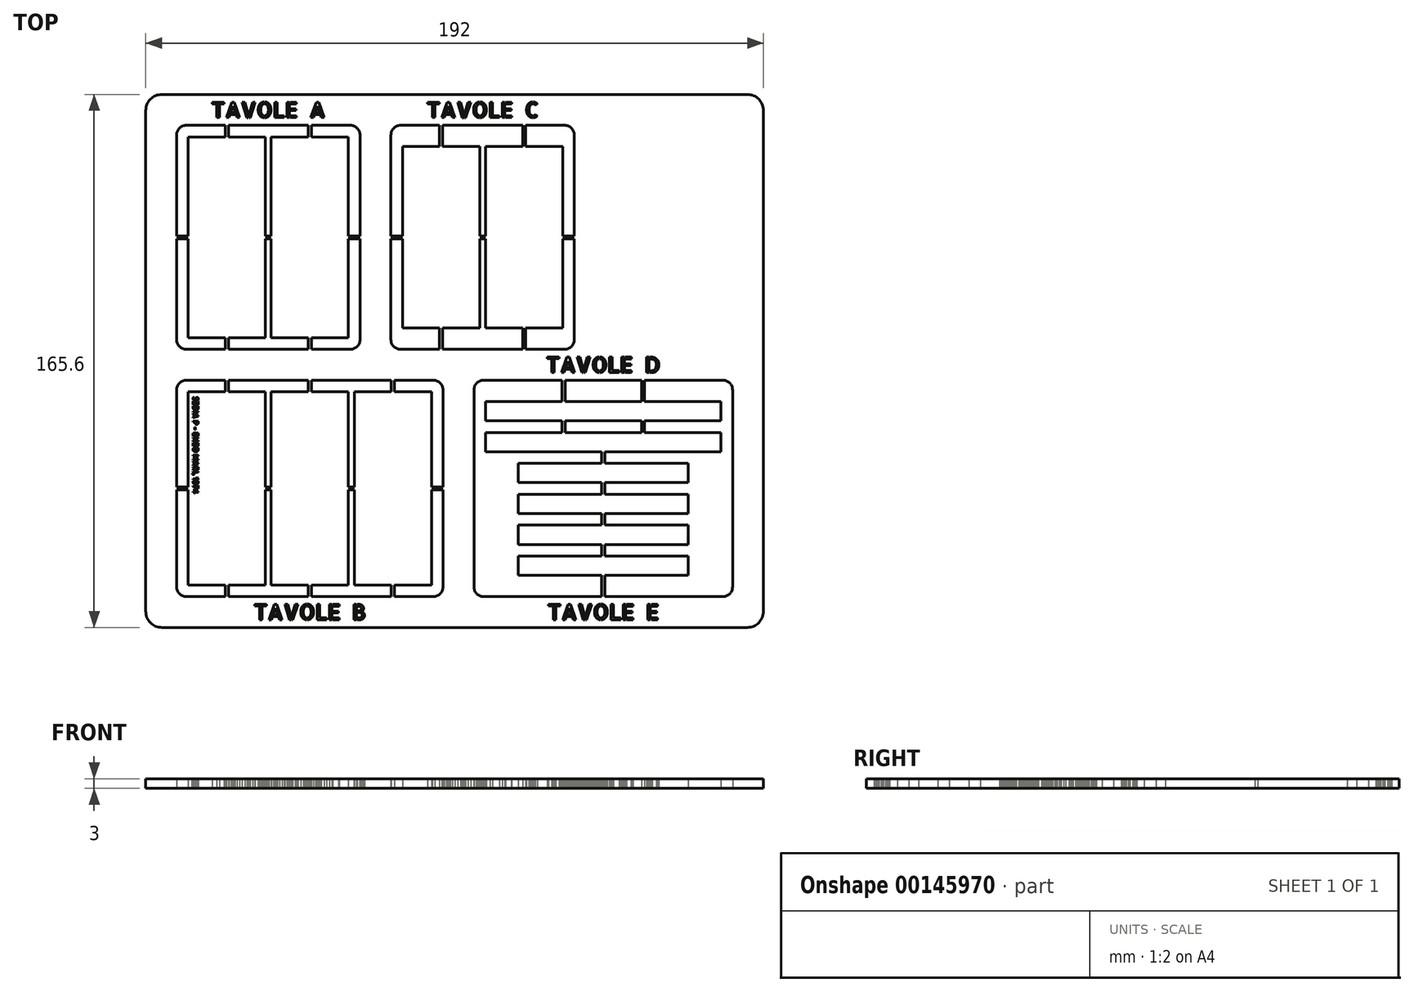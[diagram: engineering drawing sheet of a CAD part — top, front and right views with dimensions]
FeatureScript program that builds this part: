
annotation { "Feature Type Name" : "Feature", "Feature Type Description" : "" }
export const myFeature = defineFeature(function(context is Context, id is Id, definition is map)
    precondition{}
    {
        {
            assignVariable(context, id + "F0", {"name" : "scale", "anyValue" : 3 / 25});
        }
        {
            assignVariable(context, id + "F1", {"name" : "wood_thickness", "anyValue" : 25 * mm * getVariable(context, 'scale')});
        }
        {
            var Q0;
            Q0=qCreatedBy(makeId("Top.planeOp"),FACE);
            var sketch = newSketch(context, id + "F2", { "sketchPlane" : qUnion([Q0])});
            skLineSegment(sketch, "E0.bottom", {"start": v(9.6, 9.6) * mm, "end": v(24.72, 9.6) * mm});
            skLineSegment(sketch, "E0.top", {"start": v(9.6, 76.8) * mm, "end": v(24.72, 76.8) * mm});
            skLineSegment(sketch, "E0.left", {"start": v(9.6, 9.6) * mm, "end": v(9.6, 42.72) * mm});
            skLineSegment(sketch, "E0.right", {"start": v(92.4, 9.6) * mm, "end": v(92.4, 42.72) * mm});
            skLineSegment(sketch, "E1.bottom", {"start": v(13.2, 73.2) * mm, "end": v(24.72, 73.2) * mm});
            skLineSegment(sketch, "E1.top", {"start": v(13.2, 13.2) * mm, "end": v(24.72, 13.2) * mm});
            skLineSegment(sketch, "E1.left", {"start": v(13.2, 73.2) * mm, "end": v(13.2, 43.68) * mm});
            skLineSegment(sketch, "E1.right", {"start": v(37.2, 73.2) * mm, "end": v(37.2, 43.68) * mm});
            skLineSegment(sketch, "E2", {"start": v(9.6, 43.2) * mm, "end": v(13.2, 43.2) * mm, "construction": true});
            skLineSegment(sketch, "E3", {"start": v(25.2, 73.2) * mm, "end": v(25.2, 76.8) * mm, "construction": true});
            skLineSegment(sketch, "E4", {"start": v(25.2, 13.2) * mm, "end": v(25.2, 9.6) * mm, "construction": true});
            skLineSegment(sketch, "E5", {"start": v(9.6, 43.68) * mm, "end": v(13.2, 43.68) * mm});
            skLineSegment(sketch, "E6", {"start": v(9.6, 42.72) * mm, "end": v(13.2, 42.72) * mm});
            skLineSegment(sketch, "E7", {"start": v(24.72, 76.8) * mm, "end": v(24.72, 73.2) * mm});
            skLineSegment(sketch, "E8", {"start": v(25.68, 76.8) * mm, "end": v(25.68, 73.2) * mm});
            skLineSegment(sketch, "E9", {"start": v(24.72, 13.2) * mm, "end": v(24.72, 9.6) * mm});
            skLineSegment(sketch, "E10", {"start": v(25.68, 9.6) * mm, "end": v(25.68, 13.2) * mm});
            skLineSegment(sketch, "E11", {"start": v(24.72, 13.2) * mm, "end": v(25.2, 13.2) * mm, "construction": true});
            skLineSegment(sketch, "E12", {"start": v(25.68, 13.2) * mm, "end": v(37.2, 13.2) * mm});
            skLineSegment(sketch, "E13", {"start": v(25.2, 13.2) * mm, "end": v(25.68, 13.2) * mm, "construction": true});
            skLineSegment(sketch, "E14", {"start": v(13.2, 42.72) * mm, "end": v(13.2, 13.2) * mm});
            skLineSegment(sketch, "E15", {"start": v(13.2, 43.2) * mm, "end": v(13.2, 42.72) * mm, "construction": true});
            skLineSegment(sketch, "E16", {"start": v(13.2, 43.68) * mm, "end": v(13.2, 43.2) * mm, "construction": true});
            skLineSegment(sketch, "E17", {"start": v(24.72, 73.2) * mm, "end": v(25.2, 73.2) * mm, "construction": true});
            skLineSegment(sketch, "E18", {"start": v(25.2, 73.2) * mm, "end": v(25.68, 73.2) * mm, "construction": true});
            skLineSegment(sketch, "E19", {"start": v(25.68, 73.2) * mm, "end": v(37.2, 73.2) * mm});
            skLineSegment(sketch, "E20", {"start": v(13.2, 58.44) * mm, "end": v(37.2, 58.44) * mm, "construction": true});
            skLineSegment(sketch, "E21", {"start": v(13.2, 43.2) * mm, "end": v(37.2, 43.2) * mm, "construction": true});
            skLineSegment(sketch, "E22", {"start": v(37.2, 43.68) * mm, "end": v(37.2, 43.2) * mm, "construction": true});
            skLineSegment(sketch, "E23", {"start": v(37.2, 43.2) * mm, "end": v(37.2, 42.72) * mm, "construction": true});
            skLineSegment(sketch, "E24", {"start": v(37.2, 42.72) * mm, "end": v(37.2, 13.2) * mm});
            skLineSegment(sketch, "E25", {"start": v(39, 13.2) * mm, "end": v(50.52, 13.2) * mm});
            skLineSegment(sketch, "E26", {"start": v(50.52, 13.2) * mm, "end": v(51, 13.2) * mm, "construction": true});
            skLineSegment(sketch, "E27", {"start": v(51, 13.2) * mm, "end": v(51.48, 13.2) * mm, "construction": true});
            skLineSegment(sketch, "E28", {"start": v(51.48, 13.2) * mm, "end": v(63, 13.2) * mm});
            skLineSegment(sketch, "E29", {"start": v(64.8, 13.2) * mm, "end": v(76.32, 13.2) * mm});
            skLineSegment(sketch, "E30", {"start": v(76.32, 13.2) * mm, "end": v(76.8, 13.2) * mm, "construction": true});
            skLineSegment(sketch, "E31", {"start": v(76.8, 13.2) * mm, "end": v(77.28, 13.2) * mm, "construction": true});
            skLineSegment(sketch, "E32", {"start": v(77.28, 13.2) * mm, "end": v(88.8, 13.2) * mm});
            skLineSegment(sketch, "E33", {"start": v(39, 73.2) * mm, "end": v(50.52, 73.2) * mm});
            skLineSegment(sketch, "E34", {"start": v(50.52, 73.2) * mm, "end": v(51, 73.2) * mm, "construction": true});
            skLineSegment(sketch, "E35", {"start": v(51, 73.2) * mm, "end": v(51.48, 73.2) * mm, "construction": true});
            skLineSegment(sketch, "E36", {"start": v(51.48, 73.2) * mm, "end": v(63, 73.2) * mm});
            skLineSegment(sketch, "E37", {"start": v(64.8, 73.2) * mm, "end": v(76.32, 73.2) * mm});
            skLineSegment(sketch, "E38", {"start": v(76.32, 73.2) * mm, "end": v(76.8, 73.2) * mm, "construction": true});
            skLineSegment(sketch, "E39", {"start": v(76.8, 73.2) * mm, "end": v(77.28, 73.2) * mm, "construction": true});
            skLineSegment(sketch, "E40", {"start": v(77.28, 73.2) * mm, "end": v(88.8, 73.2) * mm});
            skLineSegment(sketch, "E41", {"start": v(39, 73.2) * mm, "end": v(39, 43.68) * mm});
            skLineSegment(sketch, "E42", {"start": v(39, 43.68) * mm, "end": v(39, 43.2) * mm, "construction": true});
            skLineSegment(sketch, "E43", {"start": v(39, 43.2) * mm, "end": v(39, 42.72) * mm, "construction": true});
            skLineSegment(sketch, "E44", {"start": v(39, 42.72) * mm, "end": v(39, 13.2) * mm});
            skLineSegment(sketch, "E45", {"start": v(63, 73.2) * mm, "end": v(63, 43.68) * mm});
            skLineSegment(sketch, "E46", {"start": v(63, 43.68) * mm, "end": v(63, 43.2) * mm, "construction": true});
            skLineSegment(sketch, "E47", {"start": v(63, 43.2) * mm, "end": v(63, 42.72) * mm, "construction": true});
            skLineSegment(sketch, "E48", {"start": v(63, 13.2) * mm, "end": v(63, 42.72) * mm});
            skLineSegment(sketch, "E49", {"start": v(64.8, 73.2) * mm, "end": v(64.8, 43.68) * mm});
            skLineSegment(sketch, "E50", {"start": v(64.8, 43.68) * mm, "end": v(64.8, 43.2) * mm, "construction": true});
            skLineSegment(sketch, "E51", {"start": v(64.8, 43.2) * mm, "end": v(64.8, 42.72) * mm, "construction": true});
            skLineSegment(sketch, "E52", {"start": v(64.8, 42.72) * mm, "end": v(64.8, 13.2) * mm});
            skLineSegment(sketch, "E53", {"start": v(88.8, 13.2) * mm, "end": v(88.8, 42.72) * mm});
            skLineSegment(sketch, "E54", {"start": v(88.8, 42.72) * mm, "end": v(88.8, 43.2) * mm, "construction": true});
            skLineSegment(sketch, "E55", {"start": v(88.8, 43.2) * mm, "end": v(88.8, 43.68) * mm, "construction": true});
            skLineSegment(sketch, "E56", {"start": v(88.8, 43.68) * mm, "end": v(88.8, 73.2) * mm});
            skLineSegment(sketch, "E57", {"start": v(37.2, 43.68) * mm, "end": v(39, 43.68) * mm});
            skLineSegment(sketch, "E58", {"start": v(39, 42.72) * mm, "end": v(37.2, 42.72) * mm});
            skLineSegment(sketch, "E59", {"start": v(63, 43.68) * mm, "end": v(64.8, 43.68) * mm});
            skLineSegment(sketch, "E60", {"start": v(64.8, 42.72) * mm, "end": v(63, 42.72) * mm});
            skLineSegment(sketch, "E61", {"start": v(88.8, 43.68) * mm, "end": v(92.4, 43.68) * mm});
            skLineSegment(sketch, "E62", {"start": v(88.8, 42.72) * mm, "end": v(92.4, 42.72) * mm});
            skLineSegment(sketch, "E63", {"start": v(24.72, 76.8) * mm, "end": v(25.68, 76.8) * mm});
            skLineSegment(sketch, "E64", {"start": v(25.68, 76.8) * mm, "end": v(50.52, 76.8) * mm});
            skLineSegment(sketch, "E65", {"start": v(24.72, 9.6) * mm, "end": v(25.68, 9.6) * mm});
            skLineSegment(sketch, "E66", {"start": v(25.68, 9.6) * mm, "end": v(50.52, 9.6) * mm});
            skLineSegment(sketch, "E67", {"start": v(50.52, 13.2) * mm, "end": v(50.52, 9.6) * mm});
            skLineSegment(sketch, "E68", {"start": v(51.48, 13.2) * mm, "end": v(51.48, 9.6) * mm});
            skLineSegment(sketch, "E69", {"start": v(76.32, 13.2) * mm, "end": v(76.32, 9.6) * mm});
            skLineSegment(sketch, "E70", {"start": v(77.28, 13.2) * mm, "end": v(77.28, 9.6) * mm});
            skLineSegment(sketch, "E71", {"start": v(76.32, 73.2) * mm, "end": v(76.32, 76.8) * mm});
            skLineSegment(sketch, "E72", {"start": v(77.28, 73.2) * mm, "end": v(77.28, 76.8) * mm});
            skLineSegment(sketch, "E73", {"start": v(50.52, 73.2) * mm, "end": v(50.52, 76.8) * mm});
            skLineSegment(sketch, "E74", {"start": v(51.48, 73.2) * mm, "end": v(51.48, 76.8) * mm});
            skLineSegment(sketch, "E75", {"start": v(50.52, 76.8) * mm, "end": v(51.48, 76.8) * mm});
            skLineSegment(sketch, "E76", {"start": v(51.48, 76.8) * mm, "end": v(76.32, 76.8) * mm});
            skLineSegment(sketch, "E77", {"start": v(76.32, 76.8) * mm, "end": v(77.28, 76.8) * mm});
            skLineSegment(sketch, "E78", {"start": v(77.28, 76.8) * mm, "end": v(92.4, 76.8) * mm});
            skLineSegment(sketch, "E79", {"start": v(92.4, 43.68) * mm, "end": v(92.4, 76.8) * mm});
            skLineSegment(sketch, "E80", {"start": v(92.4, 42.72) * mm, "end": v(92.4, 43.68) * mm});
            skLineSegment(sketch, "E81", {"start": v(77.28, 9.6) * mm, "end": v(92.4, 9.6) * mm});
            skLineSegment(sketch, "E82", {"start": v(76.32, 9.6) * mm, "end": v(77.28, 9.6) * mm});
            skLineSegment(sketch, "E83", {"start": v(51.48, 9.6) * mm, "end": v(76.32, 9.6) * mm});
            skLineSegment(sketch, "E84", {"start": v(50.52, 9.6) * mm, "end": v(51.48, 9.6) * mm});
            skLineSegment(sketch, "E85", {"start": v(9.6, 42.72) * mm, "end": v(9.6, 43.68) * mm});
            skLineSegment(sketch, "E86", {"start": v(9.6, 43.68) * mm, "end": v(9.6, 76.8) * mm});
            skSolve(sketch);
        }
        {
            var Q0;
            Q0=makeQuery(id+"F2.imprint","IMPRINT",FACE,{"disambiguationData":[TD([[makeQuery(id+"F2.imprint","IMPRINT",EDGE,{"derivedFrom":sQuery(id+"F2.wireOp",EDGE,"E1.bottom")}),-1.0]])]});
            extrude(context, id + "F3", {"entities" : qUnion([Q0]), "depth" : getVariable(context, 'wood_thickness')});
        }
        {
            var Q0;
            Q0=qCreatedBy(makeId("Top.planeOp"),FACE);
            var sketch = newSketch(context, id + "F4", { "sketchPlane" : qUnion([Q0])});
            skLineSegment(sketch, "E87.bottom", {"start": v(9.6, 86.4) * mm, "end": v(24.72, 86.4) * mm});
            skLineSegment(sketch, "E87.top", {"start": v(9.6, 156) * mm, "end": v(24.72, 156) * mm});
            skLineSegment(sketch, "E87.left", {"start": v(9.6, 86.4) * mm, "end": v(9.6, 120.72) * mm});
            skLineSegment(sketch, "E87.right", {"start": v(66.6, 86.4) * mm, "end": v(66.6, 120.72) * mm});
            skLineSegment(sketch, "E88.bottom", {"start": v(13.2, 152.4) * mm, "end": v(24.72, 152.4) * mm});
            skLineSegment(sketch, "E88.top", {"start": v(13.2, 90) * mm, "end": v(24.72, 90) * mm});
            skLineSegment(sketch, "E88.left", {"start": v(13.2, 152.4) * mm, "end": v(13.2, 121.68) * mm});
            skLineSegment(sketch, "E88.right", {"start": v(37.2, 152.4) * mm, "end": v(37.2, 121.68) * mm});
            skLineSegment(sketch, "E89", {"start": v(9.6, 121.2) * mm, "end": v(13.2, 121.2) * mm, "construction": true});
            skLineSegment(sketch, "E90", {"start": v(25.2, 152.4) * mm, "end": v(25.2, 156) * mm, "construction": true});
            skLineSegment(sketch, "E91", {"start": v(25.2, 90) * mm, "end": v(25.2, 86.4) * mm, "construction": true});
            skLineSegment(sketch, "E92", {"start": v(9.6, 121.68) * mm, "end": v(13.2, 121.68) * mm});
            skLineSegment(sketch, "E93", {"start": v(9.6, 120.72) * mm, "end": v(13.2, 120.72) * mm});
            skLineSegment(sketch, "E94", {"start": v(24.72, 156) * mm, "end": v(24.72, 152.4) * mm});
            skLineSegment(sketch, "E95", {"start": v(25.68, 156) * mm, "end": v(25.68, 152.4) * mm});
            skLineSegment(sketch, "E96", {"start": v(24.72, 90) * mm, "end": v(24.72, 86.4) * mm});
            skLineSegment(sketch, "E97", {"start": v(25.68, 86.4) * mm, "end": v(25.68, 90) * mm});
            skLineSegment(sketch, "E98", {"start": v(24.72, 90) * mm, "end": v(25.2, 90) * mm, "construction": true});
            skLineSegment(sketch, "E99", {"start": v(25.68, 90) * mm, "end": v(37.2, 90) * mm});
            skLineSegment(sketch, "E100", {"start": v(25.2, 90) * mm, "end": v(25.68, 90) * mm, "construction": true});
            skLineSegment(sketch, "E101", {"start": v(13.2, 120.72) * mm, "end": v(13.2, 90) * mm});
            skLineSegment(sketch, "E102", {"start": v(13.2, 121.2) * mm, "end": v(13.2, 120.72) * mm, "construction": true});
            skLineSegment(sketch, "E103", {"start": v(13.2, 121.68) * mm, "end": v(13.2, 121.2) * mm, "construction": true});
            skLineSegment(sketch, "E104", {"start": v(24.72, 152.4) * mm, "end": v(25.2, 152.4) * mm, "construction": true});
            skLineSegment(sketch, "E105", {"start": v(25.2, 152.4) * mm, "end": v(25.68, 152.4) * mm, "construction": true});
            skLineSegment(sketch, "E106", {"start": v(25.68, 152.4) * mm, "end": v(37.2, 152.4) * mm});
            skLineSegment(sketch, "E107", {"start": v(13.2, 137.04) * mm, "end": v(37.2, 137.04) * mm, "construction": true});
            skLineSegment(sketch, "E108", {"start": v(13.2, 121.2) * mm, "end": v(37.2, 121.2) * mm, "construction": true});
            skLineSegment(sketch, "E109", {"start": v(37.2, 121.68) * mm, "end": v(37.2, 121.2) * mm, "construction": true});
            skLineSegment(sketch, "E110", {"start": v(37.2, 121.2) * mm, "end": v(37.2, 120.72) * mm, "construction": true});
            skLineSegment(sketch, "E111", {"start": v(37.2, 120.72) * mm, "end": v(37.2, 90) * mm});
            skLineSegment(sketch, "E112", {"start": v(39, 90) * mm, "end": v(50.52, 90) * mm});
            skLineSegment(sketch, "E113", {"start": v(50.52, 90) * mm, "end": v(51, 90) * mm, "construction": true});
            skLineSegment(sketch, "E114", {"start": v(51, 90) * mm, "end": v(51.48, 90) * mm, "construction": true});
            skLineSegment(sketch, "E115", {"start": v(51.48, 90) * mm, "end": v(63, 90) * mm});
            skLineSegment(sketch, "E116", {"start": v(39, 152.4) * mm, "end": v(50.52, 152.4) * mm});
            skLineSegment(sketch, "E117", {"start": v(50.52, 152.4) * mm, "end": v(51, 152.4) * mm, "construction": true});
            skLineSegment(sketch, "E118", {"start": v(51, 152.4) * mm, "end": v(51.48, 152.4) * mm, "construction": true});
            skLineSegment(sketch, "E119", {"start": v(51.48, 152.4) * mm, "end": v(63, 152.4) * mm});
            skLineSegment(sketch, "E120", {"start": v(39, 152.4) * mm, "end": v(39, 121.68) * mm});
            skLineSegment(sketch, "E121", {"start": v(39, 121.68) * mm, "end": v(39, 121.2) * mm, "construction": true});
            skLineSegment(sketch, "E122", {"start": v(39, 121.2) * mm, "end": v(39, 120.72) * mm, "construction": true});
            skLineSegment(sketch, "E123", {"start": v(39, 120.72) * mm, "end": v(39, 90) * mm});
            skLineSegment(sketch, "E124", {"start": v(63, 152.4) * mm, "end": v(63, 121.68) * mm});
            skLineSegment(sketch, "E125", {"start": v(63, 121.68) * mm, "end": v(63, 121.2) * mm, "construction": true});
            skLineSegment(sketch, "E126", {"start": v(63, 121.2) * mm, "end": v(63, 120.72) * mm, "construction": true});
            skLineSegment(sketch, "E127", {"start": v(63, 90) * mm, "end": v(63, 120.72) * mm});
            skLineSegment(sketch, "E128", {"start": v(37.2, 121.68) * mm, "end": v(39, 121.68) * mm});
            skLineSegment(sketch, "E129", {"start": v(39, 120.72) * mm, "end": v(37.2, 120.72) * mm});
            skLineSegment(sketch, "E130", {"start": v(63, 121.68) * mm, "end": v(66.6, 121.68) * mm});
            skLineSegment(sketch, "E131", {"start": v(63, 120.72) * mm, "end": v(66.6, 120.72) * mm});
            skLineSegment(sketch, "E132", {"start": v(24.72, 156) * mm, "end": v(25.68, 156) * mm});
            skLineSegment(sketch, "E133", {"start": v(25.68, 156) * mm, "end": v(50.52, 156) * mm});
            skLineSegment(sketch, "E134", {"start": v(24.72, 86.4) * mm, "end": v(25.68, 86.4) * mm});
            skLineSegment(sketch, "E135", {"start": v(25.68, 86.4) * mm, "end": v(50.52, 86.4) * mm});
            skLineSegment(sketch, "E136", {"start": v(50.52, 90) * mm, "end": v(50.52, 86.4) * mm});
            skLineSegment(sketch, "E137", {"start": v(51.48, 90) * mm, "end": v(51.48, 86.4) * mm});
            skLineSegment(sketch, "E138", {"start": v(50.52, 152.4) * mm, "end": v(50.52, 156) * mm});
            skLineSegment(sketch, "E139", {"start": v(51.48, 152.4) * mm, "end": v(51.48, 156) * mm});
            skLineSegment(sketch, "E140", {"start": v(50.52, 156) * mm, "end": v(51.48, 156) * mm});
            skLineSegment(sketch, "E141", {"start": v(51.48, 156) * mm, "end": v(66.6, 156) * mm});
            skLineSegment(sketch, "E142", {"start": v(66.6, 121.68) * mm, "end": v(66.6, 156) * mm});
            skLineSegment(sketch, "E143", {"start": v(66.6, 120.72) * mm, "end": v(66.6, 121.68) * mm});
            skLineSegment(sketch, "E144", {"start": v(51.48, 86.4) * mm, "end": v(66.6, 86.4) * mm});
            skLineSegment(sketch, "E145", {"start": v(50.52, 86.4) * mm, "end": v(51.48, 86.4) * mm});
            skLineSegment(sketch, "E146", {"start": v(9.6, 120.72) * mm, "end": v(9.6, 121.68) * mm});
            skLineSegment(sketch, "E147", {"start": v(9.6, 121.68) * mm, "end": v(9.6, 156) * mm});
            skLineSegment(sketch, "E148.0", {"start": v(9.6, 76.8) * mm, "end": v(24.72, 76.8) * mm, "construction": true});
            skSolve(sketch);
        }
        {
            var Q0;
            Q0=makeQuery(id+"F4.imprint","IMPRINT",FACE,{"disambiguationData":[TD([[makeQuery(id+"F4.imprint","IMPRINT",EDGE,{"derivedFrom":sQuery(id+"F4.wireOp",EDGE,"E88.bottom")}),-1.0]])]});
            extrude(context, id + "F5", {"entities" : qUnion([Q0]), "depth" : getVariable(context, 'wood_thickness')});
        }
        {
            var Q0;
            Q0=qCreatedBy(makeId("Top.planeOp"),FACE);
            var sketch = newSketch(context, id + "F6", { "sketchPlane" : qUnion([Q0])});
            skLineSegment(sketch, "E149.bottom", {"start": v(76.2, 86.4) * mm, "end": v(91.32, 86.4) * mm});
            skLineSegment(sketch, "E149.top", {"start": v(76.2, 156) * mm, "end": v(91.32, 156) * mm});
            skLineSegment(sketch, "E149.left", {"start": v(76.2, 86.4) * mm, "end": v(76.2, 120.72) * mm});
            skLineSegment(sketch, "E149.right", {"start": v(133.2, 86.4) * mm, "end": v(133.2, 120.72) * mm});
            skLineSegment(sketch, "E150.bottom", {"start": v(79.8, 149.4) * mm, "end": v(91.32, 149.4) * mm});
            skLineSegment(sketch, "E150.top", {"start": v(79.8, 93) * mm, "end": v(91.32, 93) * mm});
            skLineSegment(sketch, "E150.left", {"start": v(79.8, 149.4) * mm, "end": v(79.8, 121.68) * mm});
            skLineSegment(sketch, "E150.right", {"start": v(103.8, 149.4) * mm, "end": v(103.8, 121.68) * mm});
            skLineSegment(sketch, "E151", {"start": v(76.2, 121.2) * mm, "end": v(79.8, 121.2) * mm, "construction": true});
            skLineSegment(sketch, "E152", {"start": v(91.8, 149.4) * mm, "end": v(91.8, 156) * mm, "construction": true});
            skLineSegment(sketch, "E153", {"start": v(91.8, 93) * mm, "end": v(91.8, 86.4) * mm, "construction": true});
            skLineSegment(sketch, "E154", {"start": v(76.2, 121.68) * mm, "end": v(79.8, 121.68) * mm});
            skLineSegment(sketch, "E155", {"start": v(76.2, 120.72) * mm, "end": v(79.8, 120.72) * mm});
            skLineSegment(sketch, "E156", {"start": v(91.32, 156) * mm, "end": v(91.32, 149.4) * mm});
            skLineSegment(sketch, "E157", {"start": v(92.28, 156) * mm, "end": v(92.28, 149.4) * mm});
            skLineSegment(sketch, "E158", {"start": v(91.32, 93) * mm, "end": v(91.32, 86.4) * mm});
            skLineSegment(sketch, "E159", {"start": v(92.28, 86.4) * mm, "end": v(92.28, 93) * mm});
            skLineSegment(sketch, "E160", {"start": v(91.32, 93) * mm, "end": v(91.8, 93) * mm, "construction": true});
            skLineSegment(sketch, "E161", {"start": v(92.28, 93) * mm, "end": v(103.8, 93) * mm});
            skLineSegment(sketch, "E162", {"start": v(91.8, 93) * mm, "end": v(92.28, 93) * mm, "construction": true});
            skLineSegment(sketch, "E163", {"start": v(79.8, 120.72) * mm, "end": v(79.8, 93) * mm});
            skLineSegment(sketch, "E164", {"start": v(79.8, 121.2) * mm, "end": v(79.8, 120.72) * mm, "construction": true});
            skLineSegment(sketch, "E165", {"start": v(79.8, 121.68) * mm, "end": v(79.8, 121.2) * mm, "construction": true});
            skLineSegment(sketch, "E166", {"start": v(91.32, 149.4) * mm, "end": v(91.8, 149.4) * mm, "construction": true});
            skLineSegment(sketch, "E167", {"start": v(91.8, 149.4) * mm, "end": v(92.28, 149.4) * mm, "construction": true});
            skLineSegment(sketch, "E168", {"start": v(92.28, 149.4) * mm, "end": v(103.8, 149.4) * mm});
            skLineSegment(sketch, "E169", {"start": v(79.8, 135.54) * mm, "end": v(103.8, 135.54) * mm, "construction": true});
            skLineSegment(sketch, "E170", {"start": v(79.8, 121.2) * mm, "end": v(103.8, 121.2) * mm, "construction": true});
            skLineSegment(sketch, "E171", {"start": v(103.8, 121.68) * mm, "end": v(103.8, 121.2) * mm, "construction": true});
            skLineSegment(sketch, "E172", {"start": v(103.8, 121.2) * mm, "end": v(103.8, 120.72) * mm, "construction": true});
            skLineSegment(sketch, "E173", {"start": v(103.8, 120.72) * mm, "end": v(103.8, 93) * mm});
            skLineSegment(sketch, "E174", {"start": v(105.6, 93) * mm, "end": v(117.12, 93) * mm});
            skLineSegment(sketch, "E175", {"start": v(117.12, 93) * mm, "end": v(117.6, 93) * mm, "construction": true});
            skLineSegment(sketch, "E176", {"start": v(117.6, 93) * mm, "end": v(118.08, 93) * mm, "construction": true});
            skLineSegment(sketch, "E177", {"start": v(118.08, 93) * mm, "end": v(129.6, 93) * mm});
            skLineSegment(sketch, "E178", {"start": v(105.6, 149.4) * mm, "end": v(117.12, 149.4) * mm});
            skLineSegment(sketch, "E179", {"start": v(117.12, 149.4) * mm, "end": v(117.6, 149.4) * mm, "construction": true});
            skLineSegment(sketch, "E180", {"start": v(117.6, 149.4) * mm, "end": v(118.08, 149.4) * mm, "construction": true});
            skLineSegment(sketch, "E181", {"start": v(118.08, 149.4) * mm, "end": v(129.6, 149.4) * mm});
            skLineSegment(sketch, "E182", {"start": v(105.6, 149.4) * mm, "end": v(105.6, 121.68) * mm});
            skLineSegment(sketch, "E183", {"start": v(105.6, 121.68) * mm, "end": v(105.6, 121.2) * mm, "construction": true});
            skLineSegment(sketch, "E184", {"start": v(105.6, 121.2) * mm, "end": v(105.6, 120.72) * mm, "construction": true});
            skLineSegment(sketch, "E185", {"start": v(105.6, 120.72) * mm, "end": v(105.6, 93) * mm});
            skLineSegment(sketch, "E186", {"start": v(129.6, 149.4) * mm, "end": v(129.6, 121.68) * mm});
            skLineSegment(sketch, "E187", {"start": v(129.6, 121.68) * mm, "end": v(129.6, 121.2) * mm, "construction": true});
            skLineSegment(sketch, "E188", {"start": v(129.6, 121.2) * mm, "end": v(129.6, 120.72) * mm, "construction": true});
            skLineSegment(sketch, "E189", {"start": v(129.6, 93) * mm, "end": v(129.6, 120.72) * mm});
            skLineSegment(sketch, "E190", {"start": v(103.8, 121.68) * mm, "end": v(105.6, 121.68) * mm});
            skLineSegment(sketch, "E191", {"start": v(105.6, 120.72) * mm, "end": v(103.8, 120.72) * mm});
            skLineSegment(sketch, "E192", {"start": v(129.6, 121.68) * mm, "end": v(133.2, 121.68) * mm});
            skLineSegment(sketch, "E193", {"start": v(129.6, 120.72) * mm, "end": v(133.2, 120.72) * mm});
            skLineSegment(sketch, "E194", {"start": v(91.32, 156) * mm, "end": v(92.28, 156) * mm});
            skLineSegment(sketch, "E195", {"start": v(92.28, 156) * mm, "end": v(117.12, 156) * mm});
            skLineSegment(sketch, "E196", {"start": v(91.32, 86.4) * mm, "end": v(92.28, 86.4) * mm});
            skLineSegment(sketch, "E197", {"start": v(92.28, 86.4) * mm, "end": v(117.12, 86.4) * mm});
            skLineSegment(sketch, "E198", {"start": v(117.12, 93) * mm, "end": v(117.12, 86.4) * mm});
            skLineSegment(sketch, "E199", {"start": v(118.08, 93) * mm, "end": v(118.08, 86.4) * mm});
            skLineSegment(sketch, "E200", {"start": v(117.12, 149.4) * mm, "end": v(117.12, 156) * mm});
            skLineSegment(sketch, "E201", {"start": v(118.08, 149.4) * mm, "end": v(118.08, 156) * mm});
            skLineSegment(sketch, "E202", {"start": v(117.12, 156) * mm, "end": v(118.08, 156) * mm});
            skLineSegment(sketch, "E203", {"start": v(118.08, 156) * mm, "end": v(133.2, 156) * mm});
            skLineSegment(sketch, "E204", {"start": v(133.2, 121.68) * mm, "end": v(133.2, 156) * mm});
            skLineSegment(sketch, "E205", {"start": v(133.2, 120.72) * mm, "end": v(133.2, 121.68) * mm});
            skLineSegment(sketch, "E206", {"start": v(118.08, 86.4) * mm, "end": v(133.2, 86.4) * mm});
            skLineSegment(sketch, "E207", {"start": v(117.12, 86.4) * mm, "end": v(118.08, 86.4) * mm});
            skLineSegment(sketch, "E208", {"start": v(76.2, 120.72) * mm, "end": v(76.2, 121.68) * mm});
            skLineSegment(sketch, "E209", {"start": v(76.2, 121.68) * mm, "end": v(76.2, 156) * mm});
            skSolve(sketch);
        }
        {
            var Q0;
            Q0=makeQuery(id+"F6.imprint","IMPRINT",FACE,{"disambiguationData":[TD([[makeQuery(id+"F6.imprint","IMPRINT",EDGE,{"derivedFrom":sQuery(id+"F6.wireOp",EDGE,"E150.bottom")}),-1.0]])]});
            extrude(context, id + "F7", {"entities" : qUnion([Q0]), "depth" : getVariable(context, 'wood_thickness')});
        }
        {
            var Q0;
            Q0=qCreatedBy(makeId("Top.planeOp"),FACE);
            var sketch = newSketch(context, id + "F8", { "sketchPlane" : qUnion([Q0])});
            skLineSegment(sketch, "E210.bottom", {"start": v(102, 9.6) * mm, "end": v(182.4, 9.6) * mm});
            skLineSegment(sketch, "E210.top", {"start": v(102, 76.8) * mm, "end": v(182.4, 76.8) * mm});
            skLineSegment(sketch, "E210.left", {"start": v(102, 9.6) * mm, "end": v(102, 76.8) * mm});
            skLineSegment(sketch, "E210.right", {"start": v(182.4, 9.6) * mm, "end": v(182.4, 76.8) * mm});
            skLineSegment(sketch, "E211", {"start": v(105.6, 70.2) * mm, "end": v(129.36, 70.2) * mm});
            skLineSegment(sketch, "E212", {"start": v(129.36, 70.2) * mm, "end": v(129.84, 70.2) * mm, "construction": true});
            skLineSegment(sketch, "E213", {"start": v(129.84, 70.2) * mm, "end": v(130.32, 70.2) * mm, "construction": true});
            skLineSegment(sketch, "E214", {"start": v(130.32, 70.2) * mm, "end": v(154.08, 70.2) * mm});
            skLineSegment(sketch, "E215", {"start": v(178.8, 70.2) * mm, "end": v(178.8, 64.2) * mm});
            skLineSegment(sketch, "E216", {"start": v(155.04, 64.2) * mm, "end": v(178.8, 64.2) * mm});
            skLineSegment(sketch, "E217", {"start": v(130.32, 64.2) * mm, "end": v(129.84, 64.2) * mm, "construction": true});
            skLineSegment(sketch, "E218", {"start": v(129.84, 64.2) * mm, "end": v(129.36, 64.2) * mm, "construction": true});
            skLineSegment(sketch, "E219", {"start": v(129.36, 64.2) * mm, "end": v(105.6, 64.2) * mm});
            skLineSegment(sketch, "E220", {"start": v(105.6, 64.2) * mm, "end": v(105.6, 70.2) * mm});
            skLineSegment(sketch, "E221", {"start": v(129.36, 60.6) * mm, "end": v(105.6, 60.6) * mm});
            skLineSegment(sketch, "E222", {"start": v(105.6, 60.6) * mm, "end": v(105.6, 54.6) * mm});
            skLineSegment(sketch, "E223", {"start": v(105.6, 54.6) * mm, "end": v(141.72, 54.6) * mm});
            skLineSegment(sketch, "E224", {"start": v(141.72, 54.6) * mm, "end": v(142.2, 54.6) * mm, "construction": true});
            skLineSegment(sketch, "E225", {"start": v(142.2, 54.6) * mm, "end": v(142.68, 54.6) * mm, "construction": true});
            skLineSegment(sketch, "E226", {"start": v(142.68, 54.6) * mm, "end": v(178.8, 54.6) * mm});
            skLineSegment(sketch, "E227", {"start": v(178.8, 54.6) * mm, "end": v(178.8, 60.6) * mm});
            skLineSegment(sketch, "E228", {"start": v(178.8, 60.6) * mm, "end": v(155.04, 60.6) * mm});
            skLineSegment(sketch, "E229", {"start": v(130.32, 60.6) * mm, "end": v(129.84, 60.6) * mm, "construction": true});
            skLineSegment(sketch, "E230", {"start": v(129.84, 60.6) * mm, "end": v(129.36, 60.6) * mm, "construction": true});
            skLineSegment(sketch, "E231", {"start": v(154.08, 70.2) * mm, "end": v(154.56, 70.2) * mm, "construction": true});
            skLineSegment(sketch, "E232", {"start": v(154.56, 70.2) * mm, "end": v(155.04, 70.2) * mm, "construction": true});
            skLineSegment(sketch, "E233", {"start": v(155.04, 70.2) * mm, "end": v(178.8, 70.2) * mm});
            skLineSegment(sketch, "E234", {"start": v(130.32, 64.2) * mm, "end": v(154.08, 64.2) * mm});
            skLineSegment(sketch, "E235", {"start": v(154.08, 64.2) * mm, "end": v(154.56, 64.2) * mm, "construction": true});
            skLineSegment(sketch, "E236", {"start": v(154.56, 64.2) * mm, "end": v(155.04, 64.2) * mm, "construction": true});
            skLineSegment(sketch, "E237", {"start": v(154.08, 60.6) * mm, "end": v(130.32, 60.6) * mm});
            skLineSegment(sketch, "E238", {"start": v(154.56, 60.6) * mm, "end": v(154.08, 60.6) * mm, "construction": true});
            skLineSegment(sketch, "E239", {"start": v(155.04, 60.6) * mm, "end": v(154.56, 60.6) * mm, "construction": true});
            skLineSegment(sketch, "E240", {"start": v(129.36, 70.2) * mm, "end": v(129.36, 76.8) * mm});
            skLineSegment(sketch, "E241", {"start": v(130.32, 70.2) * mm, "end": v(130.32, 76.8) * mm});
            skLineSegment(sketch, "E242", {"start": v(154.08, 70.2) * mm, "end": v(154.08, 76.8) * mm});
            skLineSegment(sketch, "E243", {"start": v(155.04, 70.2) * mm, "end": v(155.04, 76.8) * mm});
            skLineSegment(sketch, "E244", {"start": v(129.36, 60.6) * mm, "end": v(129.36, 64.2) * mm});
            skLineSegment(sketch, "E245", {"start": v(130.32, 60.6) * mm, "end": v(130.32, 64.2) * mm});
            skLineSegment(sketch, "E246", {"start": v(154.08, 60.6) * mm, "end": v(154.08, 64.2) * mm});
            skLineSegment(sketch, "E247", {"start": v(155.04, 60.6) * mm, "end": v(155.04, 64.2) * mm});
            skLineSegment(sketch, "E248.bottom", {"start": v(115.8, 51) * mm, "end": v(141.72, 51) * mm});
            skLineSegment(sketch, "E248.top", {"start": v(115.8, 45) * mm, "end": v(141.72, 45) * mm});
            skLineSegment(sketch, "E248.left", {"start": v(115.8, 51) * mm, "end": v(115.8, 45) * mm});
            skLineSegment(sketch, "E248.right", {"start": v(168.6, 51) * mm, "end": v(168.6, 45) * mm});
            skLineSegment(sketch, "E249.bottom", {"start": v(115.8, 41.4) * mm, "end": v(141.72, 41.4) * mm});
            skLineSegment(sketch, "E249.top", {"start": v(115.8, 35.4) * mm, "end": v(141.72, 35.4) * mm});
            skLineSegment(sketch, "E249.left", {"start": v(115.8, 41.4) * mm, "end": v(115.8, 35.4) * mm});
            skLineSegment(sketch, "E249.right", {"start": v(168.6, 41.4) * mm, "end": v(168.6, 35.4) * mm});
            skLineSegment(sketch, "E250.bottom", {"start": v(115.8, 31.8) * mm, "end": v(141.72, 31.8) * mm});
            skLineSegment(sketch, "E250.top", {"start": v(115.8, 25.8) * mm, "end": v(141.72, 25.8) * mm});
            skLineSegment(sketch, "E250.left", {"start": v(115.8, 31.8) * mm, "end": v(115.8, 25.8) * mm});
            skLineSegment(sketch, "E250.right", {"start": v(168.6, 31.8) * mm, "end": v(168.6, 25.8) * mm});
            skLineSegment(sketch, "E251.bottom", {"start": v(115.8, 22.2) * mm, "end": v(141.72, 22.2) * mm});
            skLineSegment(sketch, "E251.top", {"start": v(115.8, 16.2) * mm, "end": v(141.72, 16.2) * mm});
            skLineSegment(sketch, "E251.left", {"start": v(115.8, 22.2) * mm, "end": v(115.8, 16.2) * mm});
            skLineSegment(sketch, "E251.right", {"start": v(168.6, 22.2) * mm, "end": v(168.6, 16.2) * mm});
            skLineSegment(sketch, "E252", {"start": v(141.72, 51) * mm, "end": v(142.2, 51) * mm, "construction": true});
            skLineSegment(sketch, "E253", {"start": v(142.2, 51) * mm, "end": v(142.68, 51) * mm, "construction": true});
            skLineSegment(sketch, "E254", {"start": v(142.68, 51) * mm, "end": v(168.6, 51) * mm});
            skLineSegment(sketch, "E255", {"start": v(142.68, 45) * mm, "end": v(168.6, 45) * mm});
            skLineSegment(sketch, "E256", {"start": v(142.2, 45) * mm, "end": v(142.68, 45) * mm, "construction": true});
            skLineSegment(sketch, "E257", {"start": v(141.72, 45) * mm, "end": v(142.2, 45) * mm, "construction": true});
            skLineSegment(sketch, "E258", {"start": v(141.72, 41.4) * mm, "end": v(142.2, 41.4) * mm, "construction": true});
            skLineSegment(sketch, "E259", {"start": v(142.2, 41.4) * mm, "end": v(142.68, 41.4) * mm, "construction": true});
            skLineSegment(sketch, "E260", {"start": v(142.68, 41.4) * mm, "end": v(168.6, 41.4) * mm});
            skLineSegment(sketch, "E261", {"start": v(141.72, 35.4) * mm, "end": v(142.2, 35.4) * mm, "construction": true});
            skLineSegment(sketch, "E262", {"start": v(142.2, 35.4) * mm, "end": v(142.68, 35.4) * mm, "construction": true});
            skLineSegment(sketch, "E263", {"start": v(142.68, 35.4) * mm, "end": v(168.6, 35.4) * mm});
            skLineSegment(sketch, "E264", {"start": v(141.72, 31.8) * mm, "end": v(142.2, 31.8) * mm, "construction": true});
            skLineSegment(sketch, "E265", {"start": v(142.2, 31.8) * mm, "end": v(142.68, 31.8) * mm, "construction": true});
            skLineSegment(sketch, "E266", {"start": v(142.68, 31.8) * mm, "end": v(168.6, 31.8) * mm});
            skLineSegment(sketch, "E267", {"start": v(141.72, 25.8) * mm, "end": v(142.2, 25.8) * mm, "construction": true});
            skLineSegment(sketch, "E268", {"start": v(142.2, 25.8) * mm, "end": v(142.68, 25.8) * mm, "construction": true});
            skLineSegment(sketch, "E269", {"start": v(142.68, 25.8) * mm, "end": v(168.6, 25.8) * mm});
            skLineSegment(sketch, "E270", {"start": v(141.72, 22.2) * mm, "end": v(142.2, 22.2) * mm, "construction": true});
            skLineSegment(sketch, "E271", {"start": v(141.72, 16.2) * mm, "end": v(142.2, 16.2) * mm, "construction": true});
            skLineSegment(sketch, "E272", {"start": v(142.68, 22.2) * mm, "end": v(168.6, 22.2) * mm});
            skLineSegment(sketch, "E273", {"start": v(142.68, 16.2) * mm, "end": v(168.6, 16.2) * mm});
            skLineSegment(sketch, "E274", {"start": v(142.2, 22.2) * mm, "end": v(142.68, 22.2) * mm, "construction": true});
            skLineSegment(sketch, "E275", {"start": v(142.2, 16.2) * mm, "end": v(142.68, 16.2) * mm, "construction": true});
            skLineSegment(sketch, "E276", {"start": v(141.72, 54.6) * mm, "end": v(141.72, 51) * mm});
            skLineSegment(sketch, "E277", {"start": v(142.68, 54.6) * mm, "end": v(142.68, 51) * mm});
            skLineSegment(sketch, "E278", {"start": v(141.72, 45) * mm, "end": v(141.72, 41.4) * mm});
            skLineSegment(sketch, "E279", {"start": v(142.68, 45) * mm, "end": v(142.68, 41.4) * mm});
            skLineSegment(sketch, "E280", {"start": v(141.72, 35.4) * mm, "end": v(141.72, 31.8) * mm});
            skLineSegment(sketch, "E281", {"start": v(141.72, 25.8) * mm, "end": v(141.72, 22.2) * mm});
            skLineSegment(sketch, "E282", {"start": v(141.72, 16.2) * mm, "end": v(141.72, 9.6) * mm});
            skLineSegment(sketch, "E283", {"start": v(142.68, 35.4) * mm, "end": v(142.68, 31.8) * mm});
            skLineSegment(sketch, "E284", {"start": v(142.68, 25.8) * mm, "end": v(142.68, 22.2) * mm});
            skLineSegment(sketch, "E285", {"start": v(142.68, 16.2) * mm, "end": v(142.68, 9.6) * mm});
            skLineSegment(sketch, "E286", {"start": v(105.6, 60.6) * mm, "end": v(102, 60.6) * mm, "construction": true});
            skLineSegment(sketch, "E287", {"start": v(178.8, 60.6) * mm, "end": v(182.4, 60.6) * mm, "construction": true});
            skSolve(sketch);
        }
        {
            var Q0;
            Q0=makeQuery(id+"F8.imprint","IMPRINT",FACE,{"disambiguationData":[TD([[makeQuery(id+"F8.imprint","IMPRINT",EDGE,{"derivedFrom":sQuery(id+"F8.wireOp",EDGE,"E211")}),-1.0]])]});
            extrude(context, id + "F9", {"entities" : qUnion([Q0]), "depth" : getVariable(context, 'wood_thickness')});
        }
        {
            var Q0;
            Q0=qCreatedBy(makeId("Top.planeOp"),FACE);
            var sketch = newSketch(context, id + "F10", { "sketchPlane" : qUnion([Q0])});
            skLineSegment(sketch, "E288.bottom", {"start": v(5, 0) * mm, "end": v(187, 0) * mm});
            skLineSegment(sketch, "E288.top", {"start": v(5, 165.6) * mm, "end": v(187, 165.6) * mm});
            skLineSegment(sketch, "E288.left", {"start": v(0, 5) * mm, "end": v(0, 160.6) * mm});
            skLineSegment(sketch, "E288.right", {"start": v(192, 5) * mm, "end": v(192, 160.6) * mm});
            skPoint(sketch, "E289.0", {"position": v(9.6, 156) * mm});
            skPoint(sketch, "E289.1", {"position": v(9.6, 9.6) * mm});
            skPoint(sketch, "E289.2", {"position": v(182.4, 9.6) * mm});
            skPoint(sketch, "E290.visualSharp", {"position": v(0, 165.6) * mm});
            skArc(sketch, "E290.filletArc", {"start": v(5, 165.6) * mm, "mid": v(1.46, 164.14) * mm, "end": v(0, 160.6) * mm});
            skPoint(sketch, "E291.visualSharp", {"position": v(192, 165.6) * mm});
            skArc(sketch, "E291.filletArc", {"start": v(192, 160.6) * mm, "mid": v(190.54, 164.14) * mm, "end": v(187, 165.6) * mm});
            skPoint(sketch, "E292.visualSharp", {"position": v(192, 0) * mm});
            skArc(sketch, "E292.filletArc", {"start": v(187, 0) * mm, "mid": v(190.54, 1.46) * mm, "end": v(192, 5) * mm});
            skPoint(sketch, "E293.visualSharp", {"position": v(0, 0) * mm});
            skArc(sketch, "E293.filletArc", {"start": v(0, 5) * mm, "mid": v(1.46, 1.46) * mm, "end": v(5, 0) * mm});
            skLineSegment(sketch, "E294", {"start": v(187, 0) * mm, "end": v(192, 0) * mm, "construction": true});
            skLineSegment(sketch, "E295", {"start": v(192, 0) * mm, "end": v(192, 5) * mm, "construction": true});
            skLineSegment(sketch, "E296", {"start": v(192, 160.6) * mm, "end": v(192, 165.6) * mm, "construction": true});
            skLineSegment(sketch, "E297", {"start": v(192, 165.6) * mm, "end": v(187, 165.6) * mm, "construction": true});
            skLineSegment(sketch, "E298", {"start": v(5, 165.6) * mm, "end": v(0, 165.6) * mm, "construction": true});
            skLineSegment(sketch, "E299", {"start": v(0, 165.6) * mm, "end": v(0, 160.6) * mm, "construction": true});
            skLineSegment(sketch, "E300", {"start": v(0, 5) * mm, "end": v(0, 0) * mm, "construction": true});
            skLineSegment(sketch, "E301", {"start": v(0, 0) * mm, "end": v(5, 0) * mm, "construction": true});
            skPoint(sketch, "E302.0", {"position": v(92.4, 9.6) * mm});
            skPoint(sketch, "E302.1", {"position": v(92.4, 76.8) * mm});
            skPoint(sketch, "E302.2", {"position": v(9.6, 76.8) * mm});
            skPoint(sketch, "E302.3", {"position": v(9.6, 86.4) * mm});
            skPoint(sketch, "E302.4", {"position": v(66.6, 86.4) * mm});
            skPoint(sketch, "E302.5", {"position": v(66.6, 156) * mm});
            skPoint(sketch, "E302.6", {"position": v(76.2, 156) * mm});
            skPoint(sketch, "E302.7", {"position": v(76.2, 86.4) * mm});
            skPoint(sketch, "E302.8", {"position": v(133.2, 86.4) * mm});
            skPoint(sketch, "E302.9", {"position": v(133.2, 156) * mm});
            skPoint(sketch, "E302.10", {"position": v(182.4, 76.8) * mm});
            skPoint(sketch, "E302.11", {"position": v(102, 76.8) * mm});
            skPoint(sketch, "E302.12", {"position": v(102, 9.6) * mm});
            skLineSegment(sketch, "E303", {"start": v(182.4, 12.6) * mm, "end": v(182.4, 73.8) * mm});
            skLineSegment(sketch, "E304", {"start": v(179.4, 76.8) * mm, "end": v(105, 76.8) * mm});
            skLineSegment(sketch, "E305", {"start": v(102, 73.8) * mm, "end": v(102, 12.6) * mm});
            skLineSegment(sketch, "E306", {"start": v(179.4, 9.6) * mm, "end": v(105, 9.6) * mm});
            skLineSegment(sketch, "E307", {"start": v(92.4, 12.6) * mm, "end": v(92.4, 73.8) * mm});
            skLineSegment(sketch, "E308", {"start": v(89.4, 76.8) * mm, "end": v(12.6, 76.8) * mm});
            skLineSegment(sketch, "E309", {"start": v(9.6, 73.8) * mm, "end": v(9.6, 12.6) * mm});
            skLineSegment(sketch, "E310", {"start": v(12.6, 9.6) * mm, "end": v(89.4, 9.6) * mm});
            skLineSegment(sketch, "E311", {"start": v(12.6, 156) * mm, "end": v(63.6, 156) * mm});
            skLineSegment(sketch, "E312", {"start": v(79.2, 156) * mm, "end": v(130.2, 156) * mm});
            skLineSegment(sketch, "E313", {"start": v(133.2, 153) * mm, "end": v(133.2, 89.4) * mm});
            skLineSegment(sketch, "E314", {"start": v(130.2, 86.4) * mm, "end": v(79.2, 86.4) * mm});
            skLineSegment(sketch, "E315", {"start": v(63.6, 86.4) * mm, "end": v(12.6, 86.4) * mm});
            skLineSegment(sketch, "E316", {"start": v(9.6, 89.4) * mm, "end": v(9.6, 153) * mm});
            skLineSegment(sketch, "E317", {"start": v(66.6, 153) * mm, "end": v(66.6, 89.4) * mm});
            skLineSegment(sketch, "E318", {"start": v(76.2, 89.4) * mm, "end": v(76.2, 153) * mm});
            skArc(sketch, "E319.filletArc", {"start": v(12.6, 156) * mm, "mid": v(10.48, 155.12) * mm, "end": v(9.6, 153) * mm});
            skArc(sketch, "E320.filletArc", {"start": v(66.6, 153) * mm, "mid": v(65.72, 155.12) * mm, "end": v(63.6, 156) * mm});
            skArc(sketch, "E321.filletArc", {"start": v(63.6, 86.4) * mm, "mid": v(65.72, 87.28) * mm, "end": v(66.6, 89.4) * mm});
            skArc(sketch, "E322.filletArc", {"start": v(9.6, 89.4) * mm, "mid": v(10.48, 87.28) * mm, "end": v(12.6, 86.4) * mm});
            skArc(sketch, "E323.filletArc", {"start": v(79.2, 156) * mm, "mid": v(77.08, 155.12) * mm, "end": v(76.2, 153) * mm});
            skArc(sketch, "E324.filletArc", {"start": v(133.2, 153) * mm, "mid": v(132.32, 155.12) * mm, "end": v(130.2, 156) * mm});
            skArc(sketch, "E325.filletArc", {"start": v(130.2, 86.4) * mm, "mid": v(132.32, 87.28) * mm, "end": v(133.2, 89.4) * mm});
            skArc(sketch, "E326.filletArc", {"start": v(76.2, 89.4) * mm, "mid": v(77.08, 87.28) * mm, "end": v(79.2, 86.4) * mm});
            skArc(sketch, "E327.filletArc", {"start": v(92.4, 73.8) * mm, "mid": v(91.52, 75.92) * mm, "end": v(89.4, 76.8) * mm});
            skArc(sketch, "E328.filletArc", {"start": v(89.4, 9.6) * mm, "mid": v(91.52, 10.48) * mm, "end": v(92.4, 12.6) * mm});
            skArc(sketch, "E329.filletArc", {"start": v(102, 12.6) * mm, "mid": v(102.88, 10.48) * mm, "end": v(105, 9.6) * mm});
            skArc(sketch, "E330.filletArc", {"start": v(105, 76.8) * mm, "mid": v(102.88, 75.92) * mm, "end": v(102, 73.8) * mm});
            skArc(sketch, "E331.filletArc", {"start": v(12.6, 76.8) * mm, "mid": v(10.48, 75.92) * mm, "end": v(9.6, 73.8) * mm});
            skArc(sketch, "E332.filletArc", {"start": v(9.6, 12.6) * mm, "mid": v(10.48, 10.48) * mm, "end": v(12.6, 9.6) * mm});
            skArc(sketch, "E333.filletArc", {"start": v(182.4, 73.8) * mm, "mid": v(181.52, 75.92) * mm, "end": v(179.4, 76.8) * mm});
            skArc(sketch, "E334.filletArc", {"start": v(179.4, 9.6) * mm, "mid": v(181.52, 10.48) * mm, "end": v(182.4, 12.6) * mm});
            skText(sketch, "E335", { "text": "TAVOLE  A", "fontName": "AllertaStencil-Regular.ttf"});
            skText(sketch, "E336", { "text": "TAVOLE  C", "fontName": "AllertaStencil-Regular.ttf"});
            skText(sketch, "E337", { "text": "TAVOLE  B", "fontName": "AllertaStencil-Regular.ttf"});
            skText(sketch, "E338", { "text": "TAVOLE  E", "fontName": "AllertaStencil-Regular.ttf"});
            skText(sketch, "E339", { "text": "TAVOLE  D", "fontName": "AllertaStencil-Regular.ttf"});
            skLineSegment(sketch, "E340", {"start": v(38.1, 158.4) * mm, "end": v(38.1, 156) * mm, "construction": true});
            skLineSegment(sketch, "E341", {"start": v(38.1, 163.2) * mm, "end": v(38.1, 165.6) * mm, "construction": true});
            skLineSegment(sketch, "E342", {"start": v(104.7, 158.4) * mm, "end": v(104.7, 156) * mm, "construction": true});
            skLineSegment(sketch, "E343", {"start": v(104.7, 163.2) * mm, "end": v(104.7, 165.6) * mm, "construction": true});
            skLineSegment(sketch, "E344", {"start": v(142.2, 76.8) * mm, "end": v(142.2, 79.2) * mm, "construction": true});
            skLineSegment(sketch, "E345", {"start": v(124.45, 84) * mm, "end": v(124.45, 86.4) * mm, "construction": true});
            skLineSegment(sketch, "E346", {"start": v(142.2, 7.2) * mm, "end": v(142.2, 9.6) * mm, "construction": true});
            skLineSegment(sketch, "E347", {"start": v(142.2, 2.4) * mm, "end": v(142.2, 0) * mm, "construction": true});
            skLineSegment(sketch, "E348", {"start": v(51, 2.4) * mm, "end": v(51, 0) * mm, "construction": true});
            skLineSegment(sketch, "E349", {"start": v(51, 7.2) * mm, "end": v(51, 9.6) * mm, "construction": true});
            const initialGuessF10  = {"E335": [0.02033, 0.1584, 1, 0, 0.0048], "E336": [0.08728, 0.1584, 1, 0, 0.0048], "E337": [0.03357, 0.0024, 1, 0, 0.0048], "E338": [0.12489, 0.0024, 1, 0, 0.0048], "E339": [0.12445, 0.0792, 1, 0, 0.0048]};
            skSetInitialGuess(sketch, initialGuessF10);
            skSolve(sketch);
        }
        {
            var Q0;
            Q0=makeQuery(id+"F10.imprint","IMPRINT",FACE,{"disambiguationData":[TD([[makeQuery(id+"F10.imprint","IMPRINT",EDGE,{"derivedFrom":sQuery(id+"F10.wireOp",EDGE,"E288.bottom")}),1.0]])]});
            extrude(context, id + "F11", {"entities" : qUnion([Q0]), "depth" : getVariable(context, 'wood_thickness')});
        }
        {
            var Q0;
            Q0=makeQuery(id+"F11.opExtrude","SWEPT_BODY",BODY,{"disambiguationData":[OSD([sQuery(id+"F10.wireOp",EDGE,"E288.bottom"),sQuery(id+"F10.wireOp",EDGE,"E288.top"),sQuery(id+"F10.wireOp",EDGE,"E288.left"),sQuery(id+"F10.wireOp",EDGE,"E288.right"),sQuery(id+"F10.wireOp",EDGE,"E290.filletArc"),sQuery(id+"F10.wireOp",EDGE,"E291.filletArc"),sQuery(id+"F10.wireOp",EDGE,"E292.filletArc"),sQuery(id+"F10.wireOp",EDGE,"E293.filletArc"),sQuery(id+"F10.wireOp",EDGE,"E303"),sQuery(id+"F10.wireOp",EDGE,"E304"),sQuery(id+"F10.wireOp",EDGE,"E305"),sQuery(id+"F10.wireOp",EDGE,"E306"),sQuery(id+"F10.wireOp",EDGE,"E307"),sQuery(id+"F10.wireOp",EDGE,"E308"),sQuery(id+"F10.wireOp",EDGE,"E309"),sQuery(id+"F10.wireOp",EDGE,"E310"),sQuery(id+"F10.wireOp",EDGE,"E311"),sQuery(id+"F10.wireOp",EDGE,"E312"),sQuery(id+"F10.wireOp",EDGE,"E313"),sQuery(id+"F10.wireOp",EDGE,"E314"),sQuery(id+"F10.wireOp",EDGE,"E315"),sQuery(id+"F10.wireOp",EDGE,"E316"),sQuery(id+"F10.wireOp",EDGE,"E317"),sQuery(id+"F10.wireOp",EDGE,"E318"),sQuery(id+"F10.wireOp",EDGE,"E319.filletArc"),sQuery(id+"F10.wireOp",EDGE,"E320.filletArc"),sQuery(id+"F10.wireOp",EDGE,"E321.filletArc"),sQuery(id+"F10.wireOp",EDGE,"E322.filletArc"),sQuery(id+"F10.wireOp",EDGE,"E323.filletArc"),sQuery(id+"F10.wireOp",EDGE,"E324.filletArc"),sQuery(id+"F10.wireOp",EDGE,"E325.filletArc"),sQuery(id+"F10.wireOp",EDGE,"E326.filletArc"),sQuery(id+"F10.wireOp",EDGE,"E327.filletArc"),sQuery(id+"F10.wireOp",EDGE,"E328.filletArc"),sQuery(id+"F10.wireOp",EDGE,"E329.filletArc"),sQuery(id+"F10.wireOp",EDGE,"E330.filletArc"),sQuery(id+"F10.wireOp",EDGE,"E331.filletArc"),sQuery(id+"F10.wireOp",EDGE,"E332.filletArc"),sQuery(id+"F10.wireOp",EDGE,"E333.filletArc"),sQuery(id+"F10.wireOp",EDGE,"E334.filletArc")])]});
            var Q1;
            Q1=makeQuery(id+"F5.opExtrude","SWEPT_BODY",BODY,{"disambiguationData":[OSD([sQuery(id+"F4.wireOp",EDGE,"E88.bottom"),sQuery(id+"F4.wireOp",EDGE,"E88.top"),sQuery(id+"F4.wireOp",EDGE,"E88.left"),sQuery(id+"F4.wireOp",EDGE,"E88.right"),sQuery(id+"F4.wireOp",EDGE,"E92"),sQuery(id+"F4.wireOp",EDGE,"E93"),sQuery(id+"F4.wireOp",EDGE,"E94"),sQuery(id+"F4.wireOp",EDGE,"E95"),sQuery(id+"F4.wireOp",EDGE,"E96"),sQuery(id+"F4.wireOp",EDGE,"E97"),sQuery(id+"F4.wireOp",EDGE,"E99"),sQuery(id+"F4.wireOp",EDGE,"E101"),sQuery(id+"F4.wireOp",EDGE,"E106"),sQuery(id+"F4.wireOp",EDGE,"E111"),sQuery(id+"F4.wireOp",EDGE,"E112"),sQuery(id+"F4.wireOp",EDGE,"E115"),sQuery(id+"F4.wireOp",EDGE,"E116"),sQuery(id+"F4.wireOp",EDGE,"E119"),sQuery(id+"F4.wireOp",EDGE,"E120"),sQuery(id+"F4.wireOp",EDGE,"E123"),sQuery(id+"F4.wireOp",EDGE,"E124"),sQuery(id+"F4.wireOp",EDGE,"E127"),sQuery(id+"F4.wireOp",EDGE,"E128"),sQuery(id+"F4.wireOp",EDGE,"E129"),sQuery(id+"F4.wireOp",EDGE,"E130"),sQuery(id+"F4.wireOp",EDGE,"E131"),sQuery(id+"F4.wireOp",EDGE,"E132"),sQuery(id+"F4.wireOp",EDGE,"E134"),sQuery(id+"F4.wireOp",EDGE,"E136"),sQuery(id+"F4.wireOp",EDGE,"E137"),sQuery(id+"F4.wireOp",EDGE,"E138"),sQuery(id+"F4.wireOp",EDGE,"E139"),sQuery(id+"F4.wireOp",EDGE,"E140"),sQuery(id+"F4.wireOp",EDGE,"E143"),sQuery(id+"F4.wireOp",EDGE,"E145"),sQuery(id+"F4.wireOp",EDGE,"E146")])]});
            var Q2;
            Q2=makeQuery(id+"F7.opExtrude","SWEPT_BODY",BODY,{"disambiguationData":[OSD([sQuery(id+"F6.wireOp",EDGE,"E150.bottom"),sQuery(id+"F6.wireOp",EDGE,"E150.top"),sQuery(id+"F6.wireOp",EDGE,"E150.left"),sQuery(id+"F6.wireOp",EDGE,"E150.right"),sQuery(id+"F6.wireOp",EDGE,"E154"),sQuery(id+"F6.wireOp",EDGE,"E155"),sQuery(id+"F6.wireOp",EDGE,"E156"),sQuery(id+"F6.wireOp",EDGE,"E157"),sQuery(id+"F6.wireOp",EDGE,"E158"),sQuery(id+"F6.wireOp",EDGE,"E159"),sQuery(id+"F6.wireOp",EDGE,"E161"),sQuery(id+"F6.wireOp",EDGE,"E163"),sQuery(id+"F6.wireOp",EDGE,"E168"),sQuery(id+"F6.wireOp",EDGE,"E173"),sQuery(id+"F6.wireOp",EDGE,"E174"),sQuery(id+"F6.wireOp",EDGE,"E177"),sQuery(id+"F6.wireOp",EDGE,"E178"),sQuery(id+"F6.wireOp",EDGE,"E181"),sQuery(id+"F6.wireOp",EDGE,"E182"),sQuery(id+"F6.wireOp",EDGE,"E185"),sQuery(id+"F6.wireOp",EDGE,"E186"),sQuery(id+"F6.wireOp",EDGE,"E189"),sQuery(id+"F6.wireOp",EDGE,"E190"),sQuery(id+"F6.wireOp",EDGE,"E191"),sQuery(id+"F6.wireOp",EDGE,"E192"),sQuery(id+"F6.wireOp",EDGE,"E193"),sQuery(id+"F6.wireOp",EDGE,"E194"),sQuery(id+"F6.wireOp",EDGE,"E196"),sQuery(id+"F6.wireOp",EDGE,"E198"),sQuery(id+"F6.wireOp",EDGE,"E199"),sQuery(id+"F6.wireOp",EDGE,"E200"),sQuery(id+"F6.wireOp",EDGE,"E201"),sQuery(id+"F6.wireOp",EDGE,"E202"),sQuery(id+"F6.wireOp",EDGE,"E205"),sQuery(id+"F6.wireOp",EDGE,"E207"),sQuery(id+"F6.wireOp",EDGE,"E208")])]});
            var Q3;
            Q3=makeQuery(id+"F9.opExtrude","SWEPT_BODY",BODY,{"disambiguationData":[OSD([sQuery(id+"F8.wireOp",EDGE,"E210.bottom"),sQuery(id+"F8.wireOp",EDGE,"E210.top"),sQuery(id+"F8.wireOp",EDGE,"E211"),sQuery(id+"F8.wireOp",EDGE,"E214"),sQuery(id+"F8.wireOp",EDGE,"E215"),sQuery(id+"F8.wireOp",EDGE,"E216"),sQuery(id+"F8.wireOp",EDGE,"E219"),sQuery(id+"F8.wireOp",EDGE,"E220"),sQuery(id+"F8.wireOp",EDGE,"E221"),sQuery(id+"F8.wireOp",EDGE,"E222"),sQuery(id+"F8.wireOp",EDGE,"E223"),sQuery(id+"F8.wireOp",EDGE,"E226"),sQuery(id+"F8.wireOp",EDGE,"E227"),sQuery(id+"F8.wireOp",EDGE,"E228"),sQuery(id+"F8.wireOp",EDGE,"E233"),sQuery(id+"F8.wireOp",EDGE,"E234"),sQuery(id+"F8.wireOp",EDGE,"E237"),sQuery(id+"F8.wireOp",EDGE,"E240"),sQuery(id+"F8.wireOp",EDGE,"E241"),sQuery(id+"F8.wireOp",EDGE,"E242"),sQuery(id+"F8.wireOp",EDGE,"E243"),sQuery(id+"F8.wireOp",EDGE,"E244"),sQuery(id+"F8.wireOp",EDGE,"E245"),sQuery(id+"F8.wireOp",EDGE,"E246"),sQuery(id+"F8.wireOp",EDGE,"E247"),sQuery(id+"F8.wireOp",EDGE,"E248.bottom"),sQuery(id+"F8.wireOp",EDGE,"E248.top"),sQuery(id+"F8.wireOp",EDGE,"E248.left"),sQuery(id+"F8.wireOp",EDGE,"E248.right"),sQuery(id+"F8.wireOp",EDGE,"E249.bottom"),sQuery(id+"F8.wireOp",EDGE,"E249.top"),sQuery(id+"F8.wireOp",EDGE,"E249.left"),sQuery(id+"F8.wireOp",EDGE,"E249.right"),sQuery(id+"F8.wireOp",EDGE,"E250.bottom"),sQuery(id+"F8.wireOp",EDGE,"E250.top"),sQuery(id+"F8.wireOp",EDGE,"E250.left"),sQuery(id+"F8.wireOp",EDGE,"E250.right"),sQuery(id+"F8.wireOp",EDGE,"E251.bottom"),sQuery(id+"F8.wireOp",EDGE,"E251.top"),sQuery(id+"F8.wireOp",EDGE,"E251.left"),sQuery(id+"F8.wireOp",EDGE,"E251.right"),sQuery(id+"F8.wireOp",EDGE,"E254"),sQuery(id+"F8.wireOp",EDGE,"E255"),sQuery(id+"F8.wireOp",EDGE,"E260"),sQuery(id+"F8.wireOp",EDGE,"E263"),sQuery(id+"F8.wireOp",EDGE,"E266"),sQuery(id+"F8.wireOp",EDGE,"E269"),sQuery(id+"F8.wireOp",EDGE,"E272"),sQuery(id+"F8.wireOp",EDGE,"E273"),sQuery(id+"F8.wireOp",EDGE,"E276"),sQuery(id+"F8.wireOp",EDGE,"E277"),sQuery(id+"F8.wireOp",EDGE,"E278"),sQuery(id+"F8.wireOp",EDGE,"E279"),sQuery(id+"F8.wireOp",EDGE,"E280"),sQuery(id+"F8.wireOp",EDGE,"E281"),sQuery(id+"F8.wireOp",EDGE,"E282"),sQuery(id+"F8.wireOp",EDGE,"E283"),sQuery(id+"F8.wireOp",EDGE,"E284"),sQuery(id+"F8.wireOp",EDGE,"E285")])]});
            var Q4;
            Q4=makeQuery(id+"F3.opExtrude","SWEPT_BODY",BODY,{"disambiguationData":[OSD([sQuery(id+"F2.wireOp",EDGE,"E1.bottom"),sQuery(id+"F2.wireOp",EDGE,"E1.top"),sQuery(id+"F2.wireOp",EDGE,"E1.left"),sQuery(id+"F2.wireOp",EDGE,"E1.right"),sQuery(id+"F2.wireOp",EDGE,"E5"),sQuery(id+"F2.wireOp",EDGE,"E6"),sQuery(id+"F2.wireOp",EDGE,"E7"),sQuery(id+"F2.wireOp",EDGE,"E8"),sQuery(id+"F2.wireOp",EDGE,"E9"),sQuery(id+"F2.wireOp",EDGE,"E10"),sQuery(id+"F2.wireOp",EDGE,"E12"),sQuery(id+"F2.wireOp",EDGE,"E14"),sQuery(id+"F2.wireOp",EDGE,"E19"),sQuery(id+"F2.wireOp",EDGE,"E24"),sQuery(id+"F2.wireOp",EDGE,"E25"),sQuery(id+"F2.wireOp",EDGE,"E28"),sQuery(id+"F2.wireOp",EDGE,"E29"),sQuery(id+"F2.wireOp",EDGE,"E32"),sQuery(id+"F2.wireOp",EDGE,"E33"),sQuery(id+"F2.wireOp",EDGE,"E36"),sQuery(id+"F2.wireOp",EDGE,"E37"),sQuery(id+"F2.wireOp",EDGE,"E40"),sQuery(id+"F2.wireOp",EDGE,"E41"),sQuery(id+"F2.wireOp",EDGE,"E44"),sQuery(id+"F2.wireOp",EDGE,"E45"),sQuery(id+"F2.wireOp",EDGE,"E48"),sQuery(id+"F2.wireOp",EDGE,"E49"),sQuery(id+"F2.wireOp",EDGE,"E52"),sQuery(id+"F2.wireOp",EDGE,"E53"),sQuery(id+"F2.wireOp",EDGE,"E56"),sQuery(id+"F2.wireOp",EDGE,"E57"),sQuery(id+"F2.wireOp",EDGE,"E58"),sQuery(id+"F2.wireOp",EDGE,"E59"),sQuery(id+"F2.wireOp",EDGE,"E60"),sQuery(id+"F2.wireOp",EDGE,"E61"),sQuery(id+"F2.wireOp",EDGE,"E62"),sQuery(id+"F2.wireOp",EDGE,"E63"),sQuery(id+"F2.wireOp",EDGE,"E65"),sQuery(id+"F2.wireOp",EDGE,"E67"),sQuery(id+"F2.wireOp",EDGE,"E68"),sQuery(id+"F2.wireOp",EDGE,"E69"),sQuery(id+"F2.wireOp",EDGE,"E70"),sQuery(id+"F2.wireOp",EDGE,"E71"),sQuery(id+"F2.wireOp",EDGE,"E72"),sQuery(id+"F2.wireOp",EDGE,"E73"),sQuery(id+"F2.wireOp",EDGE,"E74"),sQuery(id+"F2.wireOp",EDGE,"E75"),sQuery(id+"F2.wireOp",EDGE,"E77"),sQuery(id+"F2.wireOp",EDGE,"E80"),sQuery(id+"F2.wireOp",EDGE,"E82"),sQuery(id+"F2.wireOp",EDGE,"E84"),sQuery(id+"F2.wireOp",EDGE,"E85")])]});
            booleanBodies(context, id + "F12", {"operationType" : BooleanOperationType.UNION, "tools" : qUnion([Q0, Q1, Q2, Q3, Q4])});
        }
        {
            var Q0;
            Q0=makeQuery(id+"F12.opBoolean","MERGE",FACE,{"derivedFrom":[makeQuery(id+"F3.opExtrude","CAP_FACE",FACE,{"disambiguationData":[OSD([sQuery(id+"F2.wireOp",EDGE,"E1.bottom"),sQuery(id+"F2.wireOp",EDGE,"E1.top"),sQuery(id+"F2.wireOp",EDGE,"E1.left"),sQuery(id+"F2.wireOp",EDGE,"E1.right"),sQuery(id+"F2.wireOp",EDGE,"E5"),sQuery(id+"F2.wireOp",EDGE,"E6"),sQuery(id+"F2.wireOp",EDGE,"E7"),sQuery(id+"F2.wireOp",EDGE,"E8"),sQuery(id+"F2.wireOp",EDGE,"E9"),sQuery(id+"F2.wireOp",EDGE,"E10"),sQuery(id+"F2.wireOp",EDGE,"E12"),sQuery(id+"F2.wireOp",EDGE,"E14"),sQuery(id+"F2.wireOp",EDGE,"E19"),sQuery(id+"F2.wireOp",EDGE,"E24"),sQuery(id+"F2.wireOp",EDGE,"E25"),sQuery(id+"F2.wireOp",EDGE,"E28"),sQuery(id+"F2.wireOp",EDGE,"E29"),sQuery(id+"F2.wireOp",EDGE,"E32"),sQuery(id+"F2.wireOp",EDGE,"E33"),sQuery(id+"F2.wireOp",EDGE,"E36"),sQuery(id+"F2.wireOp",EDGE,"E37"),sQuery(id+"F2.wireOp",EDGE,"E40"),sQuery(id+"F2.wireOp",EDGE,"E41"),sQuery(id+"F2.wireOp",EDGE,"E44"),sQuery(id+"F2.wireOp",EDGE,"E45"),sQuery(id+"F2.wireOp",EDGE,"E48"),sQuery(id+"F2.wireOp",EDGE,"E49"),sQuery(id+"F2.wireOp",EDGE,"E52"),sQuery(id+"F2.wireOp",EDGE,"E53"),sQuery(id+"F2.wireOp",EDGE,"E56"),sQuery(id+"F2.wireOp",EDGE,"E57"),sQuery(id+"F2.wireOp",EDGE,"E58"),sQuery(id+"F2.wireOp",EDGE,"E59"),sQuery(id+"F2.wireOp",EDGE,"E60"),sQuery(id+"F2.wireOp",EDGE,"E61"),sQuery(id+"F2.wireOp",EDGE,"E62"),sQuery(id+"F2.wireOp",EDGE,"E63"),sQuery(id+"F2.wireOp",EDGE,"E65"),sQuery(id+"F2.wireOp",EDGE,"E67"),sQuery(id+"F2.wireOp",EDGE,"E68"),sQuery(id+"F2.wireOp",EDGE,"E69"),sQuery(id+"F2.wireOp",EDGE,"E70"),sQuery(id+"F2.wireOp",EDGE,"E71"),sQuery(id+"F2.wireOp",EDGE,"E72"),sQuery(id+"F2.wireOp",EDGE,"E73"),sQuery(id+"F2.wireOp",EDGE,"E74"),sQuery(id+"F2.wireOp",EDGE,"E75"),sQuery(id+"F2.wireOp",EDGE,"E77"),sQuery(id+"F2.wireOp",EDGE,"E80"),sQuery(id+"F2.wireOp",EDGE,"E82"),sQuery(id+"F2.wireOp",EDGE,"E84"),sQuery(id+"F2.wireOp",EDGE,"E85")])],"isStart":false}),makeQuery(id+"F5.opExtrude","CAP_FACE",FACE,{"disambiguationData":[OSD([sQuery(id+"F4.wireOp",EDGE,"E88.bottom"),sQuery(id+"F4.wireOp",EDGE,"E88.top"),sQuery(id+"F4.wireOp",EDGE,"E88.left"),sQuery(id+"F4.wireOp",EDGE,"E88.right"),sQuery(id+"F4.wireOp",EDGE,"E92"),sQuery(id+"F4.wireOp",EDGE,"E93"),sQuery(id+"F4.wireOp",EDGE,"E94"),sQuery(id+"F4.wireOp",EDGE,"E95"),sQuery(id+"F4.wireOp",EDGE,"E96"),sQuery(id+"F4.wireOp",EDGE,"E97"),sQuery(id+"F4.wireOp",EDGE,"E99"),sQuery(id+"F4.wireOp",EDGE,"E101"),sQuery(id+"F4.wireOp",EDGE,"E106"),sQuery(id+"F4.wireOp",EDGE,"E111"),sQuery(id+"F4.wireOp",EDGE,"E112"),sQuery(id+"F4.wireOp",EDGE,"E115"),sQuery(id+"F4.wireOp",EDGE,"E116"),sQuery(id+"F4.wireOp",EDGE,"E119"),sQuery(id+"F4.wireOp",EDGE,"E120"),sQuery(id+"F4.wireOp",EDGE,"E123"),sQuery(id+"F4.wireOp",EDGE,"E124"),sQuery(id+"F4.wireOp",EDGE,"E127"),sQuery(id+"F4.wireOp",EDGE,"E128"),sQuery(id+"F4.wireOp",EDGE,"E129"),sQuery(id+"F4.wireOp",EDGE,"E130"),sQuery(id+"F4.wireOp",EDGE,"E131"),sQuery(id+"F4.wireOp",EDGE,"E132"),sQuery(id+"F4.wireOp",EDGE,"E134"),sQuery(id+"F4.wireOp",EDGE,"E136"),sQuery(id+"F4.wireOp",EDGE,"E137"),sQuery(id+"F4.wireOp",EDGE,"E138"),sQuery(id+"F4.wireOp",EDGE,"E139"),sQuery(id+"F4.wireOp",EDGE,"E140"),sQuery(id+"F4.wireOp",EDGE,"E143"),sQuery(id+"F4.wireOp",EDGE,"E145"),sQuery(id+"F4.wireOp",EDGE,"E146")])],"isStart":false}),makeQuery(id+"F7.opExtrude","CAP_FACE",FACE,{"disambiguationData":[OSD([sQuery(id+"F6.wireOp",EDGE,"E150.bottom"),sQuery(id+"F6.wireOp",EDGE,"E150.top"),sQuery(id+"F6.wireOp",EDGE,"E150.left"),sQuery(id+"F6.wireOp",EDGE,"E150.right"),sQuery(id+"F6.wireOp",EDGE,"E154"),sQuery(id+"F6.wireOp",EDGE,"E155"),sQuery(id+"F6.wireOp",EDGE,"E156"),sQuery(id+"F6.wireOp",EDGE,"E157"),sQuery(id+"F6.wireOp",EDGE,"E158"),sQuery(id+"F6.wireOp",EDGE,"E159"),sQuery(id+"F6.wireOp",EDGE,"E161"),sQuery(id+"F6.wireOp",EDGE,"E163"),sQuery(id+"F6.wireOp",EDGE,"E168"),sQuery(id+"F6.wireOp",EDGE,"E173"),sQuery(id+"F6.wireOp",EDGE,"E174"),sQuery(id+"F6.wireOp",EDGE,"E177"),sQuery(id+"F6.wireOp",EDGE,"E178"),sQuery(id+"F6.wireOp",EDGE,"E181"),sQuery(id+"F6.wireOp",EDGE,"E182"),sQuery(id+"F6.wireOp",EDGE,"E185"),sQuery(id+"F6.wireOp",EDGE,"E186"),sQuery(id+"F6.wireOp",EDGE,"E189"),sQuery(id+"F6.wireOp",EDGE,"E190"),sQuery(id+"F6.wireOp",EDGE,"E191"),sQuery(id+"F6.wireOp",EDGE,"E192"),sQuery(id+"F6.wireOp",EDGE,"E193"),sQuery(id+"F6.wireOp",EDGE,"E194"),sQuery(id+"F6.wireOp",EDGE,"E196"),sQuery(id+"F6.wireOp",EDGE,"E198"),sQuery(id+"F6.wireOp",EDGE,"E199"),sQuery(id+"F6.wireOp",EDGE,"E200"),sQuery(id+"F6.wireOp",EDGE,"E201"),sQuery(id+"F6.wireOp",EDGE,"E202"),sQuery(id+"F6.wireOp",EDGE,"E205"),sQuery(id+"F6.wireOp",EDGE,"E207"),sQuery(id+"F6.wireOp",EDGE,"E208")])],"isStart":false}),makeQuery(id+"F9.opExtrude","CAP_FACE",FACE,{"disambiguationData":[OSD([sQuery(id+"F8.wireOp",EDGE,"E210.bottom"),sQuery(id+"F8.wireOp",EDGE,"E210.top"),sQuery(id+"F8.wireOp",EDGE,"E211"),sQuery(id+"F8.wireOp",EDGE,"E214"),sQuery(id+"F8.wireOp",EDGE,"E215"),sQuery(id+"F8.wireOp",EDGE,"E216"),sQuery(id+"F8.wireOp",EDGE,"E219"),sQuery(id+"F8.wireOp",EDGE,"E220"),sQuery(id+"F8.wireOp",EDGE,"E221"),sQuery(id+"F8.wireOp",EDGE,"E222"),sQuery(id+"F8.wireOp",EDGE,"E223"),sQuery(id+"F8.wireOp",EDGE,"E226"),sQuery(id+"F8.wireOp",EDGE,"E227"),sQuery(id+"F8.wireOp",EDGE,"E228"),sQuery(id+"F8.wireOp",EDGE,"E233"),sQuery(id+"F8.wireOp",EDGE,"E234"),sQuery(id+"F8.wireOp",EDGE,"E237"),sQuery(id+"F8.wireOp",EDGE,"E240"),sQuery(id+"F8.wireOp",EDGE,"E241"),sQuery(id+"F8.wireOp",EDGE,"E242"),sQuery(id+"F8.wireOp",EDGE,"E243"),sQuery(id+"F8.wireOp",EDGE,"E244"),sQuery(id+"F8.wireOp",EDGE,"E245"),sQuery(id+"F8.wireOp",EDGE,"E246"),sQuery(id+"F8.wireOp",EDGE,"E247"),sQuery(id+"F8.wireOp",EDGE,"E248.bottom"),sQuery(id+"F8.wireOp",EDGE,"E248.top"),sQuery(id+"F8.wireOp",EDGE,"E248.left"),sQuery(id+"F8.wireOp",EDGE,"E248.right"),sQuery(id+"F8.wireOp",EDGE,"E249.bottom"),sQuery(id+"F8.wireOp",EDGE,"E249.top"),sQuery(id+"F8.wireOp",EDGE,"E249.left"),sQuery(id+"F8.wireOp",EDGE,"E249.right"),sQuery(id+"F8.wireOp",EDGE,"E250.bottom"),sQuery(id+"F8.wireOp",EDGE,"E250.top"),sQuery(id+"F8.wireOp",EDGE,"E250.left"),sQuery(id+"F8.wireOp",EDGE,"E250.right"),sQuery(id+"F8.wireOp",EDGE,"E251.bottom"),sQuery(id+"F8.wireOp",EDGE,"E251.top"),sQuery(id+"F8.wireOp",EDGE,"E251.left"),sQuery(id+"F8.wireOp",EDGE,"E251.right"),sQuery(id+"F8.wireOp",EDGE,"E254"),sQuery(id+"F8.wireOp",EDGE,"E255"),sQuery(id+"F8.wireOp",EDGE,"E260"),sQuery(id+"F8.wireOp",EDGE,"E263"),sQuery(id+"F8.wireOp",EDGE,"E266"),sQuery(id+"F8.wireOp",EDGE,"E269"),sQuery(id+"F8.wireOp",EDGE,"E272"),sQuery(id+"F8.wireOp",EDGE,"E273"),sQuery(id+"F8.wireOp",EDGE,"E276"),sQuery(id+"F8.wireOp",EDGE,"E277"),sQuery(id+"F8.wireOp",EDGE,"E278"),sQuery(id+"F8.wireOp",EDGE,"E279"),sQuery(id+"F8.wireOp",EDGE,"E280"),sQuery(id+"F8.wireOp",EDGE,"E281"),sQuery(id+"F8.wireOp",EDGE,"E282"),sQuery(id+"F8.wireOp",EDGE,"E283"),sQuery(id+"F8.wireOp",EDGE,"E284"),sQuery(id+"F8.wireOp",EDGE,"E285")])],"isStart":false}),makeQuery(id+"F11.opExtrude","CAP_FACE",FACE,{"disambiguationData":[OSD([sQuery(id+"F10.wireOp",EDGE,"E288.bottom"),sQuery(id+"F10.wireOp",EDGE,"E288.top"),sQuery(id+"F10.wireOp",EDGE,"E288.left"),sQuery(id+"F10.wireOp",EDGE,"E288.right"),sQuery(id+"F10.wireOp",EDGE,"E290.filletArc"),sQuery(id+"F10.wireOp",EDGE,"E291.filletArc"),sQuery(id+"F10.wireOp",EDGE,"E292.filletArc"),sQuery(id+"F10.wireOp",EDGE,"E293.filletArc"),sQuery(id+"F10.wireOp",EDGE,"E303"),sQuery(id+"F10.wireOp",EDGE,"E304"),sQuery(id+"F10.wireOp",EDGE,"E305"),sQuery(id+"F10.wireOp",EDGE,"E306"),sQuery(id+"F10.wireOp",EDGE,"E307"),sQuery(id+"F10.wireOp",EDGE,"E308"),sQuery(id+"F10.wireOp",EDGE,"E309"),sQuery(id+"F10.wireOp",EDGE,"E310"),sQuery(id+"F10.wireOp",EDGE,"E311"),sQuery(id+"F10.wireOp",EDGE,"E312"),sQuery(id+"F10.wireOp",EDGE,"E313"),sQuery(id+"F10.wireOp",EDGE,"E314"),sQuery(id+"F10.wireOp",EDGE,"E315"),sQuery(id+"F10.wireOp",EDGE,"E316"),sQuery(id+"F10.wireOp",EDGE,"E317"),sQuery(id+"F10.wireOp",EDGE,"E318"),sQuery(id+"F10.wireOp",EDGE,"E319.filletArc"),sQuery(id+"F10.wireOp",EDGE,"E320.filletArc"),sQuery(id+"F10.wireOp",EDGE,"E321.filletArc"),sQuery(id+"F10.wireOp",EDGE,"E322.filletArc"),sQuery(id+"F10.wireOp",EDGE,"E323.filletArc"),sQuery(id+"F10.wireOp",EDGE,"E324.filletArc"),sQuery(id+"F10.wireOp",EDGE,"E325.filletArc"),sQuery(id+"F10.wireOp",EDGE,"E326.filletArc"),sQuery(id+"F10.wireOp",EDGE,"E327.filletArc"),sQuery(id+"F10.wireOp",EDGE,"E328.filletArc"),sQuery(id+"F10.wireOp",EDGE,"E329.filletArc"),sQuery(id+"F10.wireOp",EDGE,"E330.filletArc"),sQuery(id+"F10.wireOp",EDGE,"E331.filletArc"),sQuery(id+"F10.wireOp",EDGE,"E332.filletArc"),sQuery(id+"F10.wireOp",EDGE,"E333.filletArc"),sQuery(id+"F10.wireOp",EDGE,"E334.filletArc"),sQuery(id+"F10.wireOp",EDGE,"E335.sketch_text.stroke-0"),sQuery(id+"F10.wireOp",EDGE,"E335.sketch_text.stroke-1"),sQuery(id+"F10.wireOp",EDGE,"E335.sketch_text.stroke-2"),sQuery(id+"F10.wireOp",EDGE,"E335.sketch_text.stroke-3"),sQuery(id+"F10.wireOp",EDGE,"E335.sketch_text.stroke-4"),sQuery(id+"F10.wireOp",EDGE,"E335.sketch_text.stroke-5"),sQuery(id+"F10.wireOp",EDGE,"E335.sketch_text.stroke-6"),sQuery(id+"F10.wireOp",EDGE,"E335.sketch_text.stroke-7"),sQuery(id+"F10.wireOp",EDGE,"E335.sketch_text.stroke-8"),sQuery(id+"F10.wireOp",EDGE,"E335.sketch_text.stroke-9"),sQuery(id+"F10.wireOp",EDGE,"E335.sketch_text.stroke-10"),sQuery(id+"F10.wireOp",EDGE,"E335.sketch_text.stroke-11"),sQuery(id+"F10.wireOp",EDGE,"E335.sketch_text.stroke-12"),sQuery(id+"F10.wireOp",EDGE,"E335.sketch_text.stroke-13"),sQuery(id+"F10.wireOp",EDGE,"E335.sketch_text.stroke-14"),sQuery(id+"F10.wireOp",EDGE,"E335.sketch_text.stroke-15"),sQuery(id+"F10.wireOp",EDGE,"E335.sketch_text.stroke-16"),sQuery(id+"F10.wireOp",EDGE,"E335.sketch_text.stroke-17"),sQuery(id+"F10.wireOp",EDGE,"E335.sketch_text.stroke-18"),sQuery(id+"F10.wireOp",EDGE,"E335.sketch_text.stroke-19"),sQuery(id+"F10.wireOp",EDGE,"E335.sketch_text.stroke-20"),sQuery(id+"F10.wireOp",EDGE,"E335.sketch_text.stroke-21"),sQuery(id+"F10.wireOp",EDGE,"E335.sketch_text.stroke-22"),sQuery(id+"F10.wireOp",EDGE,"E335.sketch_text.stroke-23"),sQuery(id+"F10.wireOp",EDGE,"E335.sketch_text.stroke-24"),sQuery(id+"F10.wireOp",EDGE,"E335.sketch_text.stroke-25"),sQuery(id+"F10.wireOp",EDGE,"E335.sketch_text.stroke-26"),sQuery(id+"F10.wireOp",EDGE,"E335.sketch_text.stroke-27"),sQuery(id+"F10.wireOp",EDGE,"E335.sketch_text.stroke-28"),sQuery(id+"F10.wireOp",EDGE,"E335.sketch_text.stroke-29"),sQuery(id+"F10.wireOp",EDGE,"E335.sketch_text.stroke-30"),sQuery(id+"F10.wireOp",EDGE,"E335.sketch_text.stroke-31"),sQuery(id+"F10.wireOp",EDGE,"E335.sketch_text.stroke-32"),sQuery(id+"F10.wireOp",EDGE,"E335.sketch_text.stroke-33"),sQuery(id+"F10.wireOp",EDGE,"E335.sketch_text.stroke-34"),sQuery(id+"F10.wireOp",EDGE,"E335.sketch_text.stroke-35"),sQuery(id+"F10.wireOp",EDGE,"E335.sketch_text.stroke-36"),sQuery(id+"F10.wireOp",EDGE,"E335.sketch_text.stroke-37"),sQuery(id+"F10.wireOp",EDGE,"E335.sketch_text.stroke-38"),sQuery(id+"F10.wireOp",EDGE,"E335.sketch_text.stroke-39"),sQuery(id+"F10.wireOp",EDGE,"E335.sketch_text.stroke-40"),sQuery(id+"F10.wireOp",EDGE,"E335.sketch_text.stroke-41"),sQuery(id+"F10.wireOp",EDGE,"E335.sketch_text.stroke-42"),sQuery(id+"F10.wireOp",EDGE,"E335.sketch_text.stroke-43"),sQuery(id+"F10.wireOp",EDGE,"E335.sketch_text.stroke-44"),sQuery(id+"F10.wireOp",EDGE,"E335.sketch_text.stroke-45"),sQuery(id+"F10.wireOp",EDGE,"E335.sketch_text.stroke-46"),sQuery(id+"F10.wireOp",EDGE,"E335.sketch_text.stroke-47"),sQuery(id+"F10.wireOp",EDGE,"E335.sketch_text.stroke-48"),sQuery(id+"F10.wireOp",EDGE,"E335.sketch_text.stroke-49"),sQuery(id+"F10.wireOp",EDGE,"E335.sketch_text.stroke-50"),sQuery(id+"F10.wireOp",EDGE,"E335.sketch_text.stroke-51"),sQuery(id+"F10.wireOp",EDGE,"E335.sketch_text.stroke-52"),sQuery(id+"F10.wireOp",EDGE,"E335.sketch_text.stroke-53"),sQuery(id+"F10.wireOp",EDGE,"E335.sketch_text.stroke-54"),sQuery(id+"F10.wireOp",EDGE,"E335.sketch_text.stroke-55"),sQuery(id+"F10.wireOp",EDGE,"E335.sketch_text.stroke-56"),sQuery(id+"F10.wireOp",EDGE,"E335.sketch_text.stroke-57"),sQuery(id+"F10.wireOp",EDGE,"E335.sketch_text.stroke-58"),sQuery(id+"F10.wireOp",EDGE,"E335.sketch_text.stroke-59"),sQuery(id+"F10.wireOp",EDGE,"E335.sketch_text.stroke-60"),sQuery(id+"F10.wireOp",EDGE,"E335.sketch_text.stroke-61"),sQuery(id+"F10.wireOp",EDGE,"E335.sketch_text.stroke-62"),sQuery(id+"F10.wireOp",EDGE,"E335.sketch_text.stroke-63"),sQuery(id+"F10.wireOp",EDGE,"E335.sketch_text.stroke-64"),sQuery(id+"F10.wireOp",EDGE,"E335.sketch_text.stroke-65"),sQuery(id+"F10.wireOp",EDGE,"E335.sketch_text.stroke-66"),sQuery(id+"F10.wireOp",EDGE,"E335.sketch_text.stroke-67"),sQuery(id+"F10.wireOp",EDGE,"E335.sketch_text.stroke-68"),sQuery(id+"F10.wireOp",EDGE,"E335.sketch_text.stroke-69"),sQuery(id+"F10.wireOp",EDGE,"E335.sketch_text.stroke-70"),sQuery(id+"F10.wireOp",EDGE,"E335.sketch_text.stroke-71"),sQuery(id+"F10.wireOp",EDGE,"E335.sketch_text.stroke-72"),sQuery(id+"F10.wireOp",EDGE,"E335.sketch_text.stroke-73"),sQuery(id+"F10.wireOp",EDGE,"E335.sketch_text.stroke-74"),sQuery(id+"F10.wireOp",EDGE,"E335.sketch_text.stroke-75"),sQuery(id+"F10.wireOp",EDGE,"E335.sketch_text.stroke-76"),sQuery(id+"F10.wireOp",EDGE,"E335.sketch_text.stroke-77"),sQuery(id+"F10.wireOp",EDGE,"E335.sketch_text.stroke-78"),sQuery(id+"F10.wireOp",EDGE,"E335.sketch_text.stroke-79"),sQuery(id+"F10.wireOp",EDGE,"E335.sketch_text.stroke-80"),sQuery(id+"F10.wireOp",EDGE,"E335.sketch_text.stroke-81"),sQuery(id+"F10.wireOp",EDGE,"E335.sketch_text.stroke-82"),sQuery(id+"F10.wireOp",EDGE,"E335.sketch_text.stroke-83"),sQuery(id+"F10.wireOp",EDGE,"E335.sketch_text.stroke-84"),sQuery(id+"F10.wireOp",EDGE,"E335.sketch_text.stroke-85"),sQuery(id+"F10.wireOp",EDGE,"E335.sketch_text.stroke-86"),sQuery(id+"F10.wireOp",EDGE,"E335.sketch_text.stroke-87"),sQuery(id+"F10.wireOp",EDGE,"E335.sketch_text.stroke-88"),sQuery(id+"F10.wireOp",EDGE,"E335.sketch_text.stroke-89"),sQuery(id+"F10.wireOp",EDGE,"E335.sketch_text.stroke-90"),sQuery(id+"F10.wireOp",EDGE,"E335.sketch_text.stroke-91"),sQuery(id+"F10.wireOp",EDGE,"E335.sketch_text.stroke-92"),sQuery(id+"F10.wireOp",EDGE,"E335.sketch_text.stroke-93"),sQuery(id+"F10.wireOp",EDGE,"E335.sketch_text.stroke-94"),sQuery(id+"F10.wireOp",EDGE,"E335.sketch_text.stroke-95"),sQuery(id+"F10.wireOp",EDGE,"E335.sketch_text.stroke-96"),sQuery(id+"F10.wireOp",EDGE,"E335.sketch_text.stroke-97"),sQuery(id+"F10.wireOp",EDGE,"E336.sketch_text.stroke-0"),sQuery(id+"F10.wireOp",EDGE,"E336.sketch_text.stroke-1"),sQuery(id+"F10.wireOp",EDGE,"E336.sketch_text.stroke-2"),sQuery(id+"F10.wireOp",EDGE,"E336.sketch_text.stroke-3"),sQuery(id+"F10.wireOp",EDGE,"E336.sketch_text.stroke-4"),sQuery(id+"F10.wireOp",EDGE,"E336.sketch_text.stroke-5"),sQuery(id+"F10.wireOp",EDGE,"E336.sketch_text.stroke-6"),sQuery(id+"F10.wireOp",EDGE,"E336.sketch_text.stroke-7"),sQuery(id+"F10.wireOp",EDGE,"E336.sketch_text.stroke-8"),sQuery(id+"F10.wireOp",EDGE,"E336.sketch_text.stroke-9"),sQuery(id+"F10.wireOp",EDGE,"E336.sketch_text.stroke-10"),sQuery(id+"F10.wireOp",EDGE,"E336.sketch_text.stroke-11"),sQuery(id+"F10.wireOp",EDGE,"E336.sketch_text.stroke-12"),sQuery(id+"F10.wireOp",EDGE,"E336.sketch_text.stroke-13"),sQuery(id+"F10.wireOp",EDGE,"E336.sketch_text.stroke-14"),sQuery(id+"F10.wireOp",EDGE,"E336.sketch_text.stroke-15"),sQuery(id+"F10.wireOp",EDGE,"E336.sketch_text.stroke-16"),sQuery(id+"F10.wireOp",EDGE,"E336.sketch_text.stroke-17"),sQuery(id+"F10.wireOp",EDGE,"E336.sketch_text.stroke-18"),sQuery(id+"F10.wireOp",EDGE,"E336.sketch_text.stroke-19"),sQuery(id+"F10.wireOp",EDGE,"E336.sketch_text.stroke-20"),sQuery(id+"F10.wireOp",EDGE,"E336.sketch_text.stroke-21"),sQuery(id+"F10.wireOp",EDGE,"E336.sketch_text.stroke-22"),sQuery(id+"F10.wireOp",EDGE,"E336.sketch_text.stroke-23"),sQuery(id+"F10.wireOp",EDGE,"E336.sketch_text.stroke-24"),sQuery(id+"F10.wireOp",EDGE,"E336.sketch_text.stroke-25"),sQuery(id+"F10.wireOp",EDGE,"E336.sketch_text.stroke-26"),sQuery(id+"F10.wireOp",EDGE,"E336.sketch_text.stroke-27"),sQuery(id+"F10.wireOp",EDGE,"E336.sketch_text.stroke-28"),sQuery(id+"F10.wireOp",EDGE,"E336.sketch_text.stroke-29"),sQuery(id+"F10.wireOp",EDGE,"E336.sketch_text.stroke-30"),sQuery(id+"F10.wireOp",EDGE,"E336.sketch_text.stroke-31"),sQuery(id+"F10.wireOp",EDGE,"E336.sketch_text.stroke-32"),sQuery(id+"F10.wireOp",EDGE,"E336.sketch_text.stroke-33"),sQuery(id+"F10.wireOp",EDGE,"E336.sketch_text.stroke-34"),sQuery(id+"F10.wireOp",EDGE,"E336.sketch_text.stroke-35"),sQuery(id+"F10.wireOp",EDGE,"E336.sketch_text.stroke-36"),sQuery(id+"F10.wireOp",EDGE,"E336.sketch_text.stroke-37"),sQuery(id+"F10.wireOp",EDGE,"E336.sketch_text.stroke-38"),sQuery(id+"F10.wireOp",EDGE,"E336.sketch_text.stroke-39"),sQuery(id+"F10.wireOp",EDGE,"E336.sketch_text.stroke-40"),sQuery(id+"F10.wireOp",EDGE,"E336.sketch_text.stroke-41"),sQuery(id+"F10.wireOp",EDGE,"E336.sketch_text.stroke-42"),sQuery(id+"F10.wireOp",EDGE,"E336.sketch_text.stroke-43"),sQuery(id+"F10.wireOp",EDGE,"E336.sketch_text.stroke-44"),sQuery(id+"F10.wireOp",EDGE,"E336.sketch_text.stroke-45"),sQuery(id+"F10.wireOp",EDGE,"E336.sketch_text.stroke-46"),sQuery(id+"F10.wireOp",EDGE,"E336.sketch_text.stroke-47"),sQuery(id+"F10.wireOp",EDGE,"E336.sketch_text.stroke-48"),sQuery(id+"F10.wireOp",EDGE,"E336.sketch_text.stroke-49"),sQuery(id+"F10.wireOp",EDGE,"E336.sketch_text.stroke-50"),sQuery(id+"F10.wireOp",EDGE,"E336.sketch_text.stroke-51"),sQuery(id+"F10.wireOp",EDGE,"E336.sketch_text.stroke-52"),sQuery(id+"F10.wireOp",EDGE,"E336.sketch_text.stroke-53"),sQuery(id+"F10.wireOp",EDGE,"E336.sketch_text.stroke-54"),sQuery(id+"F10.wireOp",EDGE,"E336.sketch_text.stroke-55"),sQuery(id+"F10.wireOp",EDGE,"E336.sketch_text.stroke-56"),sQuery(id+"F10.wireOp",EDGE,"E336.sketch_text.stroke-57"),sQuery(id+"F10.wireOp",EDGE,"E336.sketch_text.stroke-58"),sQuery(id+"F10.wireOp",EDGE,"E336.sketch_text.stroke-59"),sQuery(id+"F10.wireOp",EDGE,"E336.sketch_text.stroke-60"),sQuery(id+"F10.wireOp",EDGE,"E336.sketch_text.stroke-61"),sQuery(id+"F10.wireOp",EDGE,"E336.sketch_text.stroke-62"),sQuery(id+"F10.wireOp",EDGE,"E336.sketch_text.stroke-63"),sQuery(id+"F10.wireOp",EDGE,"E336.sketch_text.stroke-64"),sQuery(id+"F10.wireOp",EDGE,"E336.sketch_text.stroke-65"),sQuery(id+"F10.wireOp",EDGE,"E336.sketch_text.stroke-66"),sQuery(id+"F10.wireOp",EDGE,"E336.sketch_text.stroke-67"),sQuery(id+"F10.wireOp",EDGE,"E336.sketch_text.stroke-68"),sQuery(id+"F10.wireOp",EDGE,"E336.sketch_text.stroke-69"),sQuery(id+"F10.wireOp",EDGE,"E336.sketch_text.stroke-70"),sQuery(id+"F10.wireOp",EDGE,"E336.sketch_text.stroke-71"),sQuery(id+"F10.wireOp",EDGE,"E336.sketch_text.stroke-72"),sQuery(id+"F10.wireOp",EDGE,"E336.sketch_text.stroke-73"),sQuery(id+"F10.wireOp",EDGE,"E336.sketch_text.stroke-74"),sQuery(id+"F10.wireOp",EDGE,"E336.sketch_text.stroke-75"),sQuery(id+"F10.wireOp",EDGE,"E336.sketch_text.stroke-76"),sQuery(id+"F10.wireOp",EDGE,"E336.sketch_text.stroke-77"),sQuery(id+"F10.wireOp",EDGE,"E336.sketch_text.stroke-78"),sQuery(id+"F10.wireOp",EDGE,"E336.sketch_text.stroke-79"),sQuery(id+"F10.wireOp",EDGE,"E336.sketch_text.stroke-80"),sQuery(id+"F10.wireOp",EDGE,"E336.sketch_text.stroke-81"),sQuery(id+"F10.wireOp",EDGE,"E336.sketch_text.stroke-82"),sQuery(id+"F10.wireOp",EDGE,"E336.sketch_text.stroke-83"),sQuery(id+"F10.wireOp",EDGE,"E336.sketch_text.stroke-84"),sQuery(id+"F10.wireOp",EDGE,"E336.sketch_text.stroke-85"),sQuery(id+"F10.wireOp",EDGE,"E336.sketch_text.stroke-86"),sQuery(id+"F10.wireOp",EDGE,"E336.sketch_text.stroke-87"),sQuery(id+"F10.wireOp",EDGE,"E336.sketch_text.stroke-88"),sQuery(id+"F10.wireOp",EDGE,"E336.sketch_text.stroke-89"),sQuery(id+"F10.wireOp",EDGE,"E336.sketch_text.stroke-90"),sQuery(id+"F10.wireOp",EDGE,"E336.sketch_text.stroke-91"),sQuery(id+"F10.wireOp",EDGE,"E336.sketch_text.stroke-92"),sQuery(id+"F10.wireOp",EDGE,"E336.sketch_text.stroke-93"),sQuery(id+"F10.wireOp",EDGE,"E336.sketch_text.stroke-94"),sQuery(id+"F10.wireOp",EDGE,"E336.sketch_text.stroke-95"),sQuery(id+"F10.wireOp",EDGE,"E336.sketch_text.stroke-96"),sQuery(id+"F10.wireOp",EDGE,"E336.sketch_text.stroke-97"),sQuery(id+"F10.wireOp",EDGE,"E336.sketch_text.stroke-98"),sQuery(id+"F10.wireOp",EDGE,"E336.sketch_text.stroke-99"),sQuery(id+"F10.wireOp",EDGE,"E336.sketch_text.stroke-100"),sQuery(id+"F10.wireOp",EDGE,"E336.sketch_text.stroke-101"),sQuery(id+"F10.wireOp",EDGE,"E336.sketch_text.stroke-102"),sQuery(id+"F10.wireOp",EDGE,"E336.sketch_text.stroke-103"),sQuery(id+"F10.wireOp",EDGE,"E336.sketch_text.stroke-104"),sQuery(id+"F10.wireOp",EDGE,"E336.sketch_text.stroke-105"),sQuery(id+"F10.wireOp",EDGE,"E336.sketch_text.stroke-106"),sQuery(id+"F10.wireOp",EDGE,"E336.sketch_text.stroke-107"),sQuery(id+"F10.wireOp",EDGE,"E336.sketch_text.stroke-108"),sQuery(id+"F10.wireOp",EDGE,"E336.sketch_text.stroke-109"),sQuery(id+"F10.wireOp",EDGE,"E336.sketch_text.stroke-110"),sQuery(id+"F10.wireOp",EDGE,"E336.sketch_text.stroke-111"),sQuery(id+"F10.wireOp",EDGE,"E336.sketch_text.stroke-112"),sQuery(id+"F10.wireOp",EDGE,"E336.sketch_text.stroke-113"),sQuery(id+"F10.wireOp",EDGE,"E336.sketch_text.stroke-114"),sQuery(id+"F10.wireOp",EDGE,"E336.sketch_text.stroke-115"),sQuery(id+"F10.wireOp",EDGE,"E337.sketch_text.stroke-0"),sQuery(id+"F10.wireOp",EDGE,"E337.sketch_text.stroke-1"),sQuery(id+"F10.wireOp",EDGE,"E337.sketch_text.stroke-2"),sQuery(id+"F10.wireOp",EDGE,"E337.sketch_text.stroke-3"),sQuery(id+"F10.wireOp",EDGE,"E337.sketch_text.stroke-4"),sQuery(id+"F10.wireOp",EDGE,"E337.sketch_text.stroke-5"),sQuery(id+"F10.wireOp",EDGE,"E337.sketch_text.stroke-6"),sQuery(id+"F10.wireOp",EDGE,"E337.sketch_text.stroke-7"),sQuery(id+"F10.wireOp",EDGE,"E337.sketch_text.stroke-8"),sQuery(id+"F10.wireOp",EDGE,"E337.sketch_text.stroke-9"),sQuery(id+"F10.wireOp",EDGE,"E337.sketch_text.stroke-10"),sQuery(id+"F10.wireOp",EDGE,"E337.sketch_text.stroke-11"),sQuery(id+"F10.wireOp",EDGE,"E337.sketch_text.stroke-12"),sQuery(id+"F10.wireOp",EDGE,"E337.sketch_text.stroke-13"),sQuery(id+"F10.wireOp",EDGE,"E337.sketch_text.stroke-14"),sQuery(id+"F10.wireOp",EDGE,"E337.sketch_text.stroke-15"),sQuery(id+"F10.wireOp",EDGE,"E337.sketch_text.stroke-16"),sQuery(id+"F10.wireOp",EDGE,"E337.sketch_text.stroke-17"),sQuery(id+"F10.wireOp",EDGE,"E337.sketch_text.stroke-18"),sQuery(id+"F10.wireOp",EDGE,"E337.sketch_text.stroke-19"),sQuery(id+"F10.wireOp",EDGE,"E337.sketch_text.stroke-20"),sQuery(id+"F10.wireOp",EDGE,"E337.sketch_text.stroke-21"),sQuery(id+"F10.wireOp",EDGE,"E337.sketch_text.stroke-22"),sQuery(id+"F10.wireOp",EDGE,"E337.sketch_text.stroke-23"),sQuery(id+"F10.wireOp",EDGE,"E337.sketch_text.stroke-24"),sQuery(id+"F10.wireOp",EDGE,"E337.sketch_text.stroke-25"),sQuery(id+"F10.wireOp",EDGE,"E337.sketch_text.stroke-26"),sQuery(id+"F10.wireOp",EDGE,"E337.sketch_text.stroke-27"),sQuery(id+"F10.wireOp",EDGE,"E337.sketch_text.stroke-28"),sQuery(id+"F10.wireOp",EDGE,"E337.sketch_text.stroke-29"),sQuery(id+"F10.wireOp",EDGE,"E337.sketch_text.stroke-30"),sQuery(id+"F10.wireOp",EDGE,"E337.sketch_text.stroke-31"),sQuery(id+"F10.wireOp",EDGE,"E337.sketch_text.stroke-32"),sQuery(id+"F10.wireOp",EDGE,"E337.sketch_text.stroke-33"),sQuery(id+"F10.wireOp",EDGE,"E337.sketch_text.stroke-34"),sQuery(id+"F10.wireOp",EDGE,"E337.sketch_text.stroke-35"),sQuery(id+"F10.wireOp",EDGE,"E337.sketch_text.stroke-36"),sQuery(id+"F10.wireOp",EDGE,"E337.sketch_text.stroke-37"),sQuery(id+"F10.wireOp",EDGE,"E337.sketch_text.stroke-38"),sQuery(id+"F10.wireOp",EDGE,"E337.sketch_text.stroke-39"),sQuery(id+"F10.wireOp",EDGE,"E337.sketch_text.stroke-40"),sQuery(id+"F10.wireOp",EDGE,"E337.sketch_text.stroke-41"),sQuery(id+"F10.wireOp",EDGE,"E337.sketch_text.stroke-42"),sQuery(id+"F10.wireOp",EDGE,"E337.sketch_text.stroke-43"),sQuery(id+"F10.wireOp",EDGE,"E337.sketch_text.stroke-44"),sQuery(id+"F10.wireOp",EDGE,"E337.sketch_text.stroke-45"),sQuery(id+"F10.wireOp",EDGE,"E337.sketch_text.stroke-46"),sQuery(id+"F10.wireOp",EDGE,"E337.sketch_text.stroke-47"),sQuery(id+"F10.wireOp",EDGE,"E337.sketch_text.stroke-48"),sQuery(id+"F10.wireOp",EDGE,"E337.sketch_text.stroke-49"),sQuery(id+"F10.wireOp",EDGE,"E337.sketch_text.stroke-50"),sQuery(id+"F10.wireOp",EDGE,"E337.sketch_text.stroke-51"),sQuery(id+"F10.wireOp",EDGE,"E337.sketch_text.stroke-52"),sQuery(id+"F10.wireOp",EDGE,"E337.sketch_text.stroke-53"),sQuery(id+"F10.wireOp",EDGE,"E337.sketch_text.stroke-54"),sQuery(id+"F10.wireOp",EDGE,"E337.sketch_text.stroke-55"),sQuery(id+"F10.wireOp",EDGE,"E337.sketch_text.stroke-56"),sQuery(id+"F10.wireOp",EDGE,"E337.sketch_text.stroke-57"),sQuery(id+"F10.wireOp",EDGE,"E337.sketch_text.stroke-58"),sQuery(id+"F10.wireOp",EDGE,"E337.sketch_text.stroke-59"),sQuery(id+"F10.wireOp",EDGE,"E337.sketch_text.stroke-60"),sQuery(id+"F10.wireOp",EDGE,"E337.sketch_text.stroke-61"),sQuery(id+"F10.wireOp",EDGE,"E337.sketch_text.stroke-62"),sQuery(id+"F10.wireOp",EDGE,"E337.sketch_text.stroke-63"),sQuery(id+"F10.wireOp",EDGE,"E337.sketch_text.stroke-64"),sQuery(id+"F10.wireOp",EDGE,"E337.sketch_text.stroke-65"),sQuery(id+"F10.wireOp",EDGE,"E337.sketch_text.stroke-66"),sQuery(id+"F10.wireOp",EDGE,"E337.sketch_text.stroke-67"),sQuery(id+"F10.wireOp",EDGE,"E337.sketch_text.stroke-68"),sQuery(id+"F10.wireOp",EDGE,"E337.sketch_text.stroke-69"),sQuery(id+"F10.wireOp",EDGE,"E337.sketch_text.stroke-70"),sQuery(id+"F10.wireOp",EDGE,"E337.sketch_text.stroke-71"),sQuery(id+"F10.wireOp",EDGE,"E337.sketch_text.stroke-72"),sQuery(id+"F10.wireOp",EDGE,"E337.sketch_text.stroke-73"),sQuery(id+"F10.wireOp",EDGE,"E337.sketch_text.stroke-74"),sQuery(id+"F10.wireOp",EDGE,"E337.sketch_text.stroke-75"),sQuery(id+"F10.wireOp",EDGE,"E337.sketch_text.stroke-76"),sQuery(id+"F10.wireOp",EDGE,"E337.sketch_text.stroke-77"),sQuery(id+"F10.wireOp",EDGE,"E337.sketch_text.stroke-78"),sQuery(id+"F10.wireOp",EDGE,"E337.sketch_text.stroke-79"),sQuery(id+"F10.wireOp",EDGE,"E337.sketch_text.stroke-80"),sQuery(id+"F10.wireOp",EDGE,"E337.sketch_text.stroke-81"),sQuery(id+"F10.wireOp",EDGE,"E337.sketch_text.stroke-82"),sQuery(id+"F10.wireOp",EDGE,"E337.sketch_text.stroke-83"),sQuery(id+"F10.wireOp",EDGE,"E337.sketch_text.stroke-84"),sQuery(id+"F10.wireOp",EDGE,"E337.sketch_text.stroke-85"),sQuery(id+"F10.wireOp",EDGE,"E337.sketch_text.stroke-86"),sQuery(id+"F10.wireOp",EDGE,"E337.sketch_text.stroke-87"),sQuery(id+"F10.wireOp",EDGE,"E337.sketch_text.stroke-88"),sQuery(id+"F10.wireOp",EDGE,"E337.sketch_text.stroke-89"),sQuery(id+"F10.wireOp",EDGE,"E337.sketch_text.stroke-90"),sQuery(id+"F10.wireOp",EDGE,"E337.sketch_text.stroke-91"),sQuery(id+"F10.wireOp",EDGE,"E337.sketch_text.stroke-92"),sQuery(id+"F10.wireOp",EDGE,"E337.sketch_text.stroke-93"),sQuery(id+"F10.wireOp",EDGE,"E337.sketch_text.stroke-94"),sQuery(id+"F10.wireOp",EDGE,"E337.sketch_text.stroke-95"),sQuery(id+"F10.wireOp",EDGE,"E337.sketch_text.stroke-96"),sQuery(id+"F10.wireOp",EDGE,"E337.sketch_text.stroke-97"),sQuery(id+"F10.wireOp",EDGE,"E337.sketch_text.stroke-98"),sQuery(id+"F10.wireOp",EDGE,"E337.sketch_text.stroke-99"),sQuery(id+"F10.wireOp",EDGE,"E337.sketch_text.stroke-100"),sQuery(id+"F10.wireOp",EDGE,"E337.sketch_text.stroke-101"),sQuery(id+"F10.wireOp",EDGE,"E337.sketch_text.stroke-102"),sQuery(id+"F10.wireOp",EDGE,"E337.sketch_text.stroke-103"),sQuery(id+"F10.wireOp",EDGE,"E337.sketch_text.stroke-104"),sQuery(id+"F10.wireOp",EDGE,"E337.sketch_text.stroke-105"),sQuery(id+"F10.wireOp",EDGE,"E337.sketch_text.stroke-106"),sQuery(id+"F10.wireOp",EDGE,"E337.sketch_text.stroke-107"),sQuery(id+"F10.wireOp",EDGE,"E337.sketch_text.stroke-108"),sQuery(id+"F10.wireOp",EDGE,"E337.sketch_text.stroke-109"),sQuery(id+"F10.wireOp",EDGE,"E337.sketch_text.stroke-110"),sQuery(id+"F10.wireOp",EDGE,"E337.sketch_text.stroke-111"),sQuery(id+"F10.wireOp",EDGE,"E337.sketch_text.stroke-112"),sQuery(id+"F10.wireOp",EDGE,"E337.sketch_text.stroke-113"),sQuery(id+"F10.wireOp",EDGE,"E337.sketch_text.stroke-114"),sQuery(id+"F10.wireOp",EDGE,"E337.sketch_text.stroke-115"),sQuery(id+"F10.wireOp",EDGE,"E337.sketch_text.stroke-116"),sQuery(id+"F10.wireOp",EDGE,"E337.sketch_text.stroke-117"),sQuery(id+"F10.wireOp",EDGE,"E337.sketch_text.stroke-118"),sQuery(id+"F10.wireOp",EDGE,"E337.sketch_text.stroke-119"),sQuery(id+"F10.wireOp",EDGE,"E337.sketch_text.stroke-120"),sQuery(id+"F10.wireOp",EDGE,"E337.sketch_text.stroke-121"),sQuery(id+"F10.wireOp",EDGE,"E337.sketch_text.stroke-122"),sQuery(id+"F10.wireOp",EDGE,"E337.sketch_text.stroke-123"),sQuery(id+"F10.wireOp",EDGE,"E337.sketch_text.stroke-124"),sQuery(id+"F10.wireOp",EDGE,"E337.sketch_text.stroke-125"),sQuery(id+"F10.wireOp",EDGE,"E337.sketch_text.stroke-126"),sQuery(id+"F10.wireOp",EDGE,"E337.sketch_text.stroke-127"),sQuery(id+"F10.wireOp",EDGE,"E337.sketch_text.stroke-128"),sQuery(id+"F10.wireOp",EDGE,"E337.sketch_text.stroke-129"),sQuery(id+"F10.wireOp",EDGE,"E338.sketch_text.stroke-0"),sQuery(id+"F10.wireOp",EDGE,"E338.sketch_text.stroke-1"),sQuery(id+"F10.wireOp",EDGE,"E338.sketch_text.stroke-2"),sQuery(id+"F10.wireOp",EDGE,"E338.sketch_text.stroke-3"),sQuery(id+"F10.wireOp",EDGE,"E338.sketch_text.stroke-4"),sQuery(id+"F10.wireOp",EDGE,"E338.sketch_text.stroke-5"),sQuery(id+"F10.wireOp",EDGE,"E338.sketch_text.stroke-6"),sQuery(id+"F10.wireOp",EDGE,"E338.sketch_text.stroke-7"),sQuery(id+"F10.wireOp",EDGE,"E338.sketch_text.stroke-8"),sQuery(id+"F10.wireOp",EDGE,"E338.sketch_text.stroke-9"),sQuery(id+"F10.wireOp",EDGE,"E338.sketch_text.stroke-10"),sQuery(id+"F10.wireOp",EDGE,"E338.sketch_text.stroke-11"),sQuery(id+"F10.wireOp",EDGE,"E338.sketch_text.stroke-12"),sQuery(id+"F10.wireOp",EDGE,"E338.sketch_text.stroke-13"),sQuery(id+"F10.wireOp",EDGE,"E338.sketch_text.stroke-14"),sQuery(id+"F10.wireOp",EDGE,"E338.sketch_text.stroke-15"),sQuery(id+"F10.wireOp",EDGE,"E338.sketch_text.stroke-16"),sQuery(id+"F10.wireOp",EDGE,"E338.sketch_text.stroke-17"),sQuery(id+"F10.wireOp",EDGE,"E338.sketch_text.stroke-18"),sQuery(id+"F10.wireOp",EDGE,"E338.sketch_text.stroke-19"),sQuery(id+"F10.wireOp",EDGE,"E338.sketch_text.stroke-20"),sQuery(id+"F10.wireOp",EDGE,"E338.sketch_text.stroke-21"),sQuery(id+"F10.wireOp",EDGE,"E338.sketch_text.stroke-22"),sQuery(id+"F10.wireOp",EDGE,"E338.sketch_text.stroke-23"),sQuery(id+"F10.wireOp",EDGE,"E338.sketch_text.stroke-24"),sQuery(id+"F10.wireOp",EDGE,"E338.sketch_text.stroke-25"),sQuery(id+"F10.wireOp",EDGE,"E338.sketch_text.stroke-26"),sQuery(id+"F10.wireOp",EDGE,"E338.sketch_text.stroke-27"),sQuery(id+"F10.wireOp",EDGE,"E338.sketch_text.stroke-28"),sQuery(id+"F10.wireOp",EDGE,"E338.sketch_text.stroke-29"),sQuery(id+"F10.wireOp",EDGE,"E338.sketch_text.stroke-30"),sQuery(id+"F10.wireOp",EDGE,"E338.sketch_text.stroke-31"),sQuery(id+"F10.wireOp",EDGE,"E338.sketch_text.stroke-32"),sQuery(id+"F10.wireOp",EDGE,"E338.sketch_text.stroke-33"),sQuery(id+"F10.wireOp",EDGE,"E338.sketch_text.stroke-34"),sQuery(id+"F10.wireOp",EDGE,"E338.sketch_text.stroke-35"),sQuery(id+"F10.wireOp",EDGE,"E338.sketch_text.stroke-36"),sQuery(id+"F10.wireOp",EDGE,"E338.sketch_text.stroke-37"),sQuery(id+"F10.wireOp",EDGE,"E338.sketch_text.stroke-38"),sQuery(id+"F10.wireOp",EDGE,"E338.sketch_text.stroke-39"),sQuery(id+"F10.wireOp",EDGE,"E338.sketch_text.stroke-40"),sQuery(id+"F10.wireOp",EDGE,"E338.sketch_text.stroke-41"),sQuery(id+"F10.wireOp",EDGE,"E338.sketch_text.stroke-42"),sQuery(id+"F10.wireOp",EDGE,"E338.sketch_text.stroke-43"),sQuery(id+"F10.wireOp",EDGE,"E338.sketch_text.stroke-44"),sQuery(id+"F10.wireOp",EDGE,"E338.sketch_text.stroke-45"),sQuery(id+"F10.wireOp",EDGE,"E338.sketch_text.stroke-46"),sQuery(id+"F10.wireOp",EDGE,"E338.sketch_text.stroke-47"),sQuery(id+"F10.wireOp",EDGE,"E338.sketch_text.stroke-48"),sQuery(id+"F10.wireOp",EDGE,"E338.sketch_text.stroke-49"),sQuery(id+"F10.wireOp",EDGE,"E338.sketch_text.stroke-50"),sQuery(id+"F10.wireOp",EDGE,"E338.sketch_text.stroke-51"),sQuery(id+"F10.wireOp",EDGE,"E338.sketch_text.stroke-52"),sQuery(id+"F10.wireOp",EDGE,"E338.sketch_text.stroke-53"),sQuery(id+"F10.wireOp",EDGE,"E338.sketch_text.stroke-54"),sQuery(id+"F10.wireOp",EDGE,"E338.sketch_text.stroke-55"),sQuery(id+"F10.wireOp",EDGE,"E338.sketch_text.stroke-56"),sQuery(id+"F10.wireOp",EDGE,"E338.sketch_text.stroke-57"),sQuery(id+"F10.wireOp",EDGE,"E338.sketch_text.stroke-58"),sQuery(id+"F10.wireOp",EDGE,"E338.sketch_text.stroke-59"),sQuery(id+"F10.wireOp",EDGE,"E338.sketch_text.stroke-60"),sQuery(id+"F10.wireOp",EDGE,"E338.sketch_text.stroke-61"),sQuery(id+"F10.wireOp",EDGE,"E338.sketch_text.stroke-62"),sQuery(id+"F10.wireOp",EDGE,"E338.sketch_text.stroke-63"),sQuery(id+"F10.wireOp",EDGE,"E338.sketch_text.stroke-64"),sQuery(id+"F10.wireOp",EDGE,"E338.sketch_text.stroke-65"),sQuery(id+"F10.wireOp",EDGE,"E338.sketch_text.stroke-66"),sQuery(id+"F10.wireOp",EDGE,"E338.sketch_text.stroke-67"),sQuery(id+"F10.wireOp",EDGE,"E338.sketch_text.stroke-68"),sQuery(id+"F10.wireOp",EDGE,"E338.sketch_text.stroke-69"),sQuery(id+"F10.wireOp",EDGE,"E338.sketch_text.stroke-70"),sQuery(id+"F10.wireOp",EDGE,"E338.sketch_text.stroke-71"),sQuery(id+"F10.wireOp",EDGE,"E338.sketch_text.stroke-72"),sQuery(id+"F10.wireOp",EDGE,"E338.sketch_text.stroke-73"),sQuery(id+"F10.wireOp",EDGE,"E338.sketch_text.stroke-74"),sQuery(id+"F10.wireOp",EDGE,"E338.sketch_text.stroke-75"),sQuery(id+"F10.wireOp",EDGE,"E338.sketch_text.stroke-76"),sQuery(id+"F10.wireOp",EDGE,"E338.sketch_text.stroke-77"),sQuery(id+"F10.wireOp",EDGE,"E338.sketch_text.stroke-78"),sQuery(id+"F10.wireOp",EDGE,"E338.sketch_text.stroke-79"),sQuery(id+"F10.wireOp",EDGE,"E338.sketch_text.stroke-80"),sQuery(id+"F10.wireOp",EDGE,"E338.sketch_text.stroke-81"),sQuery(id+"F10.wireOp",EDGE,"E338.sketch_text.stroke-82"),sQuery(id+"F10.wireOp",EDGE,"E338.sketch_text.stroke-83"),sQuery(id+"F10.wireOp",EDGE,"E338.sketch_text.stroke-84"),sQuery(id+"F10.wireOp",EDGE,"E338.sketch_text.stroke-85"),sQuery(id+"F10.wireOp",EDGE,"E338.sketch_text.stroke-86"),sQuery(id+"F10.wireOp",EDGE,"E338.sketch_text.stroke-87"),sQuery(id+"F10.wireOp",EDGE,"E338.sketch_text.stroke-88"),sQuery(id+"F10.wireOp",EDGE,"E338.sketch_text.stroke-89"),sQuery(id+"F10.wireOp",EDGE,"E338.sketch_text.stroke-90"),sQuery(id+"F10.wireOp",EDGE,"E338.sketch_text.stroke-91"),sQuery(id+"F10.wireOp",EDGE,"E338.sketch_text.stroke-92"),sQuery(id+"F10.wireOp",EDGE,"E338.sketch_text.stroke-93"),sQuery(id+"F10.wireOp",EDGE,"E338.sketch_text.stroke-94"),sQuery(id+"F10.wireOp",EDGE,"E338.sketch_text.stroke-95"),sQuery(id+"F10.wireOp",EDGE,"E338.sketch_text.stroke-96"),sQuery(id+"F10.wireOp",EDGE,"E338.sketch_text.stroke-97"),sQuery(id+"F10.wireOp",EDGE,"E338.sketch_text.stroke-98"),sQuery(id+"F10.wireOp",EDGE,"E338.sketch_text.stroke-99"),sQuery(id+"F10.wireOp",EDGE,"E338.sketch_text.stroke-100"),sQuery(id+"F10.wireOp",EDGE,"E338.sketch_text.stroke-101"),sQuery(id+"F10.wireOp",EDGE,"E338.sketch_text.stroke-102"),sQuery(id+"F10.wireOp",EDGE,"E339.sketch_text.stroke-0"),sQuery(id+"F10.wireOp",EDGE,"E339.sketch_text.stroke-1"),sQuery(id+"F10.wireOp",EDGE,"E339.sketch_text.stroke-2"),sQuery(id+"F10.wireOp",EDGE,"E339.sketch_text.stroke-3"),sQuery(id+"F10.wireOp",EDGE,"E339.sketch_text.stroke-4"),sQuery(id+"F10.wireOp",EDGE,"E339.sketch_text.stroke-5"),sQuery(id+"F10.wireOp",EDGE,"E339.sketch_text.stroke-6"),sQuery(id+"F10.wireOp",EDGE,"E339.sketch_text.stroke-7"),sQuery(id+"F10.wireOp",EDGE,"E339.sketch_text.stroke-8"),sQuery(id+"F10.wireOp",EDGE,"E339.sketch_text.stroke-9"),sQuery(id+"F10.wireOp",EDGE,"E339.sketch_text.stroke-10"),sQuery(id+"F10.wireOp",EDGE,"E339.sketch_text.stroke-11"),sQuery(id+"F10.wireOp",EDGE,"E339.sketch_text.stroke-12"),sQuery(id+"F10.wireOp",EDGE,"E339.sketch_text.stroke-13"),sQuery(id+"F10.wireOp",EDGE,"E339.sketch_text.stroke-14"),sQuery(id+"F10.wireOp",EDGE,"E339.sketch_text.stroke-15"),sQuery(id+"F10.wireOp",EDGE,"E339.sketch_text.stroke-16"),sQuery(id+"F10.wireOp",EDGE,"E339.sketch_text.stroke-17"),sQuery(id+"F10.wireOp",EDGE,"E339.sketch_text.stroke-18"),sQuery(id+"F10.wireOp",EDGE,"E339.sketch_text.stroke-19"),sQuery(id+"F10.wireOp",EDGE,"E339.sketch_text.stroke-20"),sQuery(id+"F10.wireOp",EDGE,"E339.sketch_text.stroke-21"),sQuery(id+"F10.wireOp",EDGE,"E339.sketch_text.stroke-22"),sQuery(id+"F10.wireOp",EDGE,"E339.sketch_text.stroke-23"),sQuery(id+"F10.wireOp",EDGE,"E339.sketch_text.stroke-24"),sQuery(id+"F10.wireOp",EDGE,"E339.sketch_text.stroke-25"),sQuery(id+"F10.wireOp",EDGE,"E339.sketch_text.stroke-26"),sQuery(id+"F10.wireOp",EDGE,"E339.sketch_text.stroke-27"),sQuery(id+"F10.wireOp",EDGE,"E339.sketch_text.stroke-28"),sQuery(id+"F10.wireOp",EDGE,"E339.sketch_text.stroke-29"),sQuery(id+"F10.wireOp",EDGE,"E339.sketch_text.stroke-30"),sQuery(id+"F10.wireOp",EDGE,"E339.sketch_text.stroke-31"),sQuery(id+"F10.wireOp",EDGE,"E339.sketch_text.stroke-32"),sQuery(id+"F10.wireOp",EDGE,"E339.sketch_text.stroke-33"),sQuery(id+"F10.wireOp",EDGE,"E339.sketch_text.stroke-34"),sQuery(id+"F10.wireOp",EDGE,"E339.sketch_text.stroke-35"),sQuery(id+"F10.wireOp",EDGE,"E339.sketch_text.stroke-36"),sQuery(id+"F10.wireOp",EDGE,"E339.sketch_text.stroke-37"),sQuery(id+"F10.wireOp",EDGE,"E339.sketch_text.stroke-38"),sQuery(id+"F10.wireOp",EDGE,"E339.sketch_text.stroke-39"),sQuery(id+"F10.wireOp",EDGE,"E339.sketch_text.stroke-40"),sQuery(id+"F10.wireOp",EDGE,"E339.sketch_text.stroke-41"),sQuery(id+"F10.wireOp",EDGE,"E339.sketch_text.stroke-42"),sQuery(id+"F10.wireOp",EDGE,"E339.sketch_text.stroke-43"),sQuery(id+"F10.wireOp",EDGE,"E339.sketch_text.stroke-44"),sQuery(id+"F10.wireOp",EDGE,"E339.sketch_text.stroke-45"),sQuery(id+"F10.wireOp",EDGE,"E339.sketch_text.stroke-46"),sQuery(id+"F10.wireOp",EDGE,"E339.sketch_text.stroke-47"),sQuery(id+"F10.wireOp",EDGE,"E339.sketch_text.stroke-48"),sQuery(id+"F10.wireOp",EDGE,"E339.sketch_text.stroke-49"),sQuery(id+"F10.wireOp",EDGE,"E339.sketch_text.stroke-50"),sQuery(id+"F10.wireOp",EDGE,"E339.sketch_text.stroke-51"),sQuery(id+"F10.wireOp",EDGE,"E339.sketch_text.stroke-52"),sQuery(id+"F10.wireOp",EDGE,"E339.sketch_text.stroke-53"),sQuery(id+"F10.wireOp",EDGE,"E339.sketch_text.stroke-54"),sQuery(id+"F10.wireOp",EDGE,"E339.sketch_text.stroke-55"),sQuery(id+"F10.wireOp",EDGE,"E339.sketch_text.stroke-56"),sQuery(id+"F10.wireOp",EDGE,"E339.sketch_text.stroke-57"),sQuery(id+"F10.wireOp",EDGE,"E339.sketch_text.stroke-58"),sQuery(id+"F10.wireOp",EDGE,"E339.sketch_text.stroke-59"),sQuery(id+"F10.wireOp",EDGE,"E339.sketch_text.stroke-60"),sQuery(id+"F10.wireOp",EDGE,"E339.sketch_text.stroke-61"),sQuery(id+"F10.wireOp",EDGE,"E339.sketch_text.stroke-62"),sQuery(id+"F10.wireOp",EDGE,"E339.sketch_text.stroke-63"),sQuery(id+"F10.wireOp",EDGE,"E339.sketch_text.stroke-64"),sQuery(id+"F10.wireOp",EDGE,"E339.sketch_text.stroke-65"),sQuery(id+"F10.wireOp",EDGE,"E339.sketch_text.stroke-66"),sQuery(id+"F10.wireOp",EDGE,"E339.sketch_text.stroke-67"),sQuery(id+"F10.wireOp",EDGE,"E339.sketch_text.stroke-68"),sQuery(id+"F10.wireOp",EDGE,"E339.sketch_text.stroke-69"),sQuery(id+"F10.wireOp",EDGE,"E339.sketch_text.stroke-70"),sQuery(id+"F10.wireOp",EDGE,"E339.sketch_text.stroke-71"),sQuery(id+"F10.wireOp",EDGE,"E339.sketch_text.stroke-72"),sQuery(id+"F10.wireOp",EDGE,"E339.sketch_text.stroke-73"),sQuery(id+"F10.wireOp",EDGE,"E339.sketch_text.stroke-74"),sQuery(id+"F10.wireOp",EDGE,"E339.sketch_text.stroke-75"),sQuery(id+"F10.wireOp",EDGE,"E339.sketch_text.stroke-76"),sQuery(id+"F10.wireOp",EDGE,"E339.sketch_text.stroke-77"),sQuery(id+"F10.wireOp",EDGE,"E339.sketch_text.stroke-78"),sQuery(id+"F10.wireOp",EDGE,"E339.sketch_text.stroke-79"),sQuery(id+"F10.wireOp",EDGE,"E339.sketch_text.stroke-80"),sQuery(id+"F10.wireOp",EDGE,"E339.sketch_text.stroke-81"),sQuery(id+"F10.wireOp",EDGE,"E339.sketch_text.stroke-82"),sQuery(id+"F10.wireOp",EDGE,"E339.sketch_text.stroke-83"),sQuery(id+"F10.wireOp",EDGE,"E339.sketch_text.stroke-84"),sQuery(id+"F10.wireOp",EDGE,"E339.sketch_text.stroke-85"),sQuery(id+"F10.wireOp",EDGE,"E339.sketch_text.stroke-86"),sQuery(id+"F10.wireOp",EDGE,"E339.sketch_text.stroke-87"),sQuery(id+"F10.wireOp",EDGE,"E339.sketch_text.stroke-88"),sQuery(id+"F10.wireOp",EDGE,"E339.sketch_text.stroke-89"),sQuery(id+"F10.wireOp",EDGE,"E339.sketch_text.stroke-90"),sQuery(id+"F10.wireOp",EDGE,"E339.sketch_text.stroke-91"),sQuery(id+"F10.wireOp",EDGE,"E339.sketch_text.stroke-92"),sQuery(id+"F10.wireOp",EDGE,"E339.sketch_text.stroke-93"),sQuery(id+"F10.wireOp",EDGE,"E339.sketch_text.stroke-94"),sQuery(id+"F10.wireOp",EDGE,"E339.sketch_text.stroke-95"),sQuery(id+"F10.wireOp",EDGE,"E339.sketch_text.stroke-96"),sQuery(id+"F10.wireOp",EDGE,"E339.sketch_text.stroke-97"),sQuery(id+"F10.wireOp",EDGE,"E339.sketch_text.stroke-98"),sQuery(id+"F10.wireOp",EDGE,"E339.sketch_text.stroke-99"),sQuery(id+"F10.wireOp",EDGE,"E339.sketch_text.stroke-100"),sQuery(id+"F10.wireOp",EDGE,"E339.sketch_text.stroke-101"),sQuery(id+"F10.wireOp",EDGE,"E339.sketch_text.stroke-102"),sQuery(id+"F10.wireOp",EDGE,"E339.sketch_text.stroke-103"),sQuery(id+"F10.wireOp",EDGE,"E339.sketch_text.stroke-104"),sQuery(id+"F10.wireOp",EDGE,"E339.sketch_text.stroke-105"),sQuery(id+"F10.wireOp",EDGE,"E339.sketch_text.stroke-106"),sQuery(id+"F10.wireOp",EDGE,"E339.sketch_text.stroke-107"),sQuery(id+"F10.wireOp",EDGE,"E339.sketch_text.stroke-108"),sQuery(id+"F10.wireOp",EDGE,"E339.sketch_text.stroke-109"),sQuery(id+"F10.wireOp",EDGE,"E339.sketch_text.stroke-110"),sQuery(id+"F10.wireOp",EDGE,"E339.sketch_text.stroke-111"),sQuery(id+"F10.wireOp",EDGE,"E339.sketch_text.stroke-112")])],"isStart":false})]});
            var sketch = newSketch(context, id + "F13", { "sketchPlane" : qUnion([Q0])});
            skText(sketch, "E350", { "text": "SEDIA P - ENZO MARI, 1974", "fontName": "AllertaStencil-Regular.ttf"});
            skLineSegment(sketch, "E351", {"start": v(14.7, 71.7) * mm, "end": v(14.7, 73.2) * mm, "construction": true});
            skLineSegment(sketch, "E352", {"start": v(14.7, 71.7) * mm, "end": v(13.2, 71.7) * mm, "construction": true});
            const initialGuessF13  = {"E350": [0.0147, 0.0717, 0, -1, 0.00166]};
            skSetInitialGuess(sketch, initialGuessF13);
            skSolve(sketch);
        }
        {
            var Q0;
            Q0 = qSketchRegion(id + "F13", true);
            var Q1;
            Q1=makeQuery(id+"F12.opBoolean","MERGE",FACE,{"derivedFrom":[makeQuery(id+"F3.opExtrude","CAP_FACE",FACE,{"disambiguationData":[OSD([sQuery(id+"F2.wireOp",EDGE,"E1.bottom"),sQuery(id+"F2.wireOp",EDGE,"E1.top"),sQuery(id+"F2.wireOp",EDGE,"E1.left"),sQuery(id+"F2.wireOp",EDGE,"E1.right"),sQuery(id+"F2.wireOp",EDGE,"E5"),sQuery(id+"F2.wireOp",EDGE,"E6"),sQuery(id+"F2.wireOp",EDGE,"E7"),sQuery(id+"F2.wireOp",EDGE,"E8"),sQuery(id+"F2.wireOp",EDGE,"E9"),sQuery(id+"F2.wireOp",EDGE,"E10"),sQuery(id+"F2.wireOp",EDGE,"E12"),sQuery(id+"F2.wireOp",EDGE,"E14"),sQuery(id+"F2.wireOp",EDGE,"E19"),sQuery(id+"F2.wireOp",EDGE,"E24"),sQuery(id+"F2.wireOp",EDGE,"E25"),sQuery(id+"F2.wireOp",EDGE,"E28"),sQuery(id+"F2.wireOp",EDGE,"E29"),sQuery(id+"F2.wireOp",EDGE,"E32"),sQuery(id+"F2.wireOp",EDGE,"E33"),sQuery(id+"F2.wireOp",EDGE,"E36"),sQuery(id+"F2.wireOp",EDGE,"E37"),sQuery(id+"F2.wireOp",EDGE,"E40"),sQuery(id+"F2.wireOp",EDGE,"E41"),sQuery(id+"F2.wireOp",EDGE,"E44"),sQuery(id+"F2.wireOp",EDGE,"E45"),sQuery(id+"F2.wireOp",EDGE,"E48"),sQuery(id+"F2.wireOp",EDGE,"E49"),sQuery(id+"F2.wireOp",EDGE,"E52"),sQuery(id+"F2.wireOp",EDGE,"E53"),sQuery(id+"F2.wireOp",EDGE,"E56"),sQuery(id+"F2.wireOp",EDGE,"E57"),sQuery(id+"F2.wireOp",EDGE,"E58"),sQuery(id+"F2.wireOp",EDGE,"E59"),sQuery(id+"F2.wireOp",EDGE,"E60"),sQuery(id+"F2.wireOp",EDGE,"E61"),sQuery(id+"F2.wireOp",EDGE,"E62"),sQuery(id+"F2.wireOp",EDGE,"E63"),sQuery(id+"F2.wireOp",EDGE,"E65"),sQuery(id+"F2.wireOp",EDGE,"E67"),sQuery(id+"F2.wireOp",EDGE,"E68"),sQuery(id+"F2.wireOp",EDGE,"E69"),sQuery(id+"F2.wireOp",EDGE,"E70"),sQuery(id+"F2.wireOp",EDGE,"E71"),sQuery(id+"F2.wireOp",EDGE,"E72"),sQuery(id+"F2.wireOp",EDGE,"E73"),sQuery(id+"F2.wireOp",EDGE,"E74"),sQuery(id+"F2.wireOp",EDGE,"E75"),sQuery(id+"F2.wireOp",EDGE,"E77"),sQuery(id+"F2.wireOp",EDGE,"E80"),sQuery(id+"F2.wireOp",EDGE,"E82"),sQuery(id+"F2.wireOp",EDGE,"E84"),sQuery(id+"F2.wireOp",EDGE,"E85")])],"isStart":true}),makeQuery(id+"F5.opExtrude","CAP_FACE",FACE,{"disambiguationData":[OSD([sQuery(id+"F4.wireOp",EDGE,"E88.bottom"),sQuery(id+"F4.wireOp",EDGE,"E88.top"),sQuery(id+"F4.wireOp",EDGE,"E88.left"),sQuery(id+"F4.wireOp",EDGE,"E88.right"),sQuery(id+"F4.wireOp",EDGE,"E92"),sQuery(id+"F4.wireOp",EDGE,"E93"),sQuery(id+"F4.wireOp",EDGE,"E94"),sQuery(id+"F4.wireOp",EDGE,"E95"),sQuery(id+"F4.wireOp",EDGE,"E96"),sQuery(id+"F4.wireOp",EDGE,"E97"),sQuery(id+"F4.wireOp",EDGE,"E99"),sQuery(id+"F4.wireOp",EDGE,"E101"),sQuery(id+"F4.wireOp",EDGE,"E106"),sQuery(id+"F4.wireOp",EDGE,"E111"),sQuery(id+"F4.wireOp",EDGE,"E112"),sQuery(id+"F4.wireOp",EDGE,"E115"),sQuery(id+"F4.wireOp",EDGE,"E116"),sQuery(id+"F4.wireOp",EDGE,"E119"),sQuery(id+"F4.wireOp",EDGE,"E120"),sQuery(id+"F4.wireOp",EDGE,"E123"),sQuery(id+"F4.wireOp",EDGE,"E124"),sQuery(id+"F4.wireOp",EDGE,"E127"),sQuery(id+"F4.wireOp",EDGE,"E128"),sQuery(id+"F4.wireOp",EDGE,"E129"),sQuery(id+"F4.wireOp",EDGE,"E130"),sQuery(id+"F4.wireOp",EDGE,"E131"),sQuery(id+"F4.wireOp",EDGE,"E132"),sQuery(id+"F4.wireOp",EDGE,"E134"),sQuery(id+"F4.wireOp",EDGE,"E136"),sQuery(id+"F4.wireOp",EDGE,"E137"),sQuery(id+"F4.wireOp",EDGE,"E138"),sQuery(id+"F4.wireOp",EDGE,"E139"),sQuery(id+"F4.wireOp",EDGE,"E140"),sQuery(id+"F4.wireOp",EDGE,"E143"),sQuery(id+"F4.wireOp",EDGE,"E145"),sQuery(id+"F4.wireOp",EDGE,"E146")])],"isStart":true}),makeQuery(id+"F7.opExtrude","CAP_FACE",FACE,{"disambiguationData":[OSD([sQuery(id+"F6.wireOp",EDGE,"E150.bottom"),sQuery(id+"F6.wireOp",EDGE,"E150.top"),sQuery(id+"F6.wireOp",EDGE,"E150.left"),sQuery(id+"F6.wireOp",EDGE,"E150.right"),sQuery(id+"F6.wireOp",EDGE,"E154"),sQuery(id+"F6.wireOp",EDGE,"E155"),sQuery(id+"F6.wireOp",EDGE,"E156"),sQuery(id+"F6.wireOp",EDGE,"E157"),sQuery(id+"F6.wireOp",EDGE,"E158"),sQuery(id+"F6.wireOp",EDGE,"E159"),sQuery(id+"F6.wireOp",EDGE,"E161"),sQuery(id+"F6.wireOp",EDGE,"E163"),sQuery(id+"F6.wireOp",EDGE,"E168"),sQuery(id+"F6.wireOp",EDGE,"E173"),sQuery(id+"F6.wireOp",EDGE,"E174"),sQuery(id+"F6.wireOp",EDGE,"E177"),sQuery(id+"F6.wireOp",EDGE,"E178"),sQuery(id+"F6.wireOp",EDGE,"E181"),sQuery(id+"F6.wireOp",EDGE,"E182"),sQuery(id+"F6.wireOp",EDGE,"E185"),sQuery(id+"F6.wireOp",EDGE,"E186"),sQuery(id+"F6.wireOp",EDGE,"E189"),sQuery(id+"F6.wireOp",EDGE,"E190"),sQuery(id+"F6.wireOp",EDGE,"E191"),sQuery(id+"F6.wireOp",EDGE,"E192"),sQuery(id+"F6.wireOp",EDGE,"E193"),sQuery(id+"F6.wireOp",EDGE,"E194"),sQuery(id+"F6.wireOp",EDGE,"E196"),sQuery(id+"F6.wireOp",EDGE,"E198"),sQuery(id+"F6.wireOp",EDGE,"E199"),sQuery(id+"F6.wireOp",EDGE,"E200"),sQuery(id+"F6.wireOp",EDGE,"E201"),sQuery(id+"F6.wireOp",EDGE,"E202"),sQuery(id+"F6.wireOp",EDGE,"E205"),sQuery(id+"F6.wireOp",EDGE,"E207"),sQuery(id+"F6.wireOp",EDGE,"E208")])],"isStart":true}),makeQuery(id+"F9.opExtrude","CAP_FACE",FACE,{"disambiguationData":[OSD([sQuery(id+"F8.wireOp",EDGE,"E210.bottom"),sQuery(id+"F8.wireOp",EDGE,"E210.top"),sQuery(id+"F8.wireOp",EDGE,"E211"),sQuery(id+"F8.wireOp",EDGE,"E214"),sQuery(id+"F8.wireOp",EDGE,"E215"),sQuery(id+"F8.wireOp",EDGE,"E216"),sQuery(id+"F8.wireOp",EDGE,"E219"),sQuery(id+"F8.wireOp",EDGE,"E220"),sQuery(id+"F8.wireOp",EDGE,"E221"),sQuery(id+"F8.wireOp",EDGE,"E222"),sQuery(id+"F8.wireOp",EDGE,"E223"),sQuery(id+"F8.wireOp",EDGE,"E226"),sQuery(id+"F8.wireOp",EDGE,"E227"),sQuery(id+"F8.wireOp",EDGE,"E228"),sQuery(id+"F8.wireOp",EDGE,"E233"),sQuery(id+"F8.wireOp",EDGE,"E234"),sQuery(id+"F8.wireOp",EDGE,"E237"),sQuery(id+"F8.wireOp",EDGE,"E240"),sQuery(id+"F8.wireOp",EDGE,"E241"),sQuery(id+"F8.wireOp",EDGE,"E242"),sQuery(id+"F8.wireOp",EDGE,"E243"),sQuery(id+"F8.wireOp",EDGE,"E244"),sQuery(id+"F8.wireOp",EDGE,"E245"),sQuery(id+"F8.wireOp",EDGE,"E246"),sQuery(id+"F8.wireOp",EDGE,"E247"),sQuery(id+"F8.wireOp",EDGE,"E248.bottom"),sQuery(id+"F8.wireOp",EDGE,"E248.top"),sQuery(id+"F8.wireOp",EDGE,"E248.left"),sQuery(id+"F8.wireOp",EDGE,"E248.right"),sQuery(id+"F8.wireOp",EDGE,"E249.bottom"),sQuery(id+"F8.wireOp",EDGE,"E249.top"),sQuery(id+"F8.wireOp",EDGE,"E249.left"),sQuery(id+"F8.wireOp",EDGE,"E249.right"),sQuery(id+"F8.wireOp",EDGE,"E250.bottom"),sQuery(id+"F8.wireOp",EDGE,"E250.top"),sQuery(id+"F8.wireOp",EDGE,"E250.left"),sQuery(id+"F8.wireOp",EDGE,"E250.right"),sQuery(id+"F8.wireOp",EDGE,"E251.bottom"),sQuery(id+"F8.wireOp",EDGE,"E251.top"),sQuery(id+"F8.wireOp",EDGE,"E251.left"),sQuery(id+"F8.wireOp",EDGE,"E251.right"),sQuery(id+"F8.wireOp",EDGE,"E254"),sQuery(id+"F8.wireOp",EDGE,"E255"),sQuery(id+"F8.wireOp",EDGE,"E260"),sQuery(id+"F8.wireOp",EDGE,"E263"),sQuery(id+"F8.wireOp",EDGE,"E266"),sQuery(id+"F8.wireOp",EDGE,"E269"),sQuery(id+"F8.wireOp",EDGE,"E272"),sQuery(id+"F8.wireOp",EDGE,"E273"),sQuery(id+"F8.wireOp",EDGE,"E276"),sQuery(id+"F8.wireOp",EDGE,"E277"),sQuery(id+"F8.wireOp",EDGE,"E278"),sQuery(id+"F8.wireOp",EDGE,"E279"),sQuery(id+"F8.wireOp",EDGE,"E280"),sQuery(id+"F8.wireOp",EDGE,"E281"),sQuery(id+"F8.wireOp",EDGE,"E282"),sQuery(id+"F8.wireOp",EDGE,"E283"),sQuery(id+"F8.wireOp",EDGE,"E284"),sQuery(id+"F8.wireOp",EDGE,"E285")])],"isStart":true}),makeQuery(id+"F11.opExtrude","CAP_FACE",FACE,{"disambiguationData":[OSD([sQuery(id+"F10.wireOp",EDGE,"E288.bottom"),sQuery(id+"F10.wireOp",EDGE,"E288.top"),sQuery(id+"F10.wireOp",EDGE,"E288.left"),sQuery(id+"F10.wireOp",EDGE,"E288.right"),sQuery(id+"F10.wireOp",EDGE,"E290.filletArc"),sQuery(id+"F10.wireOp",EDGE,"E291.filletArc"),sQuery(id+"F10.wireOp",EDGE,"E292.filletArc"),sQuery(id+"F10.wireOp",EDGE,"E293.filletArc"),sQuery(id+"F10.wireOp",EDGE,"E303"),sQuery(id+"F10.wireOp",EDGE,"E304"),sQuery(id+"F10.wireOp",EDGE,"E305"),sQuery(id+"F10.wireOp",EDGE,"E306"),sQuery(id+"F10.wireOp",EDGE,"E307"),sQuery(id+"F10.wireOp",EDGE,"E308"),sQuery(id+"F10.wireOp",EDGE,"E309"),sQuery(id+"F10.wireOp",EDGE,"E310"),sQuery(id+"F10.wireOp",EDGE,"E311"),sQuery(id+"F10.wireOp",EDGE,"E312"),sQuery(id+"F10.wireOp",EDGE,"E313"),sQuery(id+"F10.wireOp",EDGE,"E314"),sQuery(id+"F10.wireOp",EDGE,"E315"),sQuery(id+"F10.wireOp",EDGE,"E316"),sQuery(id+"F10.wireOp",EDGE,"E317"),sQuery(id+"F10.wireOp",EDGE,"E318"),sQuery(id+"F10.wireOp",EDGE,"E319.filletArc"),sQuery(id+"F10.wireOp",EDGE,"E320.filletArc"),sQuery(id+"F10.wireOp",EDGE,"E321.filletArc"),sQuery(id+"F10.wireOp",EDGE,"E322.filletArc"),sQuery(id+"F10.wireOp",EDGE,"E323.filletArc"),sQuery(id+"F10.wireOp",EDGE,"E324.filletArc"),sQuery(id+"F10.wireOp",EDGE,"E325.filletArc"),sQuery(id+"F10.wireOp",EDGE,"E326.filletArc"),sQuery(id+"F10.wireOp",EDGE,"E327.filletArc"),sQuery(id+"F10.wireOp",EDGE,"E328.filletArc"),sQuery(id+"F10.wireOp",EDGE,"E329.filletArc"),sQuery(id+"F10.wireOp",EDGE,"E330.filletArc"),sQuery(id+"F10.wireOp",EDGE,"E331.filletArc"),sQuery(id+"F10.wireOp",EDGE,"E332.filletArc"),sQuery(id+"F10.wireOp",EDGE,"E333.filletArc"),sQuery(id+"F10.wireOp",EDGE,"E334.filletArc"),sQuery(id+"F10.wireOp",EDGE,"E335.sketch_text.stroke-0"),sQuery(id+"F10.wireOp",EDGE,"E335.sketch_text.stroke-1"),sQuery(id+"F10.wireOp",EDGE,"E335.sketch_text.stroke-2"),sQuery(id+"F10.wireOp",EDGE,"E335.sketch_text.stroke-3"),sQuery(id+"F10.wireOp",EDGE,"E335.sketch_text.stroke-4"),sQuery(id+"F10.wireOp",EDGE,"E335.sketch_text.stroke-5"),sQuery(id+"F10.wireOp",EDGE,"E335.sketch_text.stroke-6"),sQuery(id+"F10.wireOp",EDGE,"E335.sketch_text.stroke-7"),sQuery(id+"F10.wireOp",EDGE,"E335.sketch_text.stroke-8"),sQuery(id+"F10.wireOp",EDGE,"E335.sketch_text.stroke-9"),sQuery(id+"F10.wireOp",EDGE,"E335.sketch_text.stroke-10"),sQuery(id+"F10.wireOp",EDGE,"E335.sketch_text.stroke-11"),sQuery(id+"F10.wireOp",EDGE,"E335.sketch_text.stroke-12"),sQuery(id+"F10.wireOp",EDGE,"E335.sketch_text.stroke-13"),sQuery(id+"F10.wireOp",EDGE,"E335.sketch_text.stroke-14"),sQuery(id+"F10.wireOp",EDGE,"E335.sketch_text.stroke-15"),sQuery(id+"F10.wireOp",EDGE,"E335.sketch_text.stroke-16"),sQuery(id+"F10.wireOp",EDGE,"E335.sketch_text.stroke-17"),sQuery(id+"F10.wireOp",EDGE,"E335.sketch_text.stroke-18"),sQuery(id+"F10.wireOp",EDGE,"E335.sketch_text.stroke-19"),sQuery(id+"F10.wireOp",EDGE,"E335.sketch_text.stroke-20"),sQuery(id+"F10.wireOp",EDGE,"E335.sketch_text.stroke-21"),sQuery(id+"F10.wireOp",EDGE,"E335.sketch_text.stroke-22"),sQuery(id+"F10.wireOp",EDGE,"E335.sketch_text.stroke-23"),sQuery(id+"F10.wireOp",EDGE,"E335.sketch_text.stroke-24"),sQuery(id+"F10.wireOp",EDGE,"E335.sketch_text.stroke-25"),sQuery(id+"F10.wireOp",EDGE,"E335.sketch_text.stroke-26"),sQuery(id+"F10.wireOp",EDGE,"E335.sketch_text.stroke-27"),sQuery(id+"F10.wireOp",EDGE,"E335.sketch_text.stroke-28"),sQuery(id+"F10.wireOp",EDGE,"E335.sketch_text.stroke-29"),sQuery(id+"F10.wireOp",EDGE,"E335.sketch_text.stroke-30"),sQuery(id+"F10.wireOp",EDGE,"E335.sketch_text.stroke-31"),sQuery(id+"F10.wireOp",EDGE,"E335.sketch_text.stroke-32"),sQuery(id+"F10.wireOp",EDGE,"E335.sketch_text.stroke-33"),sQuery(id+"F10.wireOp",EDGE,"E335.sketch_text.stroke-34"),sQuery(id+"F10.wireOp",EDGE,"E335.sketch_text.stroke-35"),sQuery(id+"F10.wireOp",EDGE,"E335.sketch_text.stroke-36"),sQuery(id+"F10.wireOp",EDGE,"E335.sketch_text.stroke-37"),sQuery(id+"F10.wireOp",EDGE,"E335.sketch_text.stroke-38"),sQuery(id+"F10.wireOp",EDGE,"E335.sketch_text.stroke-39"),sQuery(id+"F10.wireOp",EDGE,"E335.sketch_text.stroke-40"),sQuery(id+"F10.wireOp",EDGE,"E335.sketch_text.stroke-41"),sQuery(id+"F10.wireOp",EDGE,"E335.sketch_text.stroke-42"),sQuery(id+"F10.wireOp",EDGE,"E335.sketch_text.stroke-43"),sQuery(id+"F10.wireOp",EDGE,"E335.sketch_text.stroke-44"),sQuery(id+"F10.wireOp",EDGE,"E335.sketch_text.stroke-45"),sQuery(id+"F10.wireOp",EDGE,"E335.sketch_text.stroke-46"),sQuery(id+"F10.wireOp",EDGE,"E335.sketch_text.stroke-47"),sQuery(id+"F10.wireOp",EDGE,"E335.sketch_text.stroke-48"),sQuery(id+"F10.wireOp",EDGE,"E335.sketch_text.stroke-49"),sQuery(id+"F10.wireOp",EDGE,"E335.sketch_text.stroke-50"),sQuery(id+"F10.wireOp",EDGE,"E335.sketch_text.stroke-51"),sQuery(id+"F10.wireOp",EDGE,"E335.sketch_text.stroke-52"),sQuery(id+"F10.wireOp",EDGE,"E335.sketch_text.stroke-53"),sQuery(id+"F10.wireOp",EDGE,"E335.sketch_text.stroke-54"),sQuery(id+"F10.wireOp",EDGE,"E335.sketch_text.stroke-55"),sQuery(id+"F10.wireOp",EDGE,"E335.sketch_text.stroke-56"),sQuery(id+"F10.wireOp",EDGE,"E335.sketch_text.stroke-57"),sQuery(id+"F10.wireOp",EDGE,"E335.sketch_text.stroke-58"),sQuery(id+"F10.wireOp",EDGE,"E335.sketch_text.stroke-59"),sQuery(id+"F10.wireOp",EDGE,"E335.sketch_text.stroke-60"),sQuery(id+"F10.wireOp",EDGE,"E335.sketch_text.stroke-61"),sQuery(id+"F10.wireOp",EDGE,"E335.sketch_text.stroke-62"),sQuery(id+"F10.wireOp",EDGE,"E335.sketch_text.stroke-63"),sQuery(id+"F10.wireOp",EDGE,"E335.sketch_text.stroke-64"),sQuery(id+"F10.wireOp",EDGE,"E335.sketch_text.stroke-65"),sQuery(id+"F10.wireOp",EDGE,"E335.sketch_text.stroke-66"),sQuery(id+"F10.wireOp",EDGE,"E335.sketch_text.stroke-67"),sQuery(id+"F10.wireOp",EDGE,"E335.sketch_text.stroke-68"),sQuery(id+"F10.wireOp",EDGE,"E335.sketch_text.stroke-69"),sQuery(id+"F10.wireOp",EDGE,"E335.sketch_text.stroke-70"),sQuery(id+"F10.wireOp",EDGE,"E335.sketch_text.stroke-71"),sQuery(id+"F10.wireOp",EDGE,"E335.sketch_text.stroke-72"),sQuery(id+"F10.wireOp",EDGE,"E335.sketch_text.stroke-73"),sQuery(id+"F10.wireOp",EDGE,"E335.sketch_text.stroke-74"),sQuery(id+"F10.wireOp",EDGE,"E335.sketch_text.stroke-75"),sQuery(id+"F10.wireOp",EDGE,"E335.sketch_text.stroke-76"),sQuery(id+"F10.wireOp",EDGE,"E335.sketch_text.stroke-77"),sQuery(id+"F10.wireOp",EDGE,"E335.sketch_text.stroke-78"),sQuery(id+"F10.wireOp",EDGE,"E335.sketch_text.stroke-79"),sQuery(id+"F10.wireOp",EDGE,"E335.sketch_text.stroke-80"),sQuery(id+"F10.wireOp",EDGE,"E335.sketch_text.stroke-81"),sQuery(id+"F10.wireOp",EDGE,"E335.sketch_text.stroke-82"),sQuery(id+"F10.wireOp",EDGE,"E335.sketch_text.stroke-83"),sQuery(id+"F10.wireOp",EDGE,"E335.sketch_text.stroke-84"),sQuery(id+"F10.wireOp",EDGE,"E335.sketch_text.stroke-85"),sQuery(id+"F10.wireOp",EDGE,"E335.sketch_text.stroke-86"),sQuery(id+"F10.wireOp",EDGE,"E335.sketch_text.stroke-87"),sQuery(id+"F10.wireOp",EDGE,"E335.sketch_text.stroke-88"),sQuery(id+"F10.wireOp",EDGE,"E335.sketch_text.stroke-89"),sQuery(id+"F10.wireOp",EDGE,"E335.sketch_text.stroke-90"),sQuery(id+"F10.wireOp",EDGE,"E335.sketch_text.stroke-91"),sQuery(id+"F10.wireOp",EDGE,"E335.sketch_text.stroke-92"),sQuery(id+"F10.wireOp",EDGE,"E335.sketch_text.stroke-93"),sQuery(id+"F10.wireOp",EDGE,"E335.sketch_text.stroke-94"),sQuery(id+"F10.wireOp",EDGE,"E335.sketch_text.stroke-95"),sQuery(id+"F10.wireOp",EDGE,"E335.sketch_text.stroke-96"),sQuery(id+"F10.wireOp",EDGE,"E335.sketch_text.stroke-97"),sQuery(id+"F10.wireOp",EDGE,"E336.sketch_text.stroke-0"),sQuery(id+"F10.wireOp",EDGE,"E336.sketch_text.stroke-1"),sQuery(id+"F10.wireOp",EDGE,"E336.sketch_text.stroke-2"),sQuery(id+"F10.wireOp",EDGE,"E336.sketch_text.stroke-3"),sQuery(id+"F10.wireOp",EDGE,"E336.sketch_text.stroke-4"),sQuery(id+"F10.wireOp",EDGE,"E336.sketch_text.stroke-5"),sQuery(id+"F10.wireOp",EDGE,"E336.sketch_text.stroke-6"),sQuery(id+"F10.wireOp",EDGE,"E336.sketch_text.stroke-7"),sQuery(id+"F10.wireOp",EDGE,"E336.sketch_text.stroke-8"),sQuery(id+"F10.wireOp",EDGE,"E336.sketch_text.stroke-9"),sQuery(id+"F10.wireOp",EDGE,"E336.sketch_text.stroke-10"),sQuery(id+"F10.wireOp",EDGE,"E336.sketch_text.stroke-11"),sQuery(id+"F10.wireOp",EDGE,"E336.sketch_text.stroke-12"),sQuery(id+"F10.wireOp",EDGE,"E336.sketch_text.stroke-13"),sQuery(id+"F10.wireOp",EDGE,"E336.sketch_text.stroke-14"),sQuery(id+"F10.wireOp",EDGE,"E336.sketch_text.stroke-15"),sQuery(id+"F10.wireOp",EDGE,"E336.sketch_text.stroke-16"),sQuery(id+"F10.wireOp",EDGE,"E336.sketch_text.stroke-17"),sQuery(id+"F10.wireOp",EDGE,"E336.sketch_text.stroke-18"),sQuery(id+"F10.wireOp",EDGE,"E336.sketch_text.stroke-19"),sQuery(id+"F10.wireOp",EDGE,"E336.sketch_text.stroke-20"),sQuery(id+"F10.wireOp",EDGE,"E336.sketch_text.stroke-21"),sQuery(id+"F10.wireOp",EDGE,"E336.sketch_text.stroke-22"),sQuery(id+"F10.wireOp",EDGE,"E336.sketch_text.stroke-23"),sQuery(id+"F10.wireOp",EDGE,"E336.sketch_text.stroke-24"),sQuery(id+"F10.wireOp",EDGE,"E336.sketch_text.stroke-25"),sQuery(id+"F10.wireOp",EDGE,"E336.sketch_text.stroke-26"),sQuery(id+"F10.wireOp",EDGE,"E336.sketch_text.stroke-27"),sQuery(id+"F10.wireOp",EDGE,"E336.sketch_text.stroke-28"),sQuery(id+"F10.wireOp",EDGE,"E336.sketch_text.stroke-29"),sQuery(id+"F10.wireOp",EDGE,"E336.sketch_text.stroke-30"),sQuery(id+"F10.wireOp",EDGE,"E336.sketch_text.stroke-31"),sQuery(id+"F10.wireOp",EDGE,"E336.sketch_text.stroke-32"),sQuery(id+"F10.wireOp",EDGE,"E336.sketch_text.stroke-33"),sQuery(id+"F10.wireOp",EDGE,"E336.sketch_text.stroke-34"),sQuery(id+"F10.wireOp",EDGE,"E336.sketch_text.stroke-35"),sQuery(id+"F10.wireOp",EDGE,"E336.sketch_text.stroke-36"),sQuery(id+"F10.wireOp",EDGE,"E336.sketch_text.stroke-37"),sQuery(id+"F10.wireOp",EDGE,"E336.sketch_text.stroke-38"),sQuery(id+"F10.wireOp",EDGE,"E336.sketch_text.stroke-39"),sQuery(id+"F10.wireOp",EDGE,"E336.sketch_text.stroke-40"),sQuery(id+"F10.wireOp",EDGE,"E336.sketch_text.stroke-41"),sQuery(id+"F10.wireOp",EDGE,"E336.sketch_text.stroke-42"),sQuery(id+"F10.wireOp",EDGE,"E336.sketch_text.stroke-43"),sQuery(id+"F10.wireOp",EDGE,"E336.sketch_text.stroke-44"),sQuery(id+"F10.wireOp",EDGE,"E336.sketch_text.stroke-45"),sQuery(id+"F10.wireOp",EDGE,"E336.sketch_text.stroke-46"),sQuery(id+"F10.wireOp",EDGE,"E336.sketch_text.stroke-47"),sQuery(id+"F10.wireOp",EDGE,"E336.sketch_text.stroke-48"),sQuery(id+"F10.wireOp",EDGE,"E336.sketch_text.stroke-49"),sQuery(id+"F10.wireOp",EDGE,"E336.sketch_text.stroke-50"),sQuery(id+"F10.wireOp",EDGE,"E336.sketch_text.stroke-51"),sQuery(id+"F10.wireOp",EDGE,"E336.sketch_text.stroke-52"),sQuery(id+"F10.wireOp",EDGE,"E336.sketch_text.stroke-53"),sQuery(id+"F10.wireOp",EDGE,"E336.sketch_text.stroke-54"),sQuery(id+"F10.wireOp",EDGE,"E336.sketch_text.stroke-55"),sQuery(id+"F10.wireOp",EDGE,"E336.sketch_text.stroke-56"),sQuery(id+"F10.wireOp",EDGE,"E336.sketch_text.stroke-57"),sQuery(id+"F10.wireOp",EDGE,"E336.sketch_text.stroke-58"),sQuery(id+"F10.wireOp",EDGE,"E336.sketch_text.stroke-59"),sQuery(id+"F10.wireOp",EDGE,"E336.sketch_text.stroke-60"),sQuery(id+"F10.wireOp",EDGE,"E336.sketch_text.stroke-61"),sQuery(id+"F10.wireOp",EDGE,"E336.sketch_text.stroke-62"),sQuery(id+"F10.wireOp",EDGE,"E336.sketch_text.stroke-63"),sQuery(id+"F10.wireOp",EDGE,"E336.sketch_text.stroke-64"),sQuery(id+"F10.wireOp",EDGE,"E336.sketch_text.stroke-65"),sQuery(id+"F10.wireOp",EDGE,"E336.sketch_text.stroke-66"),sQuery(id+"F10.wireOp",EDGE,"E336.sketch_text.stroke-67"),sQuery(id+"F10.wireOp",EDGE,"E336.sketch_text.stroke-68"),sQuery(id+"F10.wireOp",EDGE,"E336.sketch_text.stroke-69"),sQuery(id+"F10.wireOp",EDGE,"E336.sketch_text.stroke-70"),sQuery(id+"F10.wireOp",EDGE,"E336.sketch_text.stroke-71"),sQuery(id+"F10.wireOp",EDGE,"E336.sketch_text.stroke-72"),sQuery(id+"F10.wireOp",EDGE,"E336.sketch_text.stroke-73"),sQuery(id+"F10.wireOp",EDGE,"E336.sketch_text.stroke-74"),sQuery(id+"F10.wireOp",EDGE,"E336.sketch_text.stroke-75"),sQuery(id+"F10.wireOp",EDGE,"E336.sketch_text.stroke-76"),sQuery(id+"F10.wireOp",EDGE,"E336.sketch_text.stroke-77"),sQuery(id+"F10.wireOp",EDGE,"E336.sketch_text.stroke-78"),sQuery(id+"F10.wireOp",EDGE,"E336.sketch_text.stroke-79"),sQuery(id+"F10.wireOp",EDGE,"E336.sketch_text.stroke-80"),sQuery(id+"F10.wireOp",EDGE,"E336.sketch_text.stroke-81"),sQuery(id+"F10.wireOp",EDGE,"E336.sketch_text.stroke-82"),sQuery(id+"F10.wireOp",EDGE,"E336.sketch_text.stroke-83"),sQuery(id+"F10.wireOp",EDGE,"E336.sketch_text.stroke-84"),sQuery(id+"F10.wireOp",EDGE,"E336.sketch_text.stroke-85"),sQuery(id+"F10.wireOp",EDGE,"E336.sketch_text.stroke-86"),sQuery(id+"F10.wireOp",EDGE,"E336.sketch_text.stroke-87"),sQuery(id+"F10.wireOp",EDGE,"E336.sketch_text.stroke-88"),sQuery(id+"F10.wireOp",EDGE,"E336.sketch_text.stroke-89"),sQuery(id+"F10.wireOp",EDGE,"E336.sketch_text.stroke-90"),sQuery(id+"F10.wireOp",EDGE,"E336.sketch_text.stroke-91"),sQuery(id+"F10.wireOp",EDGE,"E336.sketch_text.stroke-92"),sQuery(id+"F10.wireOp",EDGE,"E336.sketch_text.stroke-93"),sQuery(id+"F10.wireOp",EDGE,"E336.sketch_text.stroke-94"),sQuery(id+"F10.wireOp",EDGE,"E336.sketch_text.stroke-95"),sQuery(id+"F10.wireOp",EDGE,"E336.sketch_text.stroke-96"),sQuery(id+"F10.wireOp",EDGE,"E336.sketch_text.stroke-97"),sQuery(id+"F10.wireOp",EDGE,"E336.sketch_text.stroke-98"),sQuery(id+"F10.wireOp",EDGE,"E336.sketch_text.stroke-99"),sQuery(id+"F10.wireOp",EDGE,"E336.sketch_text.stroke-100"),sQuery(id+"F10.wireOp",EDGE,"E336.sketch_text.stroke-101"),sQuery(id+"F10.wireOp",EDGE,"E336.sketch_text.stroke-102"),sQuery(id+"F10.wireOp",EDGE,"E336.sketch_text.stroke-103"),sQuery(id+"F10.wireOp",EDGE,"E336.sketch_text.stroke-104"),sQuery(id+"F10.wireOp",EDGE,"E336.sketch_text.stroke-105"),sQuery(id+"F10.wireOp",EDGE,"E336.sketch_text.stroke-106"),sQuery(id+"F10.wireOp",EDGE,"E336.sketch_text.stroke-107"),sQuery(id+"F10.wireOp",EDGE,"E336.sketch_text.stroke-108"),sQuery(id+"F10.wireOp",EDGE,"E336.sketch_text.stroke-109"),sQuery(id+"F10.wireOp",EDGE,"E336.sketch_text.stroke-110"),sQuery(id+"F10.wireOp",EDGE,"E336.sketch_text.stroke-111"),sQuery(id+"F10.wireOp",EDGE,"E336.sketch_text.stroke-112"),sQuery(id+"F10.wireOp",EDGE,"E336.sketch_text.stroke-113"),sQuery(id+"F10.wireOp",EDGE,"E336.sketch_text.stroke-114"),sQuery(id+"F10.wireOp",EDGE,"E336.sketch_text.stroke-115"),sQuery(id+"F10.wireOp",EDGE,"E337.sketch_text.stroke-0"),sQuery(id+"F10.wireOp",EDGE,"E337.sketch_text.stroke-1"),sQuery(id+"F10.wireOp",EDGE,"E337.sketch_text.stroke-2"),sQuery(id+"F10.wireOp",EDGE,"E337.sketch_text.stroke-3"),sQuery(id+"F10.wireOp",EDGE,"E337.sketch_text.stroke-4"),sQuery(id+"F10.wireOp",EDGE,"E337.sketch_text.stroke-5"),sQuery(id+"F10.wireOp",EDGE,"E337.sketch_text.stroke-6"),sQuery(id+"F10.wireOp",EDGE,"E337.sketch_text.stroke-7"),sQuery(id+"F10.wireOp",EDGE,"E337.sketch_text.stroke-8"),sQuery(id+"F10.wireOp",EDGE,"E337.sketch_text.stroke-9"),sQuery(id+"F10.wireOp",EDGE,"E337.sketch_text.stroke-10"),sQuery(id+"F10.wireOp",EDGE,"E337.sketch_text.stroke-11"),sQuery(id+"F10.wireOp",EDGE,"E337.sketch_text.stroke-12"),sQuery(id+"F10.wireOp",EDGE,"E337.sketch_text.stroke-13"),sQuery(id+"F10.wireOp",EDGE,"E337.sketch_text.stroke-14"),sQuery(id+"F10.wireOp",EDGE,"E337.sketch_text.stroke-15"),sQuery(id+"F10.wireOp",EDGE,"E337.sketch_text.stroke-16"),sQuery(id+"F10.wireOp",EDGE,"E337.sketch_text.stroke-17"),sQuery(id+"F10.wireOp",EDGE,"E337.sketch_text.stroke-18"),sQuery(id+"F10.wireOp",EDGE,"E337.sketch_text.stroke-19"),sQuery(id+"F10.wireOp",EDGE,"E337.sketch_text.stroke-20"),sQuery(id+"F10.wireOp",EDGE,"E337.sketch_text.stroke-21"),sQuery(id+"F10.wireOp",EDGE,"E337.sketch_text.stroke-22"),sQuery(id+"F10.wireOp",EDGE,"E337.sketch_text.stroke-23"),sQuery(id+"F10.wireOp",EDGE,"E337.sketch_text.stroke-24"),sQuery(id+"F10.wireOp",EDGE,"E337.sketch_text.stroke-25"),sQuery(id+"F10.wireOp",EDGE,"E337.sketch_text.stroke-26"),sQuery(id+"F10.wireOp",EDGE,"E337.sketch_text.stroke-27"),sQuery(id+"F10.wireOp",EDGE,"E337.sketch_text.stroke-28"),sQuery(id+"F10.wireOp",EDGE,"E337.sketch_text.stroke-29"),sQuery(id+"F10.wireOp",EDGE,"E337.sketch_text.stroke-30"),sQuery(id+"F10.wireOp",EDGE,"E337.sketch_text.stroke-31"),sQuery(id+"F10.wireOp",EDGE,"E337.sketch_text.stroke-32"),sQuery(id+"F10.wireOp",EDGE,"E337.sketch_text.stroke-33"),sQuery(id+"F10.wireOp",EDGE,"E337.sketch_text.stroke-34"),sQuery(id+"F10.wireOp",EDGE,"E337.sketch_text.stroke-35"),sQuery(id+"F10.wireOp",EDGE,"E337.sketch_text.stroke-36"),sQuery(id+"F10.wireOp",EDGE,"E337.sketch_text.stroke-37"),sQuery(id+"F10.wireOp",EDGE,"E337.sketch_text.stroke-38"),sQuery(id+"F10.wireOp",EDGE,"E337.sketch_text.stroke-39"),sQuery(id+"F10.wireOp",EDGE,"E337.sketch_text.stroke-40"),sQuery(id+"F10.wireOp",EDGE,"E337.sketch_text.stroke-41"),sQuery(id+"F10.wireOp",EDGE,"E337.sketch_text.stroke-42"),sQuery(id+"F10.wireOp",EDGE,"E337.sketch_text.stroke-43"),sQuery(id+"F10.wireOp",EDGE,"E337.sketch_text.stroke-44"),sQuery(id+"F10.wireOp",EDGE,"E337.sketch_text.stroke-45"),sQuery(id+"F10.wireOp",EDGE,"E337.sketch_text.stroke-46"),sQuery(id+"F10.wireOp",EDGE,"E337.sketch_text.stroke-47"),sQuery(id+"F10.wireOp",EDGE,"E337.sketch_text.stroke-48"),sQuery(id+"F10.wireOp",EDGE,"E337.sketch_text.stroke-49"),sQuery(id+"F10.wireOp",EDGE,"E337.sketch_text.stroke-50"),sQuery(id+"F10.wireOp",EDGE,"E337.sketch_text.stroke-51"),sQuery(id+"F10.wireOp",EDGE,"E337.sketch_text.stroke-52"),sQuery(id+"F10.wireOp",EDGE,"E337.sketch_text.stroke-53"),sQuery(id+"F10.wireOp",EDGE,"E337.sketch_text.stroke-54"),sQuery(id+"F10.wireOp",EDGE,"E337.sketch_text.stroke-55"),sQuery(id+"F10.wireOp",EDGE,"E337.sketch_text.stroke-56"),sQuery(id+"F10.wireOp",EDGE,"E337.sketch_text.stroke-57"),sQuery(id+"F10.wireOp",EDGE,"E337.sketch_text.stroke-58"),sQuery(id+"F10.wireOp",EDGE,"E337.sketch_text.stroke-59"),sQuery(id+"F10.wireOp",EDGE,"E337.sketch_text.stroke-60"),sQuery(id+"F10.wireOp",EDGE,"E337.sketch_text.stroke-61"),sQuery(id+"F10.wireOp",EDGE,"E337.sketch_text.stroke-62"),sQuery(id+"F10.wireOp",EDGE,"E337.sketch_text.stroke-63"),sQuery(id+"F10.wireOp",EDGE,"E337.sketch_text.stroke-64"),sQuery(id+"F10.wireOp",EDGE,"E337.sketch_text.stroke-65"),sQuery(id+"F10.wireOp",EDGE,"E337.sketch_text.stroke-66"),sQuery(id+"F10.wireOp",EDGE,"E337.sketch_text.stroke-67"),sQuery(id+"F10.wireOp",EDGE,"E337.sketch_text.stroke-68"),sQuery(id+"F10.wireOp",EDGE,"E337.sketch_text.stroke-69"),sQuery(id+"F10.wireOp",EDGE,"E337.sketch_text.stroke-70"),sQuery(id+"F10.wireOp",EDGE,"E337.sketch_text.stroke-71"),sQuery(id+"F10.wireOp",EDGE,"E337.sketch_text.stroke-72"),sQuery(id+"F10.wireOp",EDGE,"E337.sketch_text.stroke-73"),sQuery(id+"F10.wireOp",EDGE,"E337.sketch_text.stroke-74"),sQuery(id+"F10.wireOp",EDGE,"E337.sketch_text.stroke-75"),sQuery(id+"F10.wireOp",EDGE,"E337.sketch_text.stroke-76"),sQuery(id+"F10.wireOp",EDGE,"E337.sketch_text.stroke-77"),sQuery(id+"F10.wireOp",EDGE,"E337.sketch_text.stroke-78"),sQuery(id+"F10.wireOp",EDGE,"E337.sketch_text.stroke-79"),sQuery(id+"F10.wireOp",EDGE,"E337.sketch_text.stroke-80"),sQuery(id+"F10.wireOp",EDGE,"E337.sketch_text.stroke-81"),sQuery(id+"F10.wireOp",EDGE,"E337.sketch_text.stroke-82"),sQuery(id+"F10.wireOp",EDGE,"E337.sketch_text.stroke-83"),sQuery(id+"F10.wireOp",EDGE,"E337.sketch_text.stroke-84"),sQuery(id+"F10.wireOp",EDGE,"E337.sketch_text.stroke-85"),sQuery(id+"F10.wireOp",EDGE,"E337.sketch_text.stroke-86"),sQuery(id+"F10.wireOp",EDGE,"E337.sketch_text.stroke-87"),sQuery(id+"F10.wireOp",EDGE,"E337.sketch_text.stroke-88"),sQuery(id+"F10.wireOp",EDGE,"E337.sketch_text.stroke-89"),sQuery(id+"F10.wireOp",EDGE,"E337.sketch_text.stroke-90"),sQuery(id+"F10.wireOp",EDGE,"E337.sketch_text.stroke-91"),sQuery(id+"F10.wireOp",EDGE,"E337.sketch_text.stroke-92"),sQuery(id+"F10.wireOp",EDGE,"E337.sketch_text.stroke-93"),sQuery(id+"F10.wireOp",EDGE,"E337.sketch_text.stroke-94"),sQuery(id+"F10.wireOp",EDGE,"E337.sketch_text.stroke-95"),sQuery(id+"F10.wireOp",EDGE,"E337.sketch_text.stroke-96"),sQuery(id+"F10.wireOp",EDGE,"E337.sketch_text.stroke-97"),sQuery(id+"F10.wireOp",EDGE,"E337.sketch_text.stroke-98"),sQuery(id+"F10.wireOp",EDGE,"E337.sketch_text.stroke-99"),sQuery(id+"F10.wireOp",EDGE,"E337.sketch_text.stroke-100"),sQuery(id+"F10.wireOp",EDGE,"E337.sketch_text.stroke-101"),sQuery(id+"F10.wireOp",EDGE,"E337.sketch_text.stroke-102"),sQuery(id+"F10.wireOp",EDGE,"E337.sketch_text.stroke-103"),sQuery(id+"F10.wireOp",EDGE,"E337.sketch_text.stroke-104"),sQuery(id+"F10.wireOp",EDGE,"E337.sketch_text.stroke-105"),sQuery(id+"F10.wireOp",EDGE,"E337.sketch_text.stroke-106"),sQuery(id+"F10.wireOp",EDGE,"E337.sketch_text.stroke-107"),sQuery(id+"F10.wireOp",EDGE,"E337.sketch_text.stroke-108"),sQuery(id+"F10.wireOp",EDGE,"E337.sketch_text.stroke-109"),sQuery(id+"F10.wireOp",EDGE,"E337.sketch_text.stroke-110"),sQuery(id+"F10.wireOp",EDGE,"E337.sketch_text.stroke-111"),sQuery(id+"F10.wireOp",EDGE,"E337.sketch_text.stroke-112"),sQuery(id+"F10.wireOp",EDGE,"E337.sketch_text.stroke-113"),sQuery(id+"F10.wireOp",EDGE,"E337.sketch_text.stroke-114"),sQuery(id+"F10.wireOp",EDGE,"E337.sketch_text.stroke-115"),sQuery(id+"F10.wireOp",EDGE,"E337.sketch_text.stroke-116"),sQuery(id+"F10.wireOp",EDGE,"E337.sketch_text.stroke-117"),sQuery(id+"F10.wireOp",EDGE,"E337.sketch_text.stroke-118"),sQuery(id+"F10.wireOp",EDGE,"E337.sketch_text.stroke-119"),sQuery(id+"F10.wireOp",EDGE,"E337.sketch_text.stroke-120"),sQuery(id+"F10.wireOp",EDGE,"E337.sketch_text.stroke-121"),sQuery(id+"F10.wireOp",EDGE,"E337.sketch_text.stroke-122"),sQuery(id+"F10.wireOp",EDGE,"E337.sketch_text.stroke-123"),sQuery(id+"F10.wireOp",EDGE,"E337.sketch_text.stroke-124"),sQuery(id+"F10.wireOp",EDGE,"E337.sketch_text.stroke-125"),sQuery(id+"F10.wireOp",EDGE,"E337.sketch_text.stroke-126"),sQuery(id+"F10.wireOp",EDGE,"E337.sketch_text.stroke-127"),sQuery(id+"F10.wireOp",EDGE,"E337.sketch_text.stroke-128"),sQuery(id+"F10.wireOp",EDGE,"E337.sketch_text.stroke-129"),sQuery(id+"F10.wireOp",EDGE,"E338.sketch_text.stroke-0"),sQuery(id+"F10.wireOp",EDGE,"E338.sketch_text.stroke-1"),sQuery(id+"F10.wireOp",EDGE,"E338.sketch_text.stroke-2"),sQuery(id+"F10.wireOp",EDGE,"E338.sketch_text.stroke-3"),sQuery(id+"F10.wireOp",EDGE,"E338.sketch_text.stroke-4"),sQuery(id+"F10.wireOp",EDGE,"E338.sketch_text.stroke-5"),sQuery(id+"F10.wireOp",EDGE,"E338.sketch_text.stroke-6"),sQuery(id+"F10.wireOp",EDGE,"E338.sketch_text.stroke-7"),sQuery(id+"F10.wireOp",EDGE,"E338.sketch_text.stroke-8"),sQuery(id+"F10.wireOp",EDGE,"E338.sketch_text.stroke-9"),sQuery(id+"F10.wireOp",EDGE,"E338.sketch_text.stroke-10"),sQuery(id+"F10.wireOp",EDGE,"E338.sketch_text.stroke-11"),sQuery(id+"F10.wireOp",EDGE,"E338.sketch_text.stroke-12"),sQuery(id+"F10.wireOp",EDGE,"E338.sketch_text.stroke-13"),sQuery(id+"F10.wireOp",EDGE,"E338.sketch_text.stroke-14"),sQuery(id+"F10.wireOp",EDGE,"E338.sketch_text.stroke-15"),sQuery(id+"F10.wireOp",EDGE,"E338.sketch_text.stroke-16"),sQuery(id+"F10.wireOp",EDGE,"E338.sketch_text.stroke-17"),sQuery(id+"F10.wireOp",EDGE,"E338.sketch_text.stroke-18"),sQuery(id+"F10.wireOp",EDGE,"E338.sketch_text.stroke-19"),sQuery(id+"F10.wireOp",EDGE,"E338.sketch_text.stroke-20"),sQuery(id+"F10.wireOp",EDGE,"E338.sketch_text.stroke-21"),sQuery(id+"F10.wireOp",EDGE,"E338.sketch_text.stroke-22"),sQuery(id+"F10.wireOp",EDGE,"E338.sketch_text.stroke-23"),sQuery(id+"F10.wireOp",EDGE,"E338.sketch_text.stroke-24"),sQuery(id+"F10.wireOp",EDGE,"E338.sketch_text.stroke-25"),sQuery(id+"F10.wireOp",EDGE,"E338.sketch_text.stroke-26"),sQuery(id+"F10.wireOp",EDGE,"E338.sketch_text.stroke-27"),sQuery(id+"F10.wireOp",EDGE,"E338.sketch_text.stroke-28"),sQuery(id+"F10.wireOp",EDGE,"E338.sketch_text.stroke-29"),sQuery(id+"F10.wireOp",EDGE,"E338.sketch_text.stroke-30"),sQuery(id+"F10.wireOp",EDGE,"E338.sketch_text.stroke-31"),sQuery(id+"F10.wireOp",EDGE,"E338.sketch_text.stroke-32"),sQuery(id+"F10.wireOp",EDGE,"E338.sketch_text.stroke-33"),sQuery(id+"F10.wireOp",EDGE,"E338.sketch_text.stroke-34"),sQuery(id+"F10.wireOp",EDGE,"E338.sketch_text.stroke-35"),sQuery(id+"F10.wireOp",EDGE,"E338.sketch_text.stroke-36"),sQuery(id+"F10.wireOp",EDGE,"E338.sketch_text.stroke-37"),sQuery(id+"F10.wireOp",EDGE,"E338.sketch_text.stroke-38"),sQuery(id+"F10.wireOp",EDGE,"E338.sketch_text.stroke-39"),sQuery(id+"F10.wireOp",EDGE,"E338.sketch_text.stroke-40"),sQuery(id+"F10.wireOp",EDGE,"E338.sketch_text.stroke-41"),sQuery(id+"F10.wireOp",EDGE,"E338.sketch_text.stroke-42"),sQuery(id+"F10.wireOp",EDGE,"E338.sketch_text.stroke-43"),sQuery(id+"F10.wireOp",EDGE,"E338.sketch_text.stroke-44"),sQuery(id+"F10.wireOp",EDGE,"E338.sketch_text.stroke-45"),sQuery(id+"F10.wireOp",EDGE,"E338.sketch_text.stroke-46"),sQuery(id+"F10.wireOp",EDGE,"E338.sketch_text.stroke-47"),sQuery(id+"F10.wireOp",EDGE,"E338.sketch_text.stroke-48"),sQuery(id+"F10.wireOp",EDGE,"E338.sketch_text.stroke-49"),sQuery(id+"F10.wireOp",EDGE,"E338.sketch_text.stroke-50"),sQuery(id+"F10.wireOp",EDGE,"E338.sketch_text.stroke-51"),sQuery(id+"F10.wireOp",EDGE,"E338.sketch_text.stroke-52"),sQuery(id+"F10.wireOp",EDGE,"E338.sketch_text.stroke-53"),sQuery(id+"F10.wireOp",EDGE,"E338.sketch_text.stroke-54"),sQuery(id+"F10.wireOp",EDGE,"E338.sketch_text.stroke-55"),sQuery(id+"F10.wireOp",EDGE,"E338.sketch_text.stroke-56"),sQuery(id+"F10.wireOp",EDGE,"E338.sketch_text.stroke-57"),sQuery(id+"F10.wireOp",EDGE,"E338.sketch_text.stroke-58"),sQuery(id+"F10.wireOp",EDGE,"E338.sketch_text.stroke-59"),sQuery(id+"F10.wireOp",EDGE,"E338.sketch_text.stroke-60"),sQuery(id+"F10.wireOp",EDGE,"E338.sketch_text.stroke-61"),sQuery(id+"F10.wireOp",EDGE,"E338.sketch_text.stroke-62"),sQuery(id+"F10.wireOp",EDGE,"E338.sketch_text.stroke-63"),sQuery(id+"F10.wireOp",EDGE,"E338.sketch_text.stroke-64"),sQuery(id+"F10.wireOp",EDGE,"E338.sketch_text.stroke-65"),sQuery(id+"F10.wireOp",EDGE,"E338.sketch_text.stroke-66"),sQuery(id+"F10.wireOp",EDGE,"E338.sketch_text.stroke-67"),sQuery(id+"F10.wireOp",EDGE,"E338.sketch_text.stroke-68"),sQuery(id+"F10.wireOp",EDGE,"E338.sketch_text.stroke-69"),sQuery(id+"F10.wireOp",EDGE,"E338.sketch_text.stroke-70"),sQuery(id+"F10.wireOp",EDGE,"E338.sketch_text.stroke-71"),sQuery(id+"F10.wireOp",EDGE,"E338.sketch_text.stroke-72"),sQuery(id+"F10.wireOp",EDGE,"E338.sketch_text.stroke-73"),sQuery(id+"F10.wireOp",EDGE,"E338.sketch_text.stroke-74"),sQuery(id+"F10.wireOp",EDGE,"E338.sketch_text.stroke-75"),sQuery(id+"F10.wireOp",EDGE,"E338.sketch_text.stroke-76"),sQuery(id+"F10.wireOp",EDGE,"E338.sketch_text.stroke-77"),sQuery(id+"F10.wireOp",EDGE,"E338.sketch_text.stroke-78"),sQuery(id+"F10.wireOp",EDGE,"E338.sketch_text.stroke-79"),sQuery(id+"F10.wireOp",EDGE,"E338.sketch_text.stroke-80"),sQuery(id+"F10.wireOp",EDGE,"E338.sketch_text.stroke-81"),sQuery(id+"F10.wireOp",EDGE,"E338.sketch_text.stroke-82"),sQuery(id+"F10.wireOp",EDGE,"E338.sketch_text.stroke-83"),sQuery(id+"F10.wireOp",EDGE,"E338.sketch_text.stroke-84"),sQuery(id+"F10.wireOp",EDGE,"E338.sketch_text.stroke-85"),sQuery(id+"F10.wireOp",EDGE,"E338.sketch_text.stroke-86"),sQuery(id+"F10.wireOp",EDGE,"E338.sketch_text.stroke-87"),sQuery(id+"F10.wireOp",EDGE,"E338.sketch_text.stroke-88"),sQuery(id+"F10.wireOp",EDGE,"E338.sketch_text.stroke-89"),sQuery(id+"F10.wireOp",EDGE,"E338.sketch_text.stroke-90"),sQuery(id+"F10.wireOp",EDGE,"E338.sketch_text.stroke-91"),sQuery(id+"F10.wireOp",EDGE,"E338.sketch_text.stroke-92"),sQuery(id+"F10.wireOp",EDGE,"E338.sketch_text.stroke-93"),sQuery(id+"F10.wireOp",EDGE,"E338.sketch_text.stroke-94"),sQuery(id+"F10.wireOp",EDGE,"E338.sketch_text.stroke-95"),sQuery(id+"F10.wireOp",EDGE,"E338.sketch_text.stroke-96"),sQuery(id+"F10.wireOp",EDGE,"E338.sketch_text.stroke-97"),sQuery(id+"F10.wireOp",EDGE,"E338.sketch_text.stroke-98"),sQuery(id+"F10.wireOp",EDGE,"E338.sketch_text.stroke-99"),sQuery(id+"F10.wireOp",EDGE,"E338.sketch_text.stroke-100"),sQuery(id+"F10.wireOp",EDGE,"E338.sketch_text.stroke-101"),sQuery(id+"F10.wireOp",EDGE,"E338.sketch_text.stroke-102"),sQuery(id+"F10.wireOp",EDGE,"E339.sketch_text.stroke-0"),sQuery(id+"F10.wireOp",EDGE,"E339.sketch_text.stroke-1"),sQuery(id+"F10.wireOp",EDGE,"E339.sketch_text.stroke-2"),sQuery(id+"F10.wireOp",EDGE,"E339.sketch_text.stroke-3"),sQuery(id+"F10.wireOp",EDGE,"E339.sketch_text.stroke-4"),sQuery(id+"F10.wireOp",EDGE,"E339.sketch_text.stroke-5"),sQuery(id+"F10.wireOp",EDGE,"E339.sketch_text.stroke-6"),sQuery(id+"F10.wireOp",EDGE,"E339.sketch_text.stroke-7"),sQuery(id+"F10.wireOp",EDGE,"E339.sketch_text.stroke-8"),sQuery(id+"F10.wireOp",EDGE,"E339.sketch_text.stroke-9"),sQuery(id+"F10.wireOp",EDGE,"E339.sketch_text.stroke-10"),sQuery(id+"F10.wireOp",EDGE,"E339.sketch_text.stroke-11"),sQuery(id+"F10.wireOp",EDGE,"E339.sketch_text.stroke-12"),sQuery(id+"F10.wireOp",EDGE,"E339.sketch_text.stroke-13"),sQuery(id+"F10.wireOp",EDGE,"E339.sketch_text.stroke-14"),sQuery(id+"F10.wireOp",EDGE,"E339.sketch_text.stroke-15"),sQuery(id+"F10.wireOp",EDGE,"E339.sketch_text.stroke-16"),sQuery(id+"F10.wireOp",EDGE,"E339.sketch_text.stroke-17"),sQuery(id+"F10.wireOp",EDGE,"E339.sketch_text.stroke-18"),sQuery(id+"F10.wireOp",EDGE,"E339.sketch_text.stroke-19"),sQuery(id+"F10.wireOp",EDGE,"E339.sketch_text.stroke-20"),sQuery(id+"F10.wireOp",EDGE,"E339.sketch_text.stroke-21"),sQuery(id+"F10.wireOp",EDGE,"E339.sketch_text.stroke-22"),sQuery(id+"F10.wireOp",EDGE,"E339.sketch_text.stroke-23"),sQuery(id+"F10.wireOp",EDGE,"E339.sketch_text.stroke-24"),sQuery(id+"F10.wireOp",EDGE,"E339.sketch_text.stroke-25"),sQuery(id+"F10.wireOp",EDGE,"E339.sketch_text.stroke-26"),sQuery(id+"F10.wireOp",EDGE,"E339.sketch_text.stroke-27"),sQuery(id+"F10.wireOp",EDGE,"E339.sketch_text.stroke-28"),sQuery(id+"F10.wireOp",EDGE,"E339.sketch_text.stroke-29"),sQuery(id+"F10.wireOp",EDGE,"E339.sketch_text.stroke-30"),sQuery(id+"F10.wireOp",EDGE,"E339.sketch_text.stroke-31"),sQuery(id+"F10.wireOp",EDGE,"E339.sketch_text.stroke-32"),sQuery(id+"F10.wireOp",EDGE,"E339.sketch_text.stroke-33"),sQuery(id+"F10.wireOp",EDGE,"E339.sketch_text.stroke-34"),sQuery(id+"F10.wireOp",EDGE,"E339.sketch_text.stroke-35"),sQuery(id+"F10.wireOp",EDGE,"E339.sketch_text.stroke-36"),sQuery(id+"F10.wireOp",EDGE,"E339.sketch_text.stroke-37"),sQuery(id+"F10.wireOp",EDGE,"E339.sketch_text.stroke-38"),sQuery(id+"F10.wireOp",EDGE,"E339.sketch_text.stroke-39"),sQuery(id+"F10.wireOp",EDGE,"E339.sketch_text.stroke-40"),sQuery(id+"F10.wireOp",EDGE,"E339.sketch_text.stroke-41"),sQuery(id+"F10.wireOp",EDGE,"E339.sketch_text.stroke-42"),sQuery(id+"F10.wireOp",EDGE,"E339.sketch_text.stroke-43"),sQuery(id+"F10.wireOp",EDGE,"E339.sketch_text.stroke-44"),sQuery(id+"F10.wireOp",EDGE,"E339.sketch_text.stroke-45"),sQuery(id+"F10.wireOp",EDGE,"E339.sketch_text.stroke-46"),sQuery(id+"F10.wireOp",EDGE,"E339.sketch_text.stroke-47"),sQuery(id+"F10.wireOp",EDGE,"E339.sketch_text.stroke-48"),sQuery(id+"F10.wireOp",EDGE,"E339.sketch_text.stroke-49"),sQuery(id+"F10.wireOp",EDGE,"E339.sketch_text.stroke-50"),sQuery(id+"F10.wireOp",EDGE,"E339.sketch_text.stroke-51"),sQuery(id+"F10.wireOp",EDGE,"E339.sketch_text.stroke-52"),sQuery(id+"F10.wireOp",EDGE,"E339.sketch_text.stroke-53"),sQuery(id+"F10.wireOp",EDGE,"E339.sketch_text.stroke-54"),sQuery(id+"F10.wireOp",EDGE,"E339.sketch_text.stroke-55"),sQuery(id+"F10.wireOp",EDGE,"E339.sketch_text.stroke-56"),sQuery(id+"F10.wireOp",EDGE,"E339.sketch_text.stroke-57"),sQuery(id+"F10.wireOp",EDGE,"E339.sketch_text.stroke-58"),sQuery(id+"F10.wireOp",EDGE,"E339.sketch_text.stroke-59"),sQuery(id+"F10.wireOp",EDGE,"E339.sketch_text.stroke-60"),sQuery(id+"F10.wireOp",EDGE,"E339.sketch_text.stroke-61"),sQuery(id+"F10.wireOp",EDGE,"E339.sketch_text.stroke-62"),sQuery(id+"F10.wireOp",EDGE,"E339.sketch_text.stroke-63"),sQuery(id+"F10.wireOp",EDGE,"E339.sketch_text.stroke-64"),sQuery(id+"F10.wireOp",EDGE,"E339.sketch_text.stroke-65"),sQuery(id+"F10.wireOp",EDGE,"E339.sketch_text.stroke-66"),sQuery(id+"F10.wireOp",EDGE,"E339.sketch_text.stroke-67"),sQuery(id+"F10.wireOp",EDGE,"E339.sketch_text.stroke-68"),sQuery(id+"F10.wireOp",EDGE,"E339.sketch_text.stroke-69"),sQuery(id+"F10.wireOp",EDGE,"E339.sketch_text.stroke-70"),sQuery(id+"F10.wireOp",EDGE,"E339.sketch_text.stroke-71"),sQuery(id+"F10.wireOp",EDGE,"E339.sketch_text.stroke-72"),sQuery(id+"F10.wireOp",EDGE,"E339.sketch_text.stroke-73"),sQuery(id+"F10.wireOp",EDGE,"E339.sketch_text.stroke-74"),sQuery(id+"F10.wireOp",EDGE,"E339.sketch_text.stroke-75"),sQuery(id+"F10.wireOp",EDGE,"E339.sketch_text.stroke-76"),sQuery(id+"F10.wireOp",EDGE,"E339.sketch_text.stroke-77"),sQuery(id+"F10.wireOp",EDGE,"E339.sketch_text.stroke-78"),sQuery(id+"F10.wireOp",EDGE,"E339.sketch_text.stroke-79"),sQuery(id+"F10.wireOp",EDGE,"E339.sketch_text.stroke-80"),sQuery(id+"F10.wireOp",EDGE,"E339.sketch_text.stroke-81"),sQuery(id+"F10.wireOp",EDGE,"E339.sketch_text.stroke-82"),sQuery(id+"F10.wireOp",EDGE,"E339.sketch_text.stroke-83"),sQuery(id+"F10.wireOp",EDGE,"E339.sketch_text.stroke-84"),sQuery(id+"F10.wireOp",EDGE,"E339.sketch_text.stroke-85"),sQuery(id+"F10.wireOp",EDGE,"E339.sketch_text.stroke-86"),sQuery(id+"F10.wireOp",EDGE,"E339.sketch_text.stroke-87"),sQuery(id+"F10.wireOp",EDGE,"E339.sketch_text.stroke-88"),sQuery(id+"F10.wireOp",EDGE,"E339.sketch_text.stroke-89"),sQuery(id+"F10.wireOp",EDGE,"E339.sketch_text.stroke-90"),sQuery(id+"F10.wireOp",EDGE,"E339.sketch_text.stroke-91"),sQuery(id+"F10.wireOp",EDGE,"E339.sketch_text.stroke-92"),sQuery(id+"F10.wireOp",EDGE,"E339.sketch_text.stroke-93"),sQuery(id+"F10.wireOp",EDGE,"E339.sketch_text.stroke-94"),sQuery(id+"F10.wireOp",EDGE,"E339.sketch_text.stroke-95"),sQuery(id+"F10.wireOp",EDGE,"E339.sketch_text.stroke-96"),sQuery(id+"F10.wireOp",EDGE,"E339.sketch_text.stroke-97"),sQuery(id+"F10.wireOp",EDGE,"E339.sketch_text.stroke-98"),sQuery(id+"F10.wireOp",EDGE,"E339.sketch_text.stroke-99"),sQuery(id+"F10.wireOp",EDGE,"E339.sketch_text.stroke-100"),sQuery(id+"F10.wireOp",EDGE,"E339.sketch_text.stroke-101"),sQuery(id+"F10.wireOp",EDGE,"E339.sketch_text.stroke-102"),sQuery(id+"F10.wireOp",EDGE,"E339.sketch_text.stroke-103"),sQuery(id+"F10.wireOp",EDGE,"E339.sketch_text.stroke-104"),sQuery(id+"F10.wireOp",EDGE,"E339.sketch_text.stroke-105"),sQuery(id+"F10.wireOp",EDGE,"E339.sketch_text.stroke-106"),sQuery(id+"F10.wireOp",EDGE,"E339.sketch_text.stroke-107"),sQuery(id+"F10.wireOp",EDGE,"E339.sketch_text.stroke-108"),sQuery(id+"F10.wireOp",EDGE,"E339.sketch_text.stroke-109"),sQuery(id+"F10.wireOp",EDGE,"E339.sketch_text.stroke-110"),sQuery(id+"F10.wireOp",EDGE,"E339.sketch_text.stroke-111"),sQuery(id+"F10.wireOp",EDGE,"E339.sketch_text.stroke-112")])],"isStart":true})]});
            extrude(context, id + "F14", {"entities" : qUnion([Q0]), "operationType" : NewBodyOperationType.REMOVE, "endBound" : BoundingType.UP_TO_SURFACE, "oppositeDirection" : true, "endBoundEntityFace" : qUnion([Q1]), "depth" : 25 * mm});
        }
    });
